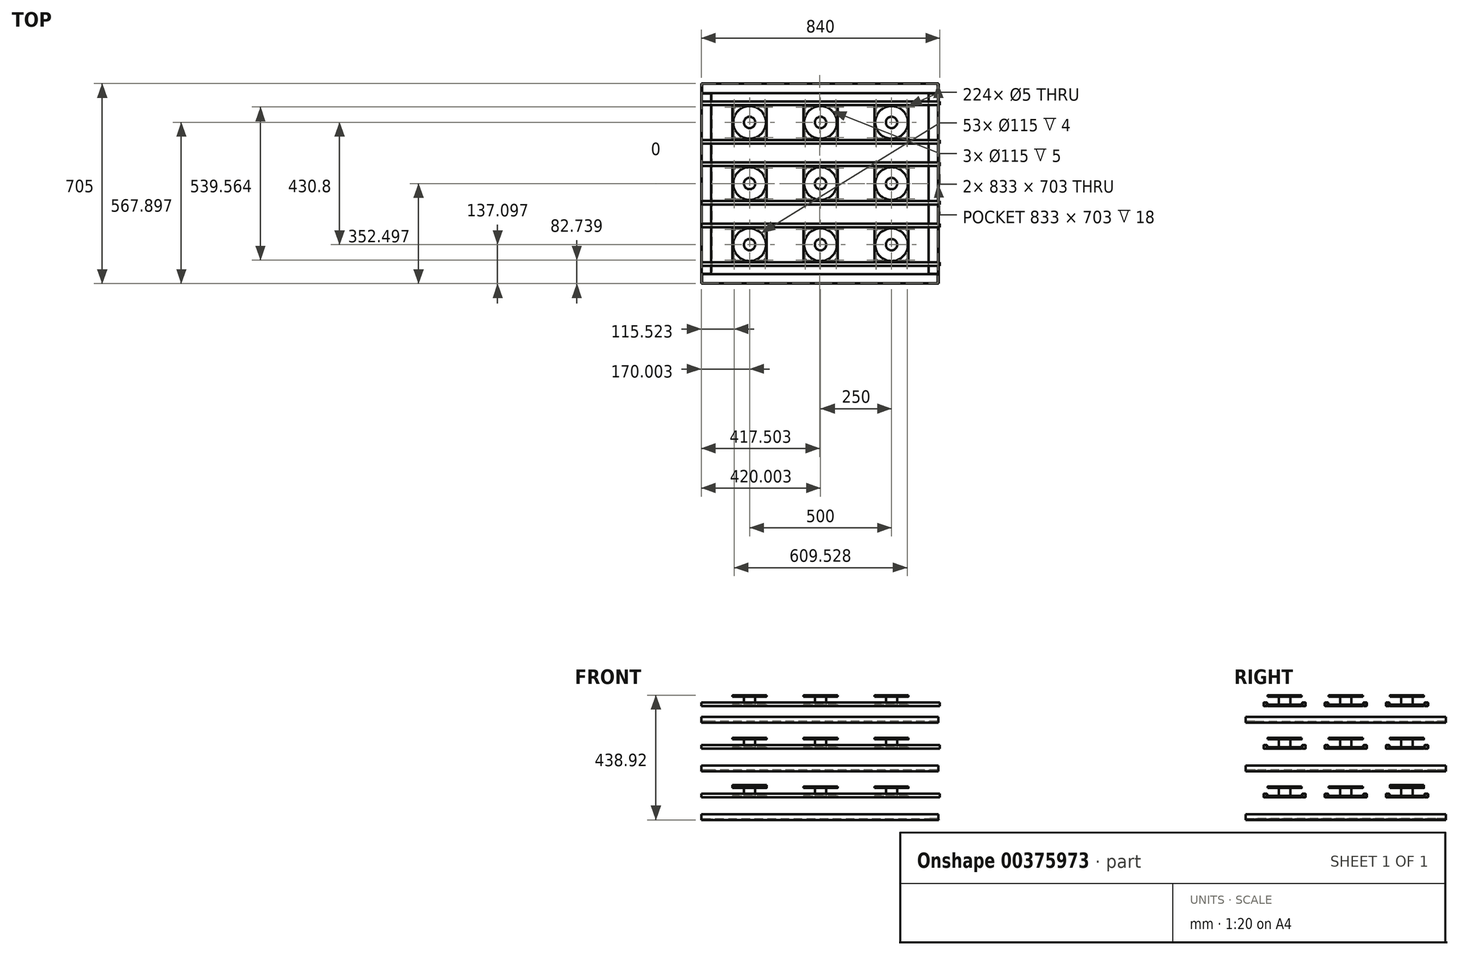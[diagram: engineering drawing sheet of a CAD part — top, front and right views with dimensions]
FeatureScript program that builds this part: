
annotation { "Feature Type Name" : "Feature", "Feature Type Description" : "" }
export const myFeature = defineFeature(function(context is Context, id is Id, definition is map)
    precondition{}
    {
        {
            var Q0;
            Q0=qCreatedBy(makeId("Top.planeOp"),FACE);
            var sketch = newSketch(context, id + "F0", { "sketchPlane" : qUnion([Q0])});
            skLineSegment(sketch, "E0.bottom", {"start": v(-587.5, -350.77) * mm, "end": v(247.5, -350.77) * mm});
            skLineSegment(sketch, "E0.top", {"start": v(-587.5, 354.23) * mm, "end": v(247.5, 354.23) * mm});
            skLineSegment(sketch, "E0.left", {"start": v(-587.5, -350.77) * mm, "end": v(-587.5, 354.23) * mm});
            skLineSegment(sketch, "E0.right", {"start": v(247.5, -350.77) * mm, "end": v(247.5, 354.23) * mm});
            skLineSegment(sketch, "E1.0", {"start": v(-586.5, -349.77) * mm, "end": v(-586.5, 353.23) * mm});
            skLineSegment(sketch, "E1.1", {"start": v(-586.5, -349.77) * mm, "end": v(246.5, -349.77) * mm});
            skLineSegment(sketch, "E1.2", {"start": v(246.5, -349.77) * mm, "end": v(246.5, 353.23) * mm});
            skLineSegment(sketch, "E1.3", {"start": v(-586.5, 353.23) * mm, "end": v(246.5, 353.23) * mm});
            skSolve(sketch);
        }
        {
            var Q0;
            Q0 = qSketchRegion(id + "F0", true);
            extrude(context, id + "F1", {"entities" : qUnion([Q0]), "depth" : 20 * mm});
        }
        {
            var Q0;
            Q0=qCreatedBy(makeId("Top.planeOp"),FACE);
            var sketch = newSketch(context, id + "F2", { "sketchPlane" : qUnion([Q0])});
            skLineSegment(sketch, "E2.bottom", {"start": v(-584.94, 352.72) * mm, "end": v(248.06, 352.72) * mm});
            skLineSegment(sketch, "E2.top", {"start": v(-584.94, -350.28) * mm, "end": v(248.06, -350.28) * mm});
            skLineSegment(sketch, "E2.left", {"start": v(-584.94, 352.72) * mm, "end": v(-584.94, -350.28) * mm});
            skLineSegment(sketch, "E2.right", {"start": v(248.06, 352.72) * mm, "end": v(248.06, -350.28) * mm});
            skSolve(sketch);
        }
        {
            var Q0;
            Q0 = qSketchRegion(id + "F2", true);
            extrude(context, id + "F3", {"entities" : qUnion([Q0]), "operationType" : NewBodyOperationType.ADD, "depth" : 1 * mm});
        }
        {
            var Q0;
            {var subQ0=sQuery(id+"F2.wireOp",EDGE,"E2.left");var subQ1=sQuery(id+"F2.wireOp",EDGE,"E2.bottom");Q0=makeQuery(id+"F3.boolean.opBoolean","SPLIT",FACE,{"disambiguationData":[TD([makeQuery(id+"F1.opExtrude","SWEPT_FACE",FACE,{"disambiguationData":[OSD([sQuery(id+"F0.wireOp",EDGE,"E1.1")])]})])],"derivedFrom":makeQuery(id+"F3.opExtrude","CAP_FACE",FACE,{"disambiguationData":[OSD([subQ1,sQuery(id+"F2.wireOp",EDGE,"E2.top"),subQ0,sQuery(id+"F2.wireOp",EDGE,"E2.right")])],"isStart":false})});}
            var sketch = newSketch(context, id + "F4", { "sketchPlane" : qUnion([Q0])});
            skLineSegment(sketch, "E3.bottom", {"start": v(-169.22, 352.72) * mm, "end": v(-584.22, 352.72) * mm});
            skLineSegment(sketch, "E3.top", {"start": v(-169.22, 319.72) * mm, "end": v(-584.22, 319.72) * mm});
            skLineSegment(sketch, "E3.right", {"start": v(-584.22, 352.72) * mm, "end": v(-584.22, 319.72) * mm});
            skLineSegment(sketch, "E4.bottom", {"start": v(-169.22, 352.72) * mm, "end": v(245.78, 352.72) * mm});
            skLineSegment(sketch, "E4.top", {"start": v(-169.22, 319.72) * mm, "end": v(245.78, 319.72) * mm});
            skLineSegment(sketch, "E4.right", {"start": v(245.78, 352.72) * mm, "end": v(245.78, 319.72) * mm});
            skLineSegment(sketch, "E5.bottom", {"start": v(-169.22, -349.77) * mm, "end": v(245.78, -349.77) * mm});
            skLineSegment(sketch, "E5.top", {"start": v(-169.22, -316.77) * mm, "end": v(245.78, -316.77) * mm});
            skLineSegment(sketch, "E5.right", {"start": v(245.78, -349.77) * mm, "end": v(245.78, -316.77) * mm});
            skLineSegment(sketch, "E6.bottom", {"start": v(-169.22, -349.77) * mm, "end": v(-584.22, -349.77) * mm});
            skLineSegment(sketch, "E6.top", {"start": v(-169.22, -316.77) * mm, "end": v(-584.22, -316.77) * mm});
            skLineSegment(sketch, "E6.right", {"start": v(-584.22, -349.77) * mm, "end": v(-584.22, -316.77) * mm});
            skSolve(sketch);
        }
        {
            var Q0;
            Q0=makeQuery(id+"F4.imprint","IMPRINT",FACE,{"disambiguationData":[TD([[makeQuery(id+"F4.imprint","IMPRINT",EDGE,{"derivedFrom":sQuery(id+"F4.wireOp",EDGE,"E3.bottom")}),-1.0]])]});
            extrude(context, id + "F5", {"entities" : qUnion([Q0]), "depth" : 3 * mm});
        }
        {
            var Q0;
            Q0=makeQuery(id+"F4.imprint","IMPRINT",FACE,{"disambiguationData":[TD([[makeQuery(id+"F4.imprint","IMPRINT",EDGE,{"derivedFrom":sQuery(id+"F4.wireOp",EDGE,"E5.bottom")}),1.0]])]});
            var Q1;
            Q1 = qSketchRegion(id + "F7", true);
            extrude(context, id + "F6", {"entities" : qUnion([Q0, Q1]), "depth" : 3 * mm});
        }
        {
            var Q0;
            {var subQ0=sQuery(id+"F2.wireOp",EDGE,"E2.left");var subQ1=sQuery(id+"F2.wireOp",EDGE,"E2.bottom");Q0=makeQuery(id+"F3.boolean.opBoolean","SPLIT",FACE,{"disambiguationData":[TD([makeQuery(id+"F1.opExtrude","SWEPT_FACE",FACE,{"disambiguationData":[OSD([sQuery(id+"F0.wireOp",EDGE,"E1.1")])]})])],"derivedFrom":makeQuery(id+"F3.opExtrude","CAP_FACE",FACE,{"disambiguationData":[OSD([subQ1,sQuery(id+"F2.wireOp",EDGE,"E2.top"),subQ0,sQuery(id+"F2.wireOp",EDGE,"E2.right")])],"isStart":false})});}
            var sketch = newSketch(context, id + "F7", { "sketchPlane" : qUnion([Q0])});
            skLineSegment(sketch, "E7.top", {"start": v(-584.94, 318.97) * mm, "end": v(-550.94, 318.97) * mm});
            skLineSegment(sketch, "E7.left", {"start": v(-584.94, 1.47) * mm, "end": v(-584.94, 318.97) * mm});
            skLineSegment(sketch, "E7.right", {"start": v(-550.94, 1.47) * mm, "end": v(-550.94, 318.97) * mm});
            skLineSegment(sketch, "E8.top", {"start": v(-584.94, -316.03) * mm, "end": v(-550.94, -316.03) * mm});
            skLineSegment(sketch, "E8.left", {"start": v(-584.94, 1.47) * mm, "end": v(-584.94, -316.03) * mm});
            skLineSegment(sketch, "E8.right", {"start": v(-550.94, 1.47) * mm, "end": v(-550.94, -316.03) * mm});
            skPoint(sketch, "E9.firstSnap0", {"position": v(246.5, 1.47) * mm});
            skLineSegment(sketch, "E9.top", {"start": v(246.5, 317.5) * mm, "end": v(212.5, 317.5) * mm});
            skLineSegment(sketch, "E9.left", {"start": v(246.5, 0) * mm, "end": v(246.5, 317.5) * mm});
            skLineSegment(sketch, "E9.right", {"start": v(212.5, 0) * mm, "end": v(212.5, 317.5) * mm});
            skLineSegment(sketch, "E10.top", {"start": v(246.5, -316.03) * mm, "end": v(212.5, -316.03) * mm});
            skLineSegment(sketch, "E10.left", {"start": v(246.5, 1.47) * mm, "end": v(246.5, -316.03) * mm});
            skLineSegment(sketch, "E10.right", {"start": v(212.5, 1.47) * mm, "end": v(212.5, -316.03) * mm});
            skSolve(sketch);
        }
        {
            var Q0;
            Q0=makeQuery(id+"F7.imprint","IMPRINT",FACE,{"disambiguationData":[TD([[makeQuery(id+"F7.imprint","IMPRINT",EDGE,{"derivedFrom":sQuery(id+"F7.wireOp",EDGE,"E7.top")}),-1.0]])]});
            var Q1;
            Q1=makeQuery(id+"F7.imprint","IMPRINT",FACE,{"disambiguationData":[TD([[makeQuery(id+"F7.imprint","IMPRINT",EDGE,{"derivedFrom":sQuery(id+"F7.wireOp",EDGE,"E9.top")}),1.0]])]});
            extrude(context, id + "F8", {"entities" : qUnion([Q0, Q1]), "depth" : 3 * mm});
        }
        {
            var Q0;
            Q0=makeQuery(id+"F7.imprint","IMPRINT",FACE,{"disambiguationData":[TD([[makeQuery(id+"F7.imprint","IMPRINT",EDGE,{"derivedFrom":sQuery(id+"F7.wireOp",EDGE,"E9.top")}),1.0]])]});
            extrude(context, id + "F9", {"entities" : qUnion([Q0]), "depth" : 3 * mm});
        }
        {
            var Q0;
            Q0=makeQuery(id+"F1.opExtrude","SWEPT_FACE",FACE,{"disambiguationData":[OSD([sQuery(id+"F0.wireOp",EDGE,"E0.left")])]});
            var sketch = newSketch(context, id + "F10", { "sketchPlane" : qUnion([Q0])});
            skLineSegment(sketch, "E11.bottom", {"start": v(285.87, 79.3) * mm, "end": v(277.17, 79.3) * mm});
            skLineSegment(sketch, "E11.top", {"start": v(285.87, 92) * mm, "end": v(277.17, 92) * mm});
            skLineSegment(sketch, "E11.left", {"start": v(287.87, 81.3) * mm, "end": v(287.87, 90) * mm});
            skLineSegment(sketch, "E11.right", {"start": v(275.17, 81.3) * mm, "end": v(275.17, 90) * mm});
            skLineSegment(sketch, "E12.0", {"start": v(286.87, 91) * mm, "end": v(276.17, 91) * mm});
            skLineSegment(sketch, "E12.1", {"start": v(286.87, 80.3) * mm, "end": v(286.87, 91) * mm});
            skLineSegment(sketch, "E12.2", {"start": v(286.87, 80.3) * mm, "end": v(276.17, 80.3) * mm});
            skLineSegment(sketch, "E12.3", {"start": v(276.17, 80.3) * mm, "end": v(276.17, 91) * mm});
            skPoint(sketch, "E13.visualSharp", {"position": v(275.17, 92) * mm});
            skArc(sketch, "E13.filletArc", {"start": v(277.17, 92) * mm, "mid": v(275.76, 91.41) * mm, "end": v(275.17, 90) * mm});
            skPoint(sketch, "E14.visualSharp", {"position": v(275.17, 79.3) * mm});
            skArc(sketch, "E14.filletArc", {"start": v(275.17, 81.3) * mm, "mid": v(275.76, 79.89) * mm, "end": v(277.17, 79.3) * mm});
            skPoint(sketch, "E15.visualSharp", {"position": v(287.87, 92) * mm});
            skArc(sketch, "E15.filletArc", {"start": v(287.87, 90) * mm, "mid": v(287.29, 91.41) * mm, "end": v(285.87, 92) * mm});
            skPoint(sketch, "E16.visualSharp", {"position": v(287.87, 79.3) * mm});
            skArc(sketch, "E16.filletArc", {"start": v(285.87, 79.3) * mm, "mid": v(287.29, 79.89) * mm, "end": v(287.87, 81.3) * mm});
            skLineSegment(sketch, "E17", {"start": v(277.17, 79.3) * mm, "end": v(275.17, 79.3) * mm});
            skLineSegment(sketch, "E18.bottom", {"start": v(150.17, 79.3) * mm, "end": v(141.47, 79.3) * mm});
            skLineSegment(sketch, "E18.top", {"start": v(150.17, 92) * mm, "end": v(141.47, 92) * mm});
            skLineSegment(sketch, "E18.left", {"start": v(152.17, 81.3) * mm, "end": v(152.17, 90) * mm});
            skLineSegment(sketch, "E18.right", {"start": v(139.47, 81.3) * mm, "end": v(139.47, 90) * mm});
            skLineSegment(sketch, "E19.0", {"start": v(151.17, 91) * mm, "end": v(140.47, 91) * mm});
            skLineSegment(sketch, "E19.1", {"start": v(151.17, 80.3) * mm, "end": v(151.17, 91) * mm});
            skLineSegment(sketch, "E19.2", {"start": v(151.17, 80.3) * mm, "end": v(140.47, 80.3) * mm});
            skLineSegment(sketch, "E19.3", {"start": v(140.47, 80.3) * mm, "end": v(140.47, 91) * mm});
            skPoint(sketch, "E20.visualSharp", {"position": v(152.17, 79.3) * mm});
            skArc(sketch, "E20.filletArc", {"start": v(150.17, 79.3) * mm, "mid": v(151.59, 79.89) * mm, "end": v(152.17, 81.3) * mm});
            skPoint(sketch, "E21.visualSharp", {"position": v(139.47, 79.3) * mm});
            skArc(sketch, "E21.filletArc", {"start": v(139.47, 81.3) * mm, "mid": v(140.06, 79.89) * mm, "end": v(141.47, 79.3) * mm});
            skPoint(sketch, "E22.visualSharp", {"position": v(139.47, 92) * mm});
            skArc(sketch, "E22.filletArc", {"start": v(141.47, 92) * mm, "mid": v(140.06, 91.41) * mm, "end": v(139.47, 90) * mm});
            skPoint(sketch, "E23.visualSharp", {"position": v(152.17, 92) * mm});
            skArc(sketch, "E23.filletArc", {"start": v(152.17, 90) * mm, "mid": v(151.59, 91.41) * mm, "end": v(150.17, 92) * mm});
            skLineSegment(sketch, "E24.bottom", {"start": v(70.47, 79.3) * mm, "end": v(61.77, 79.3) * mm});
            skLineSegment(sketch, "E24.top", {"start": v(70.47, 92) * mm, "end": v(61.77, 92) * mm});
            skLineSegment(sketch, "E24.left", {"start": v(72.47, 81.3) * mm, "end": v(72.47, 90) * mm});
            skLineSegment(sketch, "E24.right", {"start": v(59.77, 81.3) * mm, "end": v(59.77, 90) * mm});
            skLineSegment(sketch, "E25.0", {"start": v(60.77, 80.3) * mm, "end": v(60.77, 91) * mm});
            skLineSegment(sketch, "E25.1", {"start": v(71.47, 80.3) * mm, "end": v(60.77, 80.3) * mm});
            skLineSegment(sketch, "E25.2", {"start": v(71.47, 80.3) * mm, "end": v(71.47, 91) * mm});
            skLineSegment(sketch, "E25.3", {"start": v(71.47, 91) * mm, "end": v(60.77, 91) * mm});
            skPoint(sketch, "E26.visualSharp", {"position": v(59.77, 92) * mm});
            skArc(sketch, "E26.filletArc", {"start": v(61.77, 92) * mm, "mid": v(60.36, 91.41) * mm, "end": v(59.77, 90) * mm});
            skPoint(sketch, "E27.visualSharp", {"position": v(72.47, 92) * mm});
            skArc(sketch, "E27.filletArc", {"start": v(72.47, 90) * mm, "mid": v(71.89, 91.41) * mm, "end": v(70.47, 92) * mm});
            skPoint(sketch, "E28.visualSharp", {"position": v(59.77, 79.3) * mm});
            skArc(sketch, "E28.filletArc", {"start": v(59.77, 81.3) * mm, "mid": v(60.36, 79.89) * mm, "end": v(61.77, 79.3) * mm});
            skPoint(sketch, "E29.visualSharp", {"position": v(72.47, 79.3) * mm});
            skArc(sketch, "E29.filletArc", {"start": v(70.47, 79.3) * mm, "mid": v(71.89, 79.89) * mm, "end": v(72.47, 81.3) * mm});
            skLineSegment(sketch, "E30.bottom", {"start": v(-65.23, 79.3) * mm, "end": v(-73.93, 79.3) * mm});
            skLineSegment(sketch, "E30.top", {"start": v(-65.23, 92) * mm, "end": v(-73.93, 92) * mm});
            skLineSegment(sketch, "E30.left", {"start": v(-63.23, 81.3) * mm, "end": v(-63.23, 90) * mm});
            skLineSegment(sketch, "E30.right", {"start": v(-75.93, 81.3) * mm, "end": v(-75.93, 90) * mm});
            skLineSegment(sketch, "E31.0", {"start": v(-74.93, 80.3) * mm, "end": v(-74.93, 91) * mm});
            skLineSegment(sketch, "E31.1", {"start": v(-64.23, 80.3) * mm, "end": v(-74.93, 80.3) * mm});
            skLineSegment(sketch, "E31.2", {"start": v(-64.23, 80.3) * mm, "end": v(-64.23, 91) * mm});
            skLineSegment(sketch, "E31.3", {"start": v(-64.23, 91) * mm, "end": v(-74.93, 91) * mm});
            skPoint(sketch, "E32.visualSharp", {"position": v(-75.93, 92) * mm});
            skArc(sketch, "E32.filletArc", {"start": v(-73.93, 92) * mm, "mid": v(-75.34, 91.41) * mm, "end": v(-75.93, 90) * mm});
            skPoint(sketch, "E33.visualSharp", {"position": v(-63.23, 92) * mm});
            skArc(sketch, "E33.filletArc", {"start": v(-63.23, 90) * mm, "mid": v(-63.81, 91.41) * mm, "end": v(-65.23, 92) * mm});
            skPoint(sketch, "E34.visualSharp", {"position": v(-75.93, 79.3) * mm});
            skArc(sketch, "E34.filletArc", {"start": v(-75.93, 81.3) * mm, "mid": v(-75.34, 79.89) * mm, "end": v(-73.93, 79.3) * mm});
            skPoint(sketch, "E35.visualSharp", {"position": v(-63.23, 79.3) * mm});
            skArc(sketch, "E35.filletArc", {"start": v(-65.23, 79.3) * mm, "mid": v(-63.81, 79.89) * mm, "end": v(-63.23, 81.3) * mm});
            skLineSegment(sketch, "E36.bottom", {"start": v(-144.93, 79.3) * mm, "end": v(-153.63, 79.3) * mm});
            skLineSegment(sketch, "E36.top", {"start": v(-144.93, 92) * mm, "end": v(-153.63, 92) * mm});
            skLineSegment(sketch, "E36.left", {"start": v(-142.93, 81.3) * mm, "end": v(-142.93, 90) * mm});
            skLineSegment(sketch, "E36.right", {"start": v(-155.63, 81.3) * mm, "end": v(-155.63, 90) * mm});
            skLineSegment(sketch, "E37.0", {"start": v(-143.93, 91) * mm, "end": v(-154.63, 91) * mm});
            skLineSegment(sketch, "E37.1", {"start": v(-143.93, 80.3) * mm, "end": v(-143.93, 91) * mm});
            skLineSegment(sketch, "E37.2", {"start": v(-143.93, 80.3) * mm, "end": v(-154.63, 80.3) * mm});
            skLineSegment(sketch, "E37.3", {"start": v(-154.63, 80.3) * mm, "end": v(-154.63, 91) * mm});
            skPoint(sketch, "E38.visualSharp", {"position": v(-155.63, 92) * mm});
            skArc(sketch, "E38.filletArc", {"start": v(-153.63, 92) * mm, "mid": v(-155.04, 91.41) * mm, "end": v(-155.63, 90) * mm});
            skPoint(sketch, "E39.visualSharp", {"position": v(-142.93, 92) * mm});
            skArc(sketch, "E39.filletArc", {"start": v(-142.93, 90) * mm, "mid": v(-143.51, 91.41) * mm, "end": v(-144.93, 92) * mm});
            skPoint(sketch, "E40.visualSharp", {"position": v(-155.63, 79.3) * mm});
            skArc(sketch, "E40.filletArc", {"start": v(-155.63, 81.3) * mm, "mid": v(-155.04, 79.89) * mm, "end": v(-153.63, 79.3) * mm});
            skPoint(sketch, "E41.visualSharp", {"position": v(-142.93, 79.3) * mm});
            skArc(sketch, "E41.filletArc", {"start": v(-144.93, 79.3) * mm, "mid": v(-143.51, 79.89) * mm, "end": v(-142.93, 81.3) * mm});
            skLineSegment(sketch, "E42.bottom", {"start": v(-280.63, 79.3) * mm, "end": v(-289.33, 79.3) * mm});
            skLineSegment(sketch, "E42.top", {"start": v(-280.63, 92) * mm, "end": v(-289.33, 92) * mm});
            skLineSegment(sketch, "E42.left", {"start": v(-278.63, 81.3) * mm, "end": v(-278.63, 90) * mm});
            skLineSegment(sketch, "E42.right", {"start": v(-291.33, 81.3) * mm, "end": v(-291.33, 90) * mm});
            skLineSegment(sketch, "E43.0", {"start": v(-290.33, 80.3) * mm, "end": v(-290.33, 91) * mm});
            skLineSegment(sketch, "E43.1", {"start": v(-279.63, 80.3) * mm, "end": v(-290.33, 80.3) * mm});
            skLineSegment(sketch, "E43.2", {"start": v(-279.63, 80.3) * mm, "end": v(-279.63, 91) * mm});
            skLineSegment(sketch, "E43.3", {"start": v(-279.63, 91) * mm, "end": v(-290.33, 91) * mm});
            skPoint(sketch, "E44.visualSharp", {"position": v(-291.33, 92) * mm});
            skArc(sketch, "E44.filletArc", {"start": v(-289.33, 92) * mm, "mid": v(-290.74, 91.41) * mm, "end": v(-291.33, 90) * mm});
            skPoint(sketch, "E45.visualSharp", {"position": v(-278.63, 92) * mm});
            skArc(sketch, "E45.filletArc", {"start": v(-278.63, 90) * mm, "mid": v(-279.21, 91.41) * mm, "end": v(-280.63, 92) * mm});
            skPoint(sketch, "E46.visualSharp", {"position": v(-291.33, 79.3) * mm});
            skArc(sketch, "E46.filletArc", {"start": v(-291.33, 81.3) * mm, "mid": v(-290.74, 79.89) * mm, "end": v(-289.33, 79.3) * mm});
            skPoint(sketch, "E47.visualSharp", {"position": v(-278.63, 79.3) * mm});
            skArc(sketch, "E47.filletArc", {"start": v(-280.63, 79.3) * mm, "mid": v(-279.21, 79.89) * mm, "end": v(-278.63, 81.3) * mm});
            skLineSegment(sketch, "E48", {"start": v(275.17, 79.3) * mm, "end": v(152.17, 79.3) * mm, "construction": true});
            skLineSegment(sketch, "E49", {"start": v(139.47, 79.3) * mm, "end": v(72.47, 79.3) * mm, "construction": true});
            skLineSegment(sketch, "E50", {"start": v(59.77, 79.3) * mm, "end": v(-63.23, 79.3) * mm, "construction": true});
            skLineSegment(sketch, "E51", {"start": v(-75.93, 79.3) * mm, "end": v(-142.93, 79.3) * mm, "construction": true});
            skLineSegment(sketch, "E52", {"start": v(-278.63, 79.3) * mm, "end": v(-155.63, 79.3) * mm, "construction": true});
            skLineSegment(sketch, "E53", {"start": v(-291.33, 79.3) * mm, "end": v(-291.33, 0) * mm, "construction": true});
            skLineSegment(sketch, "E54", {"start": v(-291.33, 0) * mm, "end": v(-354.23, 0) * mm, "construction": true});
            skLineSegment(sketch, "E55", {"start": v(287.87, 79.3) * mm, "end": v(287.87, 0) * mm, "construction": true});
            skLineSegment(sketch, "E56", {"start": v(287.87, 0) * mm, "end": v(350.77, 0) * mm, "construction": true});
            skLineSegment(sketch, "E57", {"start": v(-291.33, 92) * mm, "end": v(-291.33, 171.3) * mm, "construction": true});
            skLineSegment(sketch, "E58.bottom", {"start": v(285.87, 250.6) * mm, "end": v(277.17, 250.6) * mm});
            skLineSegment(sketch, "E58.top", {"start": v(285.87, 263.3) * mm, "end": v(277.17, 263.3) * mm});
            skLineSegment(sketch, "E58.left", {"start": v(287.87, 252.6) * mm, "end": v(287.87, 261.3) * mm});
            skLineSegment(sketch, "E58.right", {"start": v(275.17, 252.6) * mm, "end": v(275.17, 261.3) * mm});
            skLineSegment(sketch, "E59.0", {"start": v(286.87, 262.3) * mm, "end": v(276.17, 262.3) * mm});
            skLineSegment(sketch, "E59.1", {"start": v(286.87, 251.6) * mm, "end": v(286.87, 262.3) * mm});
            skLineSegment(sketch, "E59.2", {"start": v(286.87, 251.6) * mm, "end": v(276.17, 251.6) * mm});
            skLineSegment(sketch, "E59.3", {"start": v(276.17, 251.6) * mm, "end": v(276.17, 262.3) * mm});
            skPoint(sketch, "E60.visualSharp", {"position": v(275.17, 263.3) * mm});
            skArc(sketch, "E60.filletArc", {"start": v(277.17, 263.3) * mm, "mid": v(275.76, 262.71) * mm, "end": v(275.17, 261.3) * mm});
            skPoint(sketch, "E61.visualSharp", {"position": v(275.17, 250.6) * mm});
            skArc(sketch, "E61.filletArc", {"start": v(275.17, 252.6) * mm, "mid": v(275.76, 251.19) * mm, "end": v(277.17, 250.6) * mm});
            skPoint(sketch, "E62.visualSharp", {"position": v(287.87, 263.3) * mm});
            skArc(sketch, "E62.filletArc", {"start": v(287.87, 261.3) * mm, "mid": v(287.29, 262.71) * mm, "end": v(285.87, 263.3) * mm});
            skPoint(sketch, "E63.visualSharp", {"position": v(287.87, 250.6) * mm});
            skArc(sketch, "E63.filletArc", {"start": v(285.87, 250.6) * mm, "mid": v(287.29, 251.19) * mm, "end": v(287.87, 252.6) * mm});
            skLineSegment(sketch, "E64", {"start": v(277.17, 250.6) * mm, "end": v(275.17, 250.6) * mm});
            skLineSegment(sketch, "E65.bottom", {"start": v(150.17, 250.6) * mm, "end": v(141.47, 250.6) * mm});
            skLineSegment(sketch, "E65.top", {"start": v(150.17, 263.3) * mm, "end": v(141.47, 263.3) * mm});
            skLineSegment(sketch, "E65.left", {"start": v(152.17, 252.6) * mm, "end": v(152.17, 261.3) * mm});
            skLineSegment(sketch, "E65.right", {"start": v(139.47, 252.6) * mm, "end": v(139.47, 261.3) * mm});
            skLineSegment(sketch, "E66.0", {"start": v(151.17, 262.3) * mm, "end": v(140.47, 262.3) * mm});
            skLineSegment(sketch, "E66.1", {"start": v(151.17, 251.6) * mm, "end": v(151.17, 262.3) * mm});
            skLineSegment(sketch, "E66.2", {"start": v(151.17, 251.6) * mm, "end": v(140.47, 251.6) * mm});
            skLineSegment(sketch, "E66.3", {"start": v(140.47, 251.6) * mm, "end": v(140.47, 262.3) * mm});
            skPoint(sketch, "E67.visualSharp", {"position": v(152.17, 250.6) * mm});
            skArc(sketch, "E67.filletArc", {"start": v(150.17, 250.6) * mm, "mid": v(151.59, 251.19) * mm, "end": v(152.17, 252.6) * mm});
            skPoint(sketch, "E68.visualSharp", {"position": v(139.47, 250.6) * mm});
            skArc(sketch, "E68.filletArc", {"start": v(139.47, 252.6) * mm, "mid": v(140.06, 251.19) * mm, "end": v(141.47, 250.6) * mm});
            skPoint(sketch, "E69.visualSharp", {"position": v(139.47, 263.3) * mm});
            skArc(sketch, "E69.filletArc", {"start": v(141.47, 263.3) * mm, "mid": v(140.06, 262.71) * mm, "end": v(139.47, 261.3) * mm});
            skPoint(sketch, "E70.visualSharp", {"position": v(152.17, 263.3) * mm});
            skArc(sketch, "E70.filletArc", {"start": v(152.17, 261.3) * mm, "mid": v(151.59, 262.71) * mm, "end": v(150.17, 263.3) * mm});
            skLineSegment(sketch, "E71.bottom", {"start": v(70.47, 250.6) * mm, "end": v(61.77, 250.6) * mm});
            skLineSegment(sketch, "E71.top", {"start": v(70.47, 263.3) * mm, "end": v(61.77, 263.3) * mm});
            skLineSegment(sketch, "E71.left", {"start": v(72.47, 252.6) * mm, "end": v(72.47, 261.3) * mm});
            skLineSegment(sketch, "E71.right", {"start": v(59.77, 252.6) * mm, "end": v(59.77, 261.3) * mm});
            skLineSegment(sketch, "E72.0", {"start": v(60.77, 251.6) * mm, "end": v(60.77, 262.3) * mm});
            skLineSegment(sketch, "E72.1", {"start": v(71.47, 251.6) * mm, "end": v(60.77, 251.6) * mm});
            skLineSegment(sketch, "E72.2", {"start": v(71.47, 251.6) * mm, "end": v(71.47, 262.3) * mm});
            skLineSegment(sketch, "E72.3", {"start": v(71.47, 262.3) * mm, "end": v(60.77, 262.3) * mm});
            skPoint(sketch, "E73.visualSharp", {"position": v(59.77, 263.3) * mm});
            skArc(sketch, "E73.filletArc", {"start": v(61.77, 263.3) * mm, "mid": v(60.36, 262.71) * mm, "end": v(59.77, 261.3) * mm});
            skPoint(sketch, "E74.visualSharp", {"position": v(72.47, 263.3) * mm});
            skArc(sketch, "E74.filletArc", {"start": v(72.47, 261.3) * mm, "mid": v(71.89, 262.71) * mm, "end": v(70.47, 263.3) * mm});
            skPoint(sketch, "E75.visualSharp", {"position": v(59.77, 250.6) * mm});
            skArc(sketch, "E75.filletArc", {"start": v(59.77, 252.6) * mm, "mid": v(60.36, 251.19) * mm, "end": v(61.77, 250.6) * mm});
            skPoint(sketch, "E76.visualSharp", {"position": v(72.47, 250.6) * mm});
            skArc(sketch, "E76.filletArc", {"start": v(70.47, 250.6) * mm, "mid": v(71.89, 251.19) * mm, "end": v(72.47, 252.6) * mm});
            skLineSegment(sketch, "E77.bottom", {"start": v(-65.23, 250.6) * mm, "end": v(-73.93, 250.6) * mm});
            skLineSegment(sketch, "E77.top", {"start": v(-65.23, 263.3) * mm, "end": v(-73.93, 263.3) * mm});
            skLineSegment(sketch, "E77.left", {"start": v(-63.23, 252.6) * mm, "end": v(-63.23, 261.3) * mm});
            skLineSegment(sketch, "E77.right", {"start": v(-75.93, 252.6) * mm, "end": v(-75.93, 261.3) * mm});
            skLineSegment(sketch, "E78.0", {"start": v(-74.93, 251.6) * mm, "end": v(-74.93, 262.3) * mm});
            skLineSegment(sketch, "E78.1", {"start": v(-64.23, 251.6) * mm, "end": v(-74.93, 251.6) * mm});
            skLineSegment(sketch, "E78.2", {"start": v(-64.23, 251.6) * mm, "end": v(-64.23, 262.3) * mm});
            skLineSegment(sketch, "E78.3", {"start": v(-64.23, 262.3) * mm, "end": v(-74.93, 262.3) * mm});
            skPoint(sketch, "E79.visualSharp", {"position": v(-75.93, 263.3) * mm});
            skArc(sketch, "E79.filletArc", {"start": v(-73.93, 263.3) * mm, "mid": v(-75.34, 262.71) * mm, "end": v(-75.93, 261.3) * mm});
            skPoint(sketch, "E80.visualSharp", {"position": v(-63.23, 263.3) * mm});
            skArc(sketch, "E80.filletArc", {"start": v(-63.23, 261.3) * mm, "mid": v(-63.81, 262.71) * mm, "end": v(-65.23, 263.3) * mm});
            skPoint(sketch, "E81.visualSharp", {"position": v(-75.93, 250.6) * mm});
            skArc(sketch, "E81.filletArc", {"start": v(-75.93, 252.6) * mm, "mid": v(-75.34, 251.19) * mm, "end": v(-73.93, 250.6) * mm});
            skPoint(sketch, "E82.visualSharp", {"position": v(-63.23, 250.6) * mm});
            skArc(sketch, "E82.filletArc", {"start": v(-65.23, 250.6) * mm, "mid": v(-63.81, 251.19) * mm, "end": v(-63.23, 252.6) * mm});
            skLineSegment(sketch, "E83.bottom", {"start": v(-144.93, 250.6) * mm, "end": v(-153.63, 250.6) * mm});
            skLineSegment(sketch, "E83.top", {"start": v(-144.93, 263.3) * mm, "end": v(-153.63, 263.3) * mm});
            skLineSegment(sketch, "E83.left", {"start": v(-142.93, 252.6) * mm, "end": v(-142.93, 261.3) * mm});
            skLineSegment(sketch, "E83.right", {"start": v(-155.63, 252.6) * mm, "end": v(-155.63, 261.3) * mm});
            skLineSegment(sketch, "E84.0", {"start": v(-143.93, 262.3) * mm, "end": v(-154.63, 262.3) * mm});
            skLineSegment(sketch, "E84.1", {"start": v(-143.93, 251.6) * mm, "end": v(-143.93, 262.3) * mm});
            skLineSegment(sketch, "E84.2", {"start": v(-143.93, 251.6) * mm, "end": v(-154.63, 251.6) * mm});
            skLineSegment(sketch, "E84.3", {"start": v(-154.63, 251.6) * mm, "end": v(-154.63, 262.3) * mm});
            skPoint(sketch, "E85.visualSharp", {"position": v(-155.63, 263.3) * mm});
            skArc(sketch, "E85.filletArc", {"start": v(-153.63, 263.3) * mm, "mid": v(-155.04, 262.71) * mm, "end": v(-155.63, 261.3) * mm});
            skPoint(sketch, "E86.visualSharp", {"position": v(-142.93, 263.3) * mm});
            skArc(sketch, "E86.filletArc", {"start": v(-142.93, 261.3) * mm, "mid": v(-143.51, 262.71) * mm, "end": v(-144.93, 263.3) * mm});
            skPoint(sketch, "E87.visualSharp", {"position": v(-155.63, 250.6) * mm});
            skArc(sketch, "E87.filletArc", {"start": v(-155.63, 252.6) * mm, "mid": v(-155.04, 251.19) * mm, "end": v(-153.63, 250.6) * mm});
            skPoint(sketch, "E88.visualSharp", {"position": v(-142.93, 250.6) * mm});
            skArc(sketch, "E88.filletArc", {"start": v(-144.93, 250.6) * mm, "mid": v(-143.51, 251.19) * mm, "end": v(-142.93, 252.6) * mm});
            skLineSegment(sketch, "E89.bottom", {"start": v(-280.63, 250.6) * mm, "end": v(-289.33, 250.6) * mm});
            skLineSegment(sketch, "E89.top", {"start": v(-280.63, 263.3) * mm, "end": v(-289.33, 263.3) * mm});
            skLineSegment(sketch, "E89.left", {"start": v(-278.63, 252.6) * mm, "end": v(-278.63, 261.3) * mm});
            skLineSegment(sketch, "E89.right", {"start": v(-291.33, 252.6) * mm, "end": v(-291.33, 261.3) * mm});
            skLineSegment(sketch, "E90.0", {"start": v(-290.33, 251.6) * mm, "end": v(-290.33, 262.3) * mm});
            skLineSegment(sketch, "E90.1", {"start": v(-279.63, 251.6) * mm, "end": v(-290.33, 251.6) * mm});
            skLineSegment(sketch, "E90.2", {"start": v(-279.63, 251.6) * mm, "end": v(-279.63, 262.3) * mm});
            skLineSegment(sketch, "E90.3", {"start": v(-279.63, 262.3) * mm, "end": v(-290.33, 262.3) * mm});
            skPoint(sketch, "E91.visualSharp", {"position": v(-291.33, 263.3) * mm});
            skArc(sketch, "E91.filletArc", {"start": v(-289.33, 263.3) * mm, "mid": v(-290.74, 262.71) * mm, "end": v(-291.33, 261.3) * mm});
            skPoint(sketch, "E92.visualSharp", {"position": v(-278.63, 263.3) * mm});
            skArc(sketch, "E92.filletArc", {"start": v(-278.63, 261.3) * mm, "mid": v(-279.21, 262.71) * mm, "end": v(-280.63, 263.3) * mm});
            skPoint(sketch, "E93.visualSharp", {"position": v(-291.33, 250.6) * mm});
            skArc(sketch, "E93.filletArc", {"start": v(-291.33, 252.6) * mm, "mid": v(-290.74, 251.19) * mm, "end": v(-289.33, 250.6) * mm});
            skPoint(sketch, "E94.visualSharp", {"position": v(-278.63, 250.6) * mm});
            skArc(sketch, "E94.filletArc", {"start": v(-280.63, 250.6) * mm, "mid": v(-279.21, 251.19) * mm, "end": v(-278.63, 252.6) * mm});
            skLineSegment(sketch, "E95", {"start": v(275.17, 250.6) * mm, "end": v(152.17, 250.6) * mm, "construction": true});
            skLineSegment(sketch, "E96", {"start": v(139.47, 250.6) * mm, "end": v(72.47, 250.6) * mm, "construction": true});
            skLineSegment(sketch, "E97", {"start": v(59.77, 250.6) * mm, "end": v(-63.23, 250.6) * mm, "construction": true});
            skLineSegment(sketch, "E98", {"start": v(-75.93, 250.6) * mm, "end": v(-142.93, 250.6) * mm, "construction": true});
            skLineSegment(sketch, "E99", {"start": v(-278.63, 250.6) * mm, "end": v(-155.63, 250.6) * mm, "construction": true});
            skLineSegment(sketch, "E100", {"start": v(-291.33, 263.3) * mm, "end": v(-291.33, 342.6) * mm, "construction": true});
            skLineSegment(sketch, "E101", {"start": v(-291.33, 342.6) * mm, "end": v(-291.33, 400.92) * mm, "construction": true});
            skLineSegment(sketch, "E102.bottom", {"start": v(285.87, 400.92) * mm, "end": v(277.17, 400.92) * mm});
            skLineSegment(sketch, "E102.top", {"start": v(285.87, 413.62) * mm, "end": v(277.17, 413.62) * mm});
            skLineSegment(sketch, "E102.left", {"start": v(287.87, 402.92) * mm, "end": v(287.87, 411.62) * mm});
            skLineSegment(sketch, "E102.right", {"start": v(275.17, 402.92) * mm, "end": v(275.17, 411.62) * mm});
            skLineSegment(sketch, "E103.0", {"start": v(286.87, 412.62) * mm, "end": v(276.17, 412.62) * mm});
            skLineSegment(sketch, "E103.1", {"start": v(286.87, 401.92) * mm, "end": v(286.87, 412.62) * mm});
            skLineSegment(sketch, "E103.2", {"start": v(286.87, 401.92) * mm, "end": v(276.17, 401.92) * mm});
            skLineSegment(sketch, "E103.3", {"start": v(276.17, 401.92) * mm, "end": v(276.17, 412.62) * mm});
            skPoint(sketch, "E104.visualSharp", {"position": v(275.17, 413.62) * mm});
            skArc(sketch, "E104.filletArc", {"start": v(277.17, 413.62) * mm, "mid": v(275.76, 413.03) * mm, "end": v(275.17, 411.62) * mm});
            skPoint(sketch, "E105.visualSharp", {"position": v(275.17, 400.92) * mm});
            skArc(sketch, "E105.filletArc", {"start": v(275.17, 402.92) * mm, "mid": v(275.76, 401.5) * mm, "end": v(277.17, 400.92) * mm});
            skPoint(sketch, "E106.visualSharp", {"position": v(287.87, 413.62) * mm});
            skArc(sketch, "E106.filletArc", {"start": v(287.87, 411.62) * mm, "mid": v(287.29, 413.03) * mm, "end": v(285.87, 413.62) * mm});
            skPoint(sketch, "E107.visualSharp", {"position": v(287.87, 400.92) * mm});
            skArc(sketch, "E107.filletArc", {"start": v(285.87, 400.92) * mm, "mid": v(287.29, 401.5) * mm, "end": v(287.87, 402.92) * mm});
            skLineSegment(sketch, "E108", {"start": v(277.17, 400.92) * mm, "end": v(275.17, 400.92) * mm});
            skLineSegment(sketch, "E109.bottom", {"start": v(150.17, 400.92) * mm, "end": v(141.47, 400.92) * mm});
            skLineSegment(sketch, "E109.top", {"start": v(150.17, 413.62) * mm, "end": v(141.47, 413.62) * mm});
            skLineSegment(sketch, "E109.left", {"start": v(152.17, 402.92) * mm, "end": v(152.17, 411.62) * mm});
            skLineSegment(sketch, "E109.right", {"start": v(139.47, 402.92) * mm, "end": v(139.47, 411.62) * mm});
            skLineSegment(sketch, "E110.0", {"start": v(151.17, 412.62) * mm, "end": v(140.47, 412.62) * mm});
            skLineSegment(sketch, "E110.1", {"start": v(151.17, 401.92) * mm, "end": v(151.17, 412.62) * mm});
            skLineSegment(sketch, "E110.2", {"start": v(151.17, 401.92) * mm, "end": v(140.47, 401.92) * mm});
            skLineSegment(sketch, "E110.3", {"start": v(140.47, 401.92) * mm, "end": v(140.47, 412.62) * mm});
            skPoint(sketch, "E111.visualSharp", {"position": v(152.17, 400.92) * mm});
            skArc(sketch, "E111.filletArc", {"start": v(150.17, 400.92) * mm, "mid": v(151.59, 401.5) * mm, "end": v(152.17, 402.92) * mm});
            skPoint(sketch, "E112.visualSharp", {"position": v(139.47, 400.92) * mm});
            skArc(sketch, "E112.filletArc", {"start": v(139.47, 402.92) * mm, "mid": v(140.06, 401.5) * mm, "end": v(141.47, 400.92) * mm});
            skPoint(sketch, "E113.visualSharp", {"position": v(139.47, 413.62) * mm});
            skArc(sketch, "E113.filletArc", {"start": v(141.47, 413.62) * mm, "mid": v(140.06, 413.03) * mm, "end": v(139.47, 411.62) * mm});
            skPoint(sketch, "E114.visualSharp", {"position": v(152.17, 413.62) * mm});
            skArc(sketch, "E114.filletArc", {"start": v(152.17, 411.62) * mm, "mid": v(151.59, 413.03) * mm, "end": v(150.17, 413.62) * mm});
            skLineSegment(sketch, "E115.bottom", {"start": v(70.47, 400.92) * mm, "end": v(61.77, 400.92) * mm});
            skLineSegment(sketch, "E115.top", {"start": v(70.47, 413.62) * mm, "end": v(61.77, 413.62) * mm});
            skLineSegment(sketch, "E115.left", {"start": v(72.47, 402.92) * mm, "end": v(72.47, 411.62) * mm});
            skLineSegment(sketch, "E115.right", {"start": v(59.77, 402.92) * mm, "end": v(59.77, 411.62) * mm});
            skLineSegment(sketch, "E116.0", {"start": v(60.77, 401.92) * mm, "end": v(60.77, 412.62) * mm});
            skLineSegment(sketch, "E116.1", {"start": v(71.47, 401.92) * mm, "end": v(60.77, 401.92) * mm});
            skLineSegment(sketch, "E116.2", {"start": v(71.47, 401.92) * mm, "end": v(71.47, 412.62) * mm});
            skLineSegment(sketch, "E116.3", {"start": v(71.47, 412.62) * mm, "end": v(60.77, 412.62) * mm});
            skPoint(sketch, "E117.visualSharp", {"position": v(59.77, 413.62) * mm});
            skArc(sketch, "E117.filletArc", {"start": v(61.77, 413.62) * mm, "mid": v(60.36, 413.03) * mm, "end": v(59.77, 411.62) * mm});
            skPoint(sketch, "E118.visualSharp", {"position": v(72.47, 413.62) * mm});
            skArc(sketch, "E118.filletArc", {"start": v(72.47, 411.62) * mm, "mid": v(71.89, 413.03) * mm, "end": v(70.47, 413.62) * mm});
            skPoint(sketch, "E119.visualSharp", {"position": v(59.77, 400.92) * mm});
            skArc(sketch, "E119.filletArc", {"start": v(59.77, 402.92) * mm, "mid": v(60.36, 401.5) * mm, "end": v(61.77, 400.92) * mm});
            skPoint(sketch, "E120.visualSharp", {"position": v(72.47, 400.92) * mm});
            skArc(sketch, "E120.filletArc", {"start": v(70.47, 400.92) * mm, "mid": v(71.89, 401.5) * mm, "end": v(72.47, 402.92) * mm});
            skLineSegment(sketch, "E121.bottom", {"start": v(-65.23, 400.92) * mm, "end": v(-73.93, 400.92) * mm});
            skLineSegment(sketch, "E121.top", {"start": v(-65.23, 413.62) * mm, "end": v(-73.93, 413.62) * mm});
            skLineSegment(sketch, "E121.left", {"start": v(-63.23, 402.92) * mm, "end": v(-63.23, 411.62) * mm});
            skLineSegment(sketch, "E121.right", {"start": v(-75.93, 402.92) * mm, "end": v(-75.93, 411.62) * mm});
            skLineSegment(sketch, "E122.0", {"start": v(-74.93, 401.92) * mm, "end": v(-74.93, 412.62) * mm});
            skLineSegment(sketch, "E122.1", {"start": v(-64.23, 401.92) * mm, "end": v(-74.93, 401.92) * mm});
            skLineSegment(sketch, "E122.2", {"start": v(-64.23, 401.92) * mm, "end": v(-64.23, 412.62) * mm});
            skLineSegment(sketch, "E122.3", {"start": v(-64.23, 412.62) * mm, "end": v(-74.93, 412.62) * mm});
            skPoint(sketch, "E123.visualSharp", {"position": v(-75.93, 413.62) * mm});
            skArc(sketch, "E123.filletArc", {"start": v(-73.93, 413.62) * mm, "mid": v(-75.34, 413.03) * mm, "end": v(-75.93, 411.62) * mm});
            skPoint(sketch, "E124.visualSharp", {"position": v(-63.23, 413.62) * mm});
            skArc(sketch, "E124.filletArc", {"start": v(-63.23, 411.62) * mm, "mid": v(-63.81, 413.03) * mm, "end": v(-65.23, 413.62) * mm});
            skPoint(sketch, "E125.visualSharp", {"position": v(-75.93, 400.92) * mm});
            skArc(sketch, "E125.filletArc", {"start": v(-75.93, 402.92) * mm, "mid": v(-75.34, 401.5) * mm, "end": v(-73.93, 400.92) * mm});
            skPoint(sketch, "E126.visualSharp", {"position": v(-63.23, 400.92) * mm});
            skArc(sketch, "E126.filletArc", {"start": v(-65.23, 400.92) * mm, "mid": v(-63.81, 401.5) * mm, "end": v(-63.23, 402.92) * mm});
            skLineSegment(sketch, "E127.bottom", {"start": v(-144.93, 400.92) * mm, "end": v(-153.63, 400.92) * mm});
            skLineSegment(sketch, "E127.top", {"start": v(-144.93, 413.62) * mm, "end": v(-153.63, 413.62) * mm});
            skLineSegment(sketch, "E127.left", {"start": v(-142.93, 402.92) * mm, "end": v(-142.93, 411.62) * mm});
            skLineSegment(sketch, "E127.right", {"start": v(-155.63, 402.92) * mm, "end": v(-155.63, 411.62) * mm});
            skLineSegment(sketch, "E128.0", {"start": v(-143.93, 412.62) * mm, "end": v(-154.63, 412.62) * mm});
            skLineSegment(sketch, "E128.1", {"start": v(-143.93, 401.92) * mm, "end": v(-143.93, 412.62) * mm});
            skLineSegment(sketch, "E128.2", {"start": v(-143.93, 401.92) * mm, "end": v(-154.63, 401.92) * mm});
            skLineSegment(sketch, "E128.3", {"start": v(-154.63, 401.92) * mm, "end": v(-154.63, 412.62) * mm});
            skPoint(sketch, "E129.visualSharp", {"position": v(-155.63, 413.62) * mm});
            skArc(sketch, "E129.filletArc", {"start": v(-153.63, 413.62) * mm, "mid": v(-155.04, 413.03) * mm, "end": v(-155.63, 411.62) * mm});
            skPoint(sketch, "E130.visualSharp", {"position": v(-142.93, 413.62) * mm});
            skArc(sketch, "E130.filletArc", {"start": v(-142.93, 411.62) * mm, "mid": v(-143.51, 413.03) * mm, "end": v(-144.93, 413.62) * mm});
            skPoint(sketch, "E131.visualSharp", {"position": v(-155.63, 400.92) * mm});
            skArc(sketch, "E131.filletArc", {"start": v(-155.63, 402.92) * mm, "mid": v(-155.04, 401.5) * mm, "end": v(-153.63, 400.92) * mm});
            skPoint(sketch, "E132.visualSharp", {"position": v(-142.93, 400.92) * mm});
            skArc(sketch, "E132.filletArc", {"start": v(-144.93, 400.92) * mm, "mid": v(-143.51, 401.5) * mm, "end": v(-142.93, 402.92) * mm});
            skLineSegment(sketch, "E133.bottom", {"start": v(-280.63, 400.92) * mm, "end": v(-289.33, 400.92) * mm});
            skLineSegment(sketch, "E133.top", {"start": v(-280.63, 413.62) * mm, "end": v(-289.33, 413.62) * mm});
            skLineSegment(sketch, "E133.left", {"start": v(-278.63, 402.92) * mm, "end": v(-278.63, 411.62) * mm});
            skLineSegment(sketch, "E133.right", {"start": v(-291.33, 402.92) * mm, "end": v(-291.33, 411.62) * mm});
            skLineSegment(sketch, "E134.0", {"start": v(-290.33, 401.92) * mm, "end": v(-290.33, 412.62) * mm});
            skLineSegment(sketch, "E134.1", {"start": v(-279.63, 401.92) * mm, "end": v(-290.33, 401.92) * mm});
            skLineSegment(sketch, "E134.2", {"start": v(-279.63, 401.92) * mm, "end": v(-279.63, 412.62) * mm});
            skLineSegment(sketch, "E134.3", {"start": v(-279.63, 412.62) * mm, "end": v(-290.33, 412.62) * mm});
            skPoint(sketch, "E135.visualSharp", {"position": v(-291.33, 413.62) * mm});
            skArc(sketch, "E135.filletArc", {"start": v(-289.33, 413.62) * mm, "mid": v(-290.74, 413.03) * mm, "end": v(-291.33, 411.62) * mm});
            skPoint(sketch, "E136.visualSharp", {"position": v(-278.63, 413.62) * mm});
            skArc(sketch, "E136.filletArc", {"start": v(-278.63, 411.62) * mm, "mid": v(-279.21, 413.03) * mm, "end": v(-280.63, 413.62) * mm});
            skPoint(sketch, "E137.visualSharp", {"position": v(-291.33, 400.92) * mm});
            skArc(sketch, "E137.filletArc", {"start": v(-291.33, 402.92) * mm, "mid": v(-290.74, 401.5) * mm, "end": v(-289.33, 400.92) * mm});
            skPoint(sketch, "E138.visualSharp", {"position": v(-278.63, 400.92) * mm});
            skArc(sketch, "E138.filletArc", {"start": v(-280.63, 400.92) * mm, "mid": v(-279.21, 401.5) * mm, "end": v(-278.63, 402.92) * mm});
            skLineSegment(sketch, "E139", {"start": v(275.17, 400.92) * mm, "end": v(152.17, 400.92) * mm, "construction": true});
            skLineSegment(sketch, "E140", {"start": v(139.47, 400.92) * mm, "end": v(72.47, 400.92) * mm, "construction": true});
            skLineSegment(sketch, "E141", {"start": v(59.77, 400.92) * mm, "end": v(-63.23, 400.92) * mm, "construction": true});
            skLineSegment(sketch, "E142", {"start": v(-75.93, 400.92) * mm, "end": v(-142.93, 400.92) * mm, "construction": true});
            skLineSegment(sketch, "E143", {"start": v(-278.63, 400.92) * mm, "end": v(-155.63, 400.92) * mm, "construction": true});
            skLineSegment(sketch, "E144", {"start": v(-291.33, 250.6) * mm, "end": v(-291.33, 171.3) * mm, "construction": true});
            skLineSegment(sketch, "E145", {"start": v(-354.23, 0) * mm, "end": v(-354.23, 171.3) * mm, "construction": true});
            skLineSegment(sketch, "E146.bottom", {"start": v(-354.23, 171.3) * mm, "end": v(350.77, 171.3) * mm});
            skLineSegment(sketch, "E146.top", {"start": v(-354.23, 191.3) * mm, "end": v(350.77, 191.3) * mm});
            skLineSegment(sketch, "E146.left", {"start": v(-354.23, 171.3) * mm, "end": v(-354.23, 191.3) * mm});
            skLineSegment(sketch, "E146.right", {"start": v(350.77, 171.3) * mm, "end": v(350.77, 191.3) * mm});
            skLineSegment(sketch, "E147", {"start": v(-354.23, 171.3) * mm, "end": v(-354.23, 342.6) * mm, "construction": true});
            skLineSegment(sketch, "E148.bottom", {"start": v(-354.23, 342.6) * mm, "end": v(350.77, 342.6) * mm});
            skLineSegment(sketch, "E148.top", {"start": v(-354.23, 362.6) * mm, "end": v(350.77, 362.6) * mm});
            skLineSegment(sketch, "E148.left", {"start": v(-354.23, 342.6) * mm, "end": v(-354.23, 362.6) * mm});
            skLineSegment(sketch, "E148.right", {"start": v(350.77, 342.6) * mm, "end": v(350.77, 362.6) * mm});
            skSolve(sketch);
        }
        {
            var Q0;
            Q0 = qSketchRegion(id + "F10", true);
            extrude(context, id + "F11", {"entities" : qUnion([Q0]), "oppositeDirection" : true, "depth" : 840 * mm});
        }
        {
            var Q0;
            Q0=makeQuery(id+"F11.opExtrude","SWEPT_FACE",FACE,{"disambiguationData":[OSD([sQuery(id+"F10.wireOp",EDGE,"E42.bottom")])]});
            var sketch = newSketch(context, id + "F12", { "sketchPlane" : qUnion([Q0])});
            skLineSegment(sketch, "E149", {"start": v(-587.5, -280.63) * mm, "end": v(-417.5, -280.63) * mm});
            skLineSegment(sketch, "E150", {"start": v(-417.5, -280.63) * mm, "end": v(-417.5, -217.13) * mm});
            skCircle(sketch, "E151", {"center": v(-417.5, -217.13) * mm, "radius": 20 * mm});
            skCircle(sketch, "E152", {"center": v(-417.5, -217.13) * mm, "radius": 57.5 * mm});
            skLineSegment(sketch, "E153.bottom", {"start": v(-361.5, -277.13) * mm, "end": v(-473.5, -277.13) * mm});
            skLineSegment(sketch, "E153.top", {"start": v(-361.5, -157.13) * mm, "end": v(-473.5, -157.13) * mm});
            skLineSegment(sketch, "E153.left", {"start": v(-357.5, -273.13) * mm, "end": v(-357.5, -161.13) * mm});
            skLineSegment(sketch, "E153.right", {"start": v(-477.5, -273.13) * mm, "end": v(-477.5, -161.13) * mm});
            skPoint(sketch, "E154.visualSharp", {"position": v(-477.5, -157.13) * mm});
            skArc(sketch, "E154.filletArc", {"start": v(-473.5, -157.13) * mm, "mid": v(-476.33, -158.3) * mm, "end": v(-477.5, -161.13) * mm});
            skPoint(sketch, "E155.visualSharp", {"position": v(-357.5, -157.13) * mm});
            skArc(sketch, "E155.filletArc", {"start": v(-357.5, -161.13) * mm, "mid": v(-358.67, -158.3) * mm, "end": v(-361.5, -157.13) * mm});
            skPoint(sketch, "E156.visualSharp", {"position": v(-477.5, -277.13) * mm});
            skArc(sketch, "E156.filletArc", {"start": v(-477.5, -273.13) * mm, "mid": v(-476.33, -275.96) * mm, "end": v(-473.5, -277.13) * mm});
            skPoint(sketch, "E157.visualSharp", {"position": v(-357.5, -277.13) * mm});
            skArc(sketch, "E157.filletArc", {"start": v(-361.5, -277.13) * mm, "mid": v(-358.67, -275.96) * mm, "end": v(-357.5, -273.13) * mm});
            skCircle(sketch, "E158", {"center": v(-363, -271.13) * mm, "radius": 2.5 * mm});
            skCircle(sketch, "E159", {"center": v(-471.85, -271.25) * mm, "radius": 2.5 * mm});
            skCircle(sketch, "E160", {"center": v(-471.61, -162.77) * mm, "radius": 2.5 * mm});
            skCircle(sketch, "E161", {"center": v(-362.7, -163.32) * mm, "radius": 2.5 * mm});
            skLineSegment(sketch, "E162", {"start": v(-417.5, -217.13) * mm, "end": v(-167.5, -217.13) * mm, "construction": true});
            skCircle(sketch, "E163", {"center": v(-167.5, -217.13) * mm, "radius": 20 * mm});
            skCircle(sketch, "E164", {"center": v(-167.5, -217.13) * mm, "radius": 57.5 * mm});
            skLineSegment(sketch, "E165.bottom", {"start": v(-111.5, -277.13) * mm, "end": v(-223.5, -277.13) * mm});
            skLineSegment(sketch, "E165.left", {"start": v(-107.5, -273.13) * mm, "end": v(-107.5, -161.13) * mm});
            skLineSegment(sketch, "E165.right", {"start": v(-227.5, -273.13) * mm, "end": v(-227.5, -161.13) * mm});
            skPoint(sketch, "E166.visualSharp", {"position": v(-227.5, -157.13) * mm});
            skArc(sketch, "E166.filletArc", {"start": v(-223.5, -157.13) * mm, "mid": v(-226.33, -158.3) * mm, "end": v(-227.5, -161.13) * mm});
            skPoint(sketch, "E167.visualSharp", {"position": v(-107.5, -157.13) * mm});
            skArc(sketch, "E167.filletArc", {"start": v(-107.5, -161.13) * mm, "mid": v(-108.67, -158.3) * mm, "end": v(-111.5, -157.13) * mm});
            skPoint(sketch, "E168.visualSharp", {"position": v(-227.5, -277.13) * mm});
            skArc(sketch, "E168.filletArc", {"start": v(-227.5, -273.13) * mm, "mid": v(-226.33, -275.96) * mm, "end": v(-223.5, -277.13) * mm});
            skPoint(sketch, "E169.visualSharp", {"position": v(-107.5, -277.13) * mm});
            skArc(sketch, "E169.filletArc", {"start": v(-111.5, -277.13) * mm, "mid": v(-108.67, -275.96) * mm, "end": v(-107.5, -273.13) * mm});
            skCircle(sketch, "E170", {"center": v(-113, -271.13) * mm, "radius": 2.5 * mm});
            skCircle(sketch, "E171", {"center": v(-221.85, -271.25) * mm, "radius": 2.5 * mm});
            skCircle(sketch, "E172", {"center": v(-221.61, -162.77) * mm, "radius": 2.5 * mm});
            skCircle(sketch, "E173", {"center": v(-112.7, -163.32) * mm, "radius": 2.5 * mm});
            skLineSegment(sketch, "E174", {"start": v(-167.5, -217.13) * mm, "end": v(82.5, -217.13) * mm, "construction": true});
            skCircle(sketch, "E175", {"center": v(82.5, -217.13) * mm, "radius": 20 * mm});
            skCircle(sketch, "E176", {"center": v(82.5, -217.13) * mm, "radius": 57.5 * mm});
            skLineSegment(sketch, "E177.bottom", {"start": v(138.5, -277.13) * mm, "end": v(26.5, -277.13) * mm});
            skLineSegment(sketch, "E177.left", {"start": v(142.5, -273.13) * mm, "end": v(142.5, -161.13) * mm});
            skLineSegment(sketch, "E177.right", {"start": v(22.5, -273.13) * mm, "end": v(22.5, -161.13) * mm});
            skPoint(sketch, "E178.visualSharp", {"position": v(22.5, -157.13) * mm});
            skArc(sketch, "E178.filletArc", {"start": v(26.5, -157.13) * mm, "mid": v(23.67, -158.3) * mm, "end": v(22.5, -161.13) * mm});
            skPoint(sketch, "E179.visualSharp", {"position": v(142.5, -157.13) * mm});
            skArc(sketch, "E179.filletArc", {"start": v(142.5, -161.13) * mm, "mid": v(141.33, -158.3) * mm, "end": v(138.5, -157.13) * mm});
            skPoint(sketch, "E180.visualSharp", {"position": v(22.5, -277.13) * mm});
            skArc(sketch, "E180.filletArc", {"start": v(22.5, -273.13) * mm, "mid": v(23.67, -275.96) * mm, "end": v(26.5, -277.13) * mm});
            skPoint(sketch, "E181.visualSharp", {"position": v(142.5, -277.13) * mm});
            skArc(sketch, "E181.filletArc", {"start": v(138.5, -277.13) * mm, "mid": v(141.33, -275.96) * mm, "end": v(142.5, -273.13) * mm});
            skCircle(sketch, "E182", {"center": v(137, -271.13) * mm, "radius": 2.5 * mm});
            skCircle(sketch, "E183", {"center": v(28.15, -271.25) * mm, "radius": 2.5 * mm});
            skCircle(sketch, "E184", {"center": v(28.39, -162.77) * mm, "radius": 2.5 * mm});
            skCircle(sketch, "E185", {"center": v(137.3, -163.32) * mm, "radius": 2.5 * mm});
            skLineSegment(sketch, "E186", {"start": v(-223.5, -157.13) * mm, "end": v(-111.5, -157.13) * mm});
            skLineSegment(sketch, "E187", {"start": v(26.5, -157.13) * mm, "end": v(138.5, -157.13) * mm});
            skLineSegment(sketch, "E188", {"start": v(-587.5, -65.23) * mm, "end": v(-417.5, -65.23) * mm});
            skLineSegment(sketch, "E189", {"start": v(-417.5, -65.23) * mm, "end": v(-417.5, -1.73) * mm});
            skCircle(sketch, "E190", {"center": v(-417.5, -1.73) * mm, "radius": 20 * mm});
            skCircle(sketch, "E191", {"center": v(-417.5, -1.73) * mm, "radius": 57.5 * mm});
            skLineSegment(sketch, "E192.bottom", {"start": v(-361.5, -61.73) * mm, "end": v(-473.5, -61.73) * mm});
            skLineSegment(sketch, "E192.top", {"start": v(-361.5, 58.27) * mm, "end": v(-473.5, 58.27) * mm});
            skLineSegment(sketch, "E192.left", {"start": v(-357.5, -57.73) * mm, "end": v(-357.5, 54.27) * mm});
            skLineSegment(sketch, "E192.right", {"start": v(-477.5, -57.73) * mm, "end": v(-477.5, 54.27) * mm});
            skPoint(sketch, "E193.visualSharp", {"position": v(-477.5, 58.27) * mm});
            skArc(sketch, "E193.filletArc", {"start": v(-473.5, 58.27) * mm, "mid": v(-476.33, 57.1) * mm, "end": v(-477.5, 54.27) * mm});
            skPoint(sketch, "E194.visualSharp", {"position": v(-357.5, 58.27) * mm});
            skArc(sketch, "E194.filletArc", {"start": v(-357.5, 54.27) * mm, "mid": v(-358.67, 57.1) * mm, "end": v(-361.5, 58.27) * mm});
            skPoint(sketch, "E195.visualSharp", {"position": v(-477.5, -61.73) * mm});
            skArc(sketch, "E195.filletArc", {"start": v(-477.5, -57.73) * mm, "mid": v(-476.33, -60.56) * mm, "end": v(-473.5, -61.73) * mm});
            skPoint(sketch, "E196.visualSharp", {"position": v(-357.5, -61.73) * mm});
            skArc(sketch, "E196.filletArc", {"start": v(-361.5, -61.73) * mm, "mid": v(-358.67, -60.56) * mm, "end": v(-357.5, -57.73) * mm});
            skCircle(sketch, "E197", {"center": v(-363, -55.73) * mm, "radius": 2.5 * mm});
            skCircle(sketch, "E198", {"center": v(-471.85, -55.85) * mm, "radius": 2.5 * mm});
            skCircle(sketch, "E199", {"center": v(-471.61, 52.63) * mm, "radius": 2.5 * mm});
            skCircle(sketch, "E200", {"center": v(-362.7, 52.08) * mm, "radius": 2.5 * mm});
            skLineSegment(sketch, "E201", {"start": v(-417.5, -1.73) * mm, "end": v(-167.5, -1.73) * mm, "construction": true});
            skCircle(sketch, "E202", {"center": v(-167.5, -1.73) * mm, "radius": 20 * mm});
            skCircle(sketch, "E203", {"center": v(-167.5, -1.73) * mm, "radius": 57.5 * mm});
            skLineSegment(sketch, "E204.bottom", {"start": v(-111.5, -61.73) * mm, "end": v(-223.5, -61.73) * mm});
            skLineSegment(sketch, "E204.left", {"start": v(-107.5, -57.73) * mm, "end": v(-107.5, 54.27) * mm});
            skLineSegment(sketch, "E204.right", {"start": v(-227.5, -57.73) * mm, "end": v(-227.5, 54.27) * mm});
            skPoint(sketch, "E205.visualSharp", {"position": v(-227.5, 58.27) * mm});
            skArc(sketch, "E205.filletArc", {"start": v(-223.5, 58.27) * mm, "mid": v(-226.33, 57.1) * mm, "end": v(-227.5, 54.27) * mm});
            skPoint(sketch, "E206.visualSharp", {"position": v(-107.5, 58.27) * mm});
            skArc(sketch, "E206.filletArc", {"start": v(-107.5, 54.27) * mm, "mid": v(-108.67, 57.1) * mm, "end": v(-111.5, 58.27) * mm});
            skPoint(sketch, "E207.visualSharp", {"position": v(-227.5, -61.73) * mm});
            skArc(sketch, "E207.filletArc", {"start": v(-227.5, -57.73) * mm, "mid": v(-226.33, -60.56) * mm, "end": v(-223.5, -61.73) * mm});
            skPoint(sketch, "E208.visualSharp", {"position": v(-107.5, -61.73) * mm});
            skArc(sketch, "E208.filletArc", {"start": v(-111.5, -61.73) * mm, "mid": v(-108.67, -60.56) * mm, "end": v(-107.5, -57.73) * mm});
            skCircle(sketch, "E209", {"center": v(-113, -55.73) * mm, "radius": 2.5 * mm});
            skCircle(sketch, "E210", {"center": v(-221.85, -55.85) * mm, "radius": 2.5 * mm});
            skCircle(sketch, "E211", {"center": v(-221.61, 52.63) * mm, "radius": 2.5 * mm});
            skCircle(sketch, "E212", {"center": v(-112.7, 52.08) * mm, "radius": 2.5 * mm});
            skLineSegment(sketch, "E213", {"start": v(-167.5, -1.73) * mm, "end": v(82.5, -1.73) * mm, "construction": true});
            skCircle(sketch, "E214", {"center": v(82.5, -1.73) * mm, "radius": 20 * mm});
            skCircle(sketch, "E215", {"center": v(82.5, -1.73) * mm, "radius": 57.5 * mm});
            skLineSegment(sketch, "E216.bottom", {"start": v(138.5, -61.73) * mm, "end": v(26.5, -61.73) * mm});
            skLineSegment(sketch, "E216.left", {"start": v(142.5, -57.73) * mm, "end": v(142.5, 54.27) * mm});
            skLineSegment(sketch, "E216.right", {"start": v(22.5, -57.73) * mm, "end": v(22.5, 54.27) * mm});
            skPoint(sketch, "E217.visualSharp", {"position": v(22.5, 58.27) * mm});
            skArc(sketch, "E217.filletArc", {"start": v(26.5, 58.27) * mm, "mid": v(23.67, 57.1) * mm, "end": v(22.5, 54.27) * mm});
            skPoint(sketch, "E218.visualSharp", {"position": v(142.5, 58.27) * mm});
            skArc(sketch, "E218.filletArc", {"start": v(142.5, 54.27) * mm, "mid": v(141.33, 57.1) * mm, "end": v(138.5, 58.27) * mm});
            skPoint(sketch, "E219.visualSharp", {"position": v(22.5, -61.73) * mm});
            skArc(sketch, "E219.filletArc", {"start": v(22.5, -57.73) * mm, "mid": v(23.67, -60.56) * mm, "end": v(26.5, -61.73) * mm});
            skPoint(sketch, "E220.visualSharp", {"position": v(142.5, -61.73) * mm});
            skArc(sketch, "E220.filletArc", {"start": v(138.5, -61.73) * mm, "mid": v(141.33, -60.56) * mm, "end": v(142.5, -57.73) * mm});
            skCircle(sketch, "E221", {"center": v(137, -55.73) * mm, "radius": 2.5 * mm});
            skCircle(sketch, "E222", {"center": v(28.15, -55.85) * mm, "radius": 2.5 * mm});
            skCircle(sketch, "E223", {"center": v(28.39, 52.63) * mm, "radius": 2.5 * mm});
            skCircle(sketch, "E224", {"center": v(137.3, 52.08) * mm, "radius": 2.5 * mm});
            skLineSegment(sketch, "E225", {"start": v(-223.5, 58.27) * mm, "end": v(-111.5, 58.27) * mm});
            skLineSegment(sketch, "E226", {"start": v(26.5, 58.27) * mm, "end": v(138.5, 58.27) * mm});
            skLineSegment(sketch, "E227", {"start": v(-587.5, 150.17) * mm, "end": v(-417.5, 150.17) * mm});
            skLineSegment(sketch, "E228", {"start": v(-417.5, 150.17) * mm, "end": v(-417.5, 213.67) * mm});
            skCircle(sketch, "E229", {"center": v(-417.5, 213.67) * mm, "radius": 20 * mm});
            skCircle(sketch, "E230", {"center": v(-417.5, 213.67) * mm, "radius": 57.5 * mm});
            skLineSegment(sketch, "E231.bottom", {"start": v(-361.5, 153.67) * mm, "end": v(-473.5, 153.67) * mm});
            skLineSegment(sketch, "E231.top", {"start": v(-361.5, 273.67) * mm, "end": v(-473.5, 273.67) * mm});
            skLineSegment(sketch, "E231.left", {"start": v(-357.5, 157.67) * mm, "end": v(-357.5, 269.67) * mm});
            skLineSegment(sketch, "E231.right", {"start": v(-477.5, 157.67) * mm, "end": v(-477.5, 269.67) * mm});
            skPoint(sketch, "E232.visualSharp", {"position": v(-477.5, 273.67) * mm});
            skArc(sketch, "E232.filletArc", {"start": v(-473.5, 273.67) * mm, "mid": v(-476.33, 272.5) * mm, "end": v(-477.5, 269.67) * mm});
            skPoint(sketch, "E233.visualSharp", {"position": v(-357.5, 273.67) * mm});
            skArc(sketch, "E233.filletArc", {"start": v(-357.5, 269.67) * mm, "mid": v(-358.67, 272.5) * mm, "end": v(-361.5, 273.67) * mm});
            skPoint(sketch, "E234.visualSharp", {"position": v(-477.5, 153.67) * mm});
            skArc(sketch, "E234.filletArc", {"start": v(-477.5, 157.67) * mm, "mid": v(-476.33, 154.84) * mm, "end": v(-473.5, 153.67) * mm});
            skPoint(sketch, "E235.visualSharp", {"position": v(-357.5, 153.67) * mm});
            skArc(sketch, "E235.filletArc", {"start": v(-361.5, 153.67) * mm, "mid": v(-358.67, 154.84) * mm, "end": v(-357.5, 157.67) * mm});
            skCircle(sketch, "E236", {"center": v(-363, 159.67) * mm, "radius": 2.5 * mm});
            skCircle(sketch, "E237", {"center": v(-471.85, 159.55) * mm, "radius": 2.5 * mm});
            skCircle(sketch, "E238", {"center": v(-471.61, 268.03) * mm, "radius": 2.5 * mm});
            skCircle(sketch, "E239", {"center": v(-362.7, 267.48) * mm, "radius": 2.5 * mm});
            skLineSegment(sketch, "E240", {"start": v(-417.5, 213.67) * mm, "end": v(-167.5, 213.67) * mm, "construction": true});
            skCircle(sketch, "E241", {"center": v(-167.5, 213.67) * mm, "radius": 20 * mm});
            skCircle(sketch, "E242", {"center": v(-167.5, 213.67) * mm, "radius": 57.5 * mm});
            skLineSegment(sketch, "E243.bottom", {"start": v(-111.5, 153.67) * mm, "end": v(-223.5, 153.67) * mm});
            skLineSegment(sketch, "E243.left", {"start": v(-107.5, 157.67) * mm, "end": v(-107.5, 269.67) * mm});
            skLineSegment(sketch, "E243.right", {"start": v(-227.5, 157.67) * mm, "end": v(-227.5, 269.67) * mm});
            skPoint(sketch, "E244.visualSharp", {"position": v(-227.5, 273.67) * mm});
            skArc(sketch, "E244.filletArc", {"start": v(-223.5, 273.67) * mm, "mid": v(-226.33, 272.5) * mm, "end": v(-227.5, 269.67) * mm});
            skPoint(sketch, "E245.visualSharp", {"position": v(-107.5, 273.67) * mm});
            skArc(sketch, "E245.filletArc", {"start": v(-107.5, 269.67) * mm, "mid": v(-108.67, 272.5) * mm, "end": v(-111.5, 273.67) * mm});
            skPoint(sketch, "E246.visualSharp", {"position": v(-227.5, 153.67) * mm});
            skArc(sketch, "E246.filletArc", {"start": v(-227.5, 157.67) * mm, "mid": v(-226.33, 154.84) * mm, "end": v(-223.5, 153.67) * mm});
            skPoint(sketch, "E247.visualSharp", {"position": v(-107.5, 153.67) * mm});
            skArc(sketch, "E247.filletArc", {"start": v(-111.5, 153.67) * mm, "mid": v(-108.67, 154.84) * mm, "end": v(-107.5, 157.67) * mm});
            skCircle(sketch, "E248", {"center": v(-113, 159.67) * mm, "radius": 2.5 * mm});
            skCircle(sketch, "E249", {"center": v(-221.85, 159.55) * mm, "radius": 2.5 * mm});
            skCircle(sketch, "E250", {"center": v(-221.61, 268.03) * mm, "radius": 2.5 * mm});
            skCircle(sketch, "E251", {"center": v(-112.7, 267.48) * mm, "radius": 2.5 * mm});
            skLineSegment(sketch, "E252", {"start": v(-167.5, 213.67) * mm, "end": v(82.5, 213.67) * mm, "construction": true});
            skCircle(sketch, "E253", {"center": v(82.5, 213.67) * mm, "radius": 20 * mm});
            skCircle(sketch, "E254", {"center": v(82.5, 213.67) * mm, "radius": 57.5 * mm});
            skLineSegment(sketch, "E255.bottom", {"start": v(138.5, 153.67) * mm, "end": v(26.5, 153.67) * mm});
            skLineSegment(sketch, "E255.left", {"start": v(142.5, 157.67) * mm, "end": v(142.5, 269.67) * mm});
            skLineSegment(sketch, "E255.right", {"start": v(22.5, 157.67) * mm, "end": v(22.5, 269.67) * mm});
            skPoint(sketch, "E256.visualSharp", {"position": v(22.5, 273.67) * mm});
            skArc(sketch, "E256.filletArc", {"start": v(26.5, 273.67) * mm, "mid": v(23.67, 272.5) * mm, "end": v(22.5, 269.67) * mm});
            skPoint(sketch, "E257.visualSharp", {"position": v(142.5, 273.67) * mm});
            skArc(sketch, "E257.filletArc", {"start": v(142.5, 269.67) * mm, "mid": v(141.33, 272.5) * mm, "end": v(138.5, 273.67) * mm});
            skPoint(sketch, "E258.visualSharp", {"position": v(22.5, 153.67) * mm});
            skArc(sketch, "E258.filletArc", {"start": v(22.5, 157.67) * mm, "mid": v(23.67, 154.84) * mm, "end": v(26.5, 153.67) * mm});
            skPoint(sketch, "E259.visualSharp", {"position": v(142.5, 153.67) * mm});
            skArc(sketch, "E259.filletArc", {"start": v(138.5, 153.67) * mm, "mid": v(141.33, 154.84) * mm, "end": v(142.5, 157.67) * mm});
            skCircle(sketch, "E260", {"center": v(137, 159.67) * mm, "radius": 2.5 * mm});
            skCircle(sketch, "E261", {"center": v(28.15, 159.55) * mm, "radius": 2.5 * mm});
            skCircle(sketch, "E262", {"center": v(28.39, 268.03) * mm, "radius": 2.5 * mm});
            skCircle(sketch, "E263", {"center": v(137.3, 267.48) * mm, "radius": 2.5 * mm});
            skLineSegment(sketch, "E264", {"start": v(-223.5, 273.67) * mm, "end": v(-111.5, 273.67) * mm});
            skLineSegment(sketch, "E265", {"start": v(26.5, 273.67) * mm, "end": v(138.5, 273.67) * mm});
            skSolve(sketch);
        }
        {
            var Q0;
            Q0=makeQuery(id+"F12.imprint","IMPRINT",FACE,{"disambiguationData":[TD([[makeQuery(id+"F12.imprint","IMPRINT",EDGE,{"derivedFrom":sQuery(id+"F12.wireOp",EDGE,"E151")}),1.0]])]});
            var Q1;
            Q1=sQuery(id+"F12.wireOp",EDGE,"E151");
            extrude(context, id + "F13", {"entities" : qUnion([Q0]), "surfaceEntities" : qUnion([Q1]), "oppositeDirection" : true, "depth" : 38 * mm});
        }
        {
            var Q0;
            Q0=makeQuery(id+"F13.opExtrude","CAP_EDGE",EDGE,{"disambiguationData":[OSD([sQuery(id+"F12.wireOp",EDGE,"E151")])],"isStart":true});
            fillet(context, id + "F14", {"entities" : qUnion([Q0]), "radius" : 3 * mm, "tangentPropagation" : true, "allowEdgeOverflow" : false});
        }
        {
            var Q0;
            Q0=sQuery(id+"F12.wireOp",EDGE,"E152");
            extrude(context, id + "F15", {"bodyType" : ToolBodyType.SURFACE, "surfaceEntities" : qUnion([Q0]), "oppositeDirection" : true, "depth" : 38 * mm});
        }
        {
            var Q0;
            Q0=makeQuery(id+"F12.imprint","IMPRINT",FACE,{"disambiguationData":[TD([[makeQuery(id+"F12.imprint","IMPRINT",EDGE,{"derivedFrom":sQuery(id+"F12.wireOp",EDGE,"E152")}),-1.0]])]});
            extrude(context, id + "F16", {"entities" : qUnion([Q0]), "oppositeDirection" : true, "depth" : 5 * mm});
        }
        {
            var Q0;
            Q0=makeQuery(id+"F16.opExtrude","CAP_EDGE",EDGE,{"disambiguationData":[OSD([sQuery(id+"F12.wireOp",EDGE,"E152")])],"isStart":true});
            fillet(context, id + "F17", {"entities" : qUnion([Q0]), "radius" : 1 * mm, "tangentPropagation" : true, "allowEdgeOverflow" : false});
        }
        {
            var Q0;
            Q0=makeQuery(id+"F13.opExtrude","CAP_FACE",FACE,{"disambiguationData":[OSD([sQuery(id+"F12.wireOp",EDGE,"E151")])],"isStart":false});
            var sketch = newSketch(context, id + "F18", { "sketchPlane" : qUnion([Q0])});
            skLineSegment(sketch, "E266.bottom", {"start": v(-361.5, 157.13) * mm, "end": v(-473.5, 157.13) * mm});
            skLineSegment(sketch, "E266.top", {"start": v(-361.5, 277.13) * mm, "end": v(-473.5, 277.13) * mm});
            skLineSegment(sketch, "E266.left", {"start": v(-357.5, 161.13) * mm, "end": v(-357.5, 273.13) * mm});
            skLineSegment(sketch, "E266.right", {"start": v(-477.5, 161.13) * mm, "end": v(-477.5, 273.13) * mm});
            skPoint(sketch, "E266.middle", {"position": v(-417.5, 217.13) * mm});
            skCircle(sketch, "E267", {"center": v(-417.5, 217.13) * mm, "radius": 57.5 * mm});
            skPoint(sketch, "E268.visualSharp", {"position": v(-477.5, 277.13) * mm});
            skArc(sketch, "E268.filletArc", {"start": v(-473.5, 277.13) * mm, "mid": v(-476.33, 275.96) * mm, "end": v(-477.5, 273.13) * mm});
            skPoint(sketch, "E269.visualSharp", {"position": v(-357.5, 277.13) * mm});
            skArc(sketch, "E269.filletArc", {"start": v(-357.5, 273.13) * mm, "mid": v(-358.67, 275.96) * mm, "end": v(-361.5, 277.13) * mm});
            skPoint(sketch, "E270.visualSharp", {"position": v(-357.5, 157.13) * mm});
            skArc(sketch, "E270.filletArc", {"start": v(-361.5, 157.13) * mm, "mid": v(-358.67, 158.3) * mm, "end": v(-357.5, 161.13) * mm});
            skPoint(sketch, "E271.visualSharp", {"position": v(-477.5, 157.13) * mm});
            skArc(sketch, "E271.filletArc", {"start": v(-477.5, 161.13) * mm, "mid": v(-476.33, 158.3) * mm, "end": v(-473.5, 157.13) * mm});
            skCircle(sketch, "E272", {"center": v(-471.87, 163.03) * mm, "radius": 2.5 * mm});
            skCircle(sketch, "E273", {"center": v(-362.45, 163.44) * mm, "radius": 2.5 * mm});
            skCircle(sketch, "E274", {"center": v(-363.42, 271.53) * mm, "radius": 2.5 * mm});
            skCircle(sketch, "E275", {"center": v(-471.98, 271.14) * mm, "radius": 2.5 * mm});
            skLineSegment(sketch, "E276", {"start": v(-417.5, 217.13) * mm, "end": v(-167.5, 217.13) * mm, "construction": true});
            skLineSegment(sketch, "E277.bottom", {"start": v(-111.5, 157.13) * mm, "end": v(-223.5, 157.13) * mm});
            skLineSegment(sketch, "E277.top", {"start": v(-111.5, 277.13) * mm, "end": v(-223.5, 277.13) * mm});
            skLineSegment(sketch, "E277.left", {"start": v(-107.5, 161.13) * mm, "end": v(-107.5, 273.13) * mm});
            skLineSegment(sketch, "E277.right", {"start": v(-227.5, 161.13) * mm, "end": v(-227.5, 273.13) * mm});
            skPoint(sketch, "E277.middle", {"position": v(-167.5, 217.13) * mm});
            skCircle(sketch, "E278", {"center": v(-167.5, 217.13) * mm, "radius": 57.5 * mm});
            skPoint(sketch, "E279.visualSharp", {"position": v(-227.5, 277.13) * mm});
            skArc(sketch, "E279.filletArc", {"start": v(-223.5, 277.13) * mm, "mid": v(-226.33, 275.96) * mm, "end": v(-227.5, 273.13) * mm});
            skPoint(sketch, "E280.visualSharp", {"position": v(-107.5, 277.13) * mm});
            skArc(sketch, "E280.filletArc", {"start": v(-107.5, 273.13) * mm, "mid": v(-108.67, 275.96) * mm, "end": v(-111.5, 277.13) * mm});
            skPoint(sketch, "E281.visualSharp", {"position": v(-107.5, 157.13) * mm});
            skArc(sketch, "E281.filletArc", {"start": v(-111.5, 157.13) * mm, "mid": v(-108.67, 158.3) * mm, "end": v(-107.5, 161.13) * mm});
            skPoint(sketch, "E282.visualSharp", {"position": v(-227.5, 157.13) * mm});
            skArc(sketch, "E282.filletArc", {"start": v(-227.5, 161.13) * mm, "mid": v(-226.33, 158.3) * mm, "end": v(-223.5, 157.13) * mm});
            skCircle(sketch, "E283", {"center": v(-221.87, 163.03) * mm, "radius": 2.5 * mm});
            skCircle(sketch, "E284", {"center": v(-112.45, 163.44) * mm, "radius": 2.5 * mm});
            skCircle(sketch, "E285", {"center": v(-113.42, 271.53) * mm, "radius": 2.5 * mm});
            skCircle(sketch, "E286", {"center": v(-221.98, 271.14) * mm, "radius": 2.5 * mm});
            skLineSegment(sketch, "E287", {"start": v(-167.5, 217.13) * mm, "end": v(82.5, 217.13) * mm, "construction": true});
            skLineSegment(sketch, "E288.bottom", {"start": v(138.5, 157.13) * mm, "end": v(26.5, 157.13) * mm});
            skLineSegment(sketch, "E288.top", {"start": v(138.5, 277.13) * mm, "end": v(26.5, 277.13) * mm});
            skLineSegment(sketch, "E288.left", {"start": v(142.5, 161.13) * mm, "end": v(142.5, 273.13) * mm});
            skLineSegment(sketch, "E288.right", {"start": v(22.5, 161.13) * mm, "end": v(22.5, 273.13) * mm});
            skPoint(sketch, "E288.middle", {"position": v(82.5, 217.13) * mm});
            skCircle(sketch, "E289", {"center": v(82.5, 217.13) * mm, "radius": 57.5 * mm});
            skPoint(sketch, "E290.visualSharp", {"position": v(22.5, 277.13) * mm});
            skArc(sketch, "E290.filletArc", {"start": v(26.5, 277.13) * mm, "mid": v(23.67, 275.96) * mm, "end": v(22.5, 273.13) * mm});
            skPoint(sketch, "E291.visualSharp", {"position": v(142.5, 277.13) * mm});
            skArc(sketch, "E291.filletArc", {"start": v(142.5, 273.13) * mm, "mid": v(141.33, 275.96) * mm, "end": v(138.5, 277.13) * mm});
            skPoint(sketch, "E292.visualSharp", {"position": v(142.5, 157.13) * mm});
            skArc(sketch, "E292.filletArc", {"start": v(138.5, 157.13) * mm, "mid": v(141.33, 158.3) * mm, "end": v(142.5, 161.13) * mm});
            skPoint(sketch, "E293.visualSharp", {"position": v(22.5, 157.13) * mm});
            skArc(sketch, "E293.filletArc", {"start": v(22.5, 161.13) * mm, "mid": v(23.67, 158.3) * mm, "end": v(26.5, 157.13) * mm});
            skCircle(sketch, "E294", {"center": v(28.13, 163.03) * mm, "radius": 2.5 * mm});
            skCircle(sketch, "E295", {"center": v(137.55, 163.44) * mm, "radius": 2.5 * mm});
            skCircle(sketch, "E296", {"center": v(136.58, 271.53) * mm, "radius": 2.5 * mm});
            skCircle(sketch, "E297", {"center": v(28.02, 271.14) * mm, "radius": 2.5 * mm});
            skLineSegment(sketch, "E298.bottom", {"start": v(-361.5, -58.27) * mm, "end": v(-473.5, -58.27) * mm});
            skLineSegment(sketch, "E298.top", {"start": v(-361.5, 61.73) * mm, "end": v(-473.5, 61.73) * mm});
            skLineSegment(sketch, "E298.left", {"start": v(-357.5, -54.27) * mm, "end": v(-357.5, 57.73) * mm});
            skLineSegment(sketch, "E298.right", {"start": v(-477.5, -54.27) * mm, "end": v(-477.5, 57.73) * mm});
            skPoint(sketch, "E298.middle", {"position": v(-417.5, 1.73) * mm});
            skCircle(sketch, "E299", {"center": v(-417.5, 1.73) * mm, "radius": 57.5 * mm});
            skPoint(sketch, "E300.visualSharp", {"position": v(-477.5, 61.73) * mm});
            skArc(sketch, "E300.filletArc", {"start": v(-473.5, 61.73) * mm, "mid": v(-476.33, 60.56) * mm, "end": v(-477.5, 57.73) * mm});
            skPoint(sketch, "E301.visualSharp", {"position": v(-357.5, 61.73) * mm});
            skArc(sketch, "E301.filletArc", {"start": v(-357.5, 57.73) * mm, "mid": v(-358.67, 60.56) * mm, "end": v(-361.5, 61.73) * mm});
            skPoint(sketch, "E302.visualSharp", {"position": v(-357.5, -58.27) * mm});
            skArc(sketch, "E302.filletArc", {"start": v(-361.5, -58.27) * mm, "mid": v(-358.67, -57.1) * mm, "end": v(-357.5, -54.27) * mm});
            skPoint(sketch, "E303.visualSharp", {"position": v(-477.5, -58.27) * mm});
            skArc(sketch, "E303.filletArc", {"start": v(-477.5, -54.27) * mm, "mid": v(-476.33, -57.1) * mm, "end": v(-473.5, -58.27) * mm});
            skCircle(sketch, "E304", {"center": v(-471.87, -52.37) * mm, "radius": 2.5 * mm});
            skCircle(sketch, "E305", {"center": v(-362.45, -51.96) * mm, "radius": 2.5 * mm});
            skCircle(sketch, "E306", {"center": v(-363.42, 56.13) * mm, "radius": 2.5 * mm});
            skCircle(sketch, "E307", {"center": v(-471.98, 55.74) * mm, "radius": 2.5 * mm});
            skLineSegment(sketch, "E308", {"start": v(-417.5, 1.73) * mm, "end": v(-167.5, 1.73) * mm, "construction": true});
            skLineSegment(sketch, "E309.bottom", {"start": v(-111.5, -58.27) * mm, "end": v(-223.5, -58.27) * mm});
            skLineSegment(sketch, "E309.top", {"start": v(-111.5, 61.73) * mm, "end": v(-223.5, 61.73) * mm});
            skLineSegment(sketch, "E309.left", {"start": v(-107.5, -54.27) * mm, "end": v(-107.5, 57.73) * mm});
            skLineSegment(sketch, "E309.right", {"start": v(-227.5, -54.27) * mm, "end": v(-227.5, 57.73) * mm});
            skPoint(sketch, "E309.middle", {"position": v(-167.5, 1.73) * mm});
            skCircle(sketch, "E310", {"center": v(-167.5, 1.73) * mm, "radius": 57.5 * mm});
            skPoint(sketch, "E311.visualSharp", {"position": v(-227.5, 61.73) * mm});
            skArc(sketch, "E311.filletArc", {"start": v(-223.5, 61.73) * mm, "mid": v(-226.33, 60.56) * mm, "end": v(-227.5, 57.73) * mm});
            skPoint(sketch, "E312.visualSharp", {"position": v(-107.5, 61.73) * mm});
            skArc(sketch, "E312.filletArc", {"start": v(-107.5, 57.73) * mm, "mid": v(-108.67, 60.56) * mm, "end": v(-111.5, 61.73) * mm});
            skPoint(sketch, "E313.visualSharp", {"position": v(-107.5, -58.27) * mm});
            skArc(sketch, "E313.filletArc", {"start": v(-111.5, -58.27) * mm, "mid": v(-108.67, -57.1) * mm, "end": v(-107.5, -54.27) * mm});
            skPoint(sketch, "E314.visualSharp", {"position": v(-227.5, -58.27) * mm});
            skArc(sketch, "E314.filletArc", {"start": v(-227.5, -54.27) * mm, "mid": v(-226.33, -57.1) * mm, "end": v(-223.5, -58.27) * mm});
            skCircle(sketch, "E315", {"center": v(-221.87, -52.37) * mm, "radius": 2.5 * mm});
            skCircle(sketch, "E316", {"center": v(-112.45, -51.96) * mm, "radius": 2.5 * mm});
            skCircle(sketch, "E317", {"center": v(-113.42, 56.13) * mm, "radius": 2.5 * mm});
            skCircle(sketch, "E318", {"center": v(-221.98, 55.74) * mm, "radius": 2.5 * mm});
            skLineSegment(sketch, "E319", {"start": v(-167.5, 1.73) * mm, "end": v(82.5, 1.73) * mm, "construction": true});
            skLineSegment(sketch, "E320.bottom", {"start": v(138.5, -58.27) * mm, "end": v(26.5, -58.27) * mm});
            skLineSegment(sketch, "E320.top", {"start": v(138.5, 61.73) * mm, "end": v(26.5, 61.73) * mm});
            skLineSegment(sketch, "E320.left", {"start": v(142.5, -54.27) * mm, "end": v(142.5, 57.73) * mm});
            skLineSegment(sketch, "E320.right", {"start": v(22.5, -54.27) * mm, "end": v(22.5, 57.73) * mm});
            skPoint(sketch, "E320.middle", {"position": v(82.5, 1.73) * mm});
            skCircle(sketch, "E321", {"center": v(82.5, 1.73) * mm, "radius": 57.5 * mm});
            skPoint(sketch, "E322.visualSharp", {"position": v(22.5, 61.73) * mm});
            skArc(sketch, "E322.filletArc", {"start": v(26.5, 61.73) * mm, "mid": v(23.67, 60.56) * mm, "end": v(22.5, 57.73) * mm});
            skPoint(sketch, "E323.visualSharp", {"position": v(142.5, 61.73) * mm});
            skArc(sketch, "E323.filletArc", {"start": v(142.5, 57.73) * mm, "mid": v(141.33, 60.56) * mm, "end": v(138.5, 61.73) * mm});
            skPoint(sketch, "E324.visualSharp", {"position": v(142.5, -58.27) * mm});
            skArc(sketch, "E324.filletArc", {"start": v(138.5, -58.27) * mm, "mid": v(141.33, -57.1) * mm, "end": v(142.5, -54.27) * mm});
            skPoint(sketch, "E325.visualSharp", {"position": v(22.5, -58.27) * mm});
            skArc(sketch, "E325.filletArc", {"start": v(22.5, -54.27) * mm, "mid": v(23.67, -57.1) * mm, "end": v(26.5, -58.27) * mm});
            skCircle(sketch, "E326", {"center": v(28.13, -52.37) * mm, "radius": 2.5 * mm});
            skCircle(sketch, "E327", {"center": v(137.55, -51.96) * mm, "radius": 2.5 * mm});
            skCircle(sketch, "E328", {"center": v(136.58, 56.13) * mm, "radius": 2.5 * mm});
            skCircle(sketch, "E329", {"center": v(28.02, 55.74) * mm, "radius": 2.5 * mm});
            skLineSegment(sketch, "E330", {"start": v(82.5, 217.13) * mm, "end": v(82.5, 65.23) * mm, "construction": true});
            skLineSegment(sketch, "E331", {"start": v(82.5, 65.23) * mm, "end": v(82.5, 1.73) * mm, "construction": true});
            skLineSegment(sketch, "E332.bottom", {"start": v(-361.5, -273.67) * mm, "end": v(-473.5, -273.67) * mm});
            skLineSegment(sketch, "E332.top", {"start": v(-361.5, -153.67) * mm, "end": v(-473.5, -153.67) * mm});
            skLineSegment(sketch, "E332.left", {"start": v(-357.5, -269.67) * mm, "end": v(-357.5, -157.67) * mm});
            skLineSegment(sketch, "E332.right", {"start": v(-477.5, -269.67) * mm, "end": v(-477.5, -157.67) * mm});
            skPoint(sketch, "E332.middle", {"position": v(-417.5, -213.67) * mm});
            skCircle(sketch, "E333", {"center": v(-417.5, -213.67) * mm, "radius": 57.5 * mm});
            skPoint(sketch, "E334.visualSharp", {"position": v(-477.5, -153.67) * mm});
            skArc(sketch, "E334.filletArc", {"start": v(-473.5, -153.67) * mm, "mid": v(-476.33, -154.84) * mm, "end": v(-477.5, -157.67) * mm});
            skPoint(sketch, "E335.visualSharp", {"position": v(-357.5, -153.67) * mm});
            skArc(sketch, "E335.filletArc", {"start": v(-357.5, -157.67) * mm, "mid": v(-358.67, -154.84) * mm, "end": v(-361.5, -153.67) * mm});
            skPoint(sketch, "E336.visualSharp", {"position": v(-357.5, -273.67) * mm});
            skArc(sketch, "E336.filletArc", {"start": v(-361.5, -273.67) * mm, "mid": v(-358.67, -272.5) * mm, "end": v(-357.5, -269.67) * mm});
            skPoint(sketch, "E337.visualSharp", {"position": v(-477.5, -273.67) * mm});
            skArc(sketch, "E337.filletArc", {"start": v(-477.5, -269.67) * mm, "mid": v(-476.33, -272.5) * mm, "end": v(-473.5, -273.67) * mm});
            skCircle(sketch, "E338", {"center": v(-471.87, -267.77) * mm, "radius": 2.5 * mm});
            skCircle(sketch, "E339", {"center": v(-362.45, -267.36) * mm, "radius": 2.5 * mm});
            skCircle(sketch, "E340", {"center": v(-363.42, -159.27) * mm, "radius": 2.5 * mm});
            skCircle(sketch, "E341", {"center": v(-471.98, -159.66) * mm, "radius": 2.5 * mm});
            skLineSegment(sketch, "E342", {"start": v(-417.5, -213.67) * mm, "end": v(-167.5, -213.67) * mm, "construction": true});
            skLineSegment(sketch, "E343.bottom", {"start": v(-111.5, -273.67) * mm, "end": v(-223.5, -273.67) * mm});
            skLineSegment(sketch, "E343.top", {"start": v(-111.5, -153.67) * mm, "end": v(-223.5, -153.67) * mm});
            skLineSegment(sketch, "E343.left", {"start": v(-107.5, -269.67) * mm, "end": v(-107.5, -157.67) * mm});
            skLineSegment(sketch, "E343.right", {"start": v(-227.5, -269.67) * mm, "end": v(-227.5, -157.67) * mm});
            skPoint(sketch, "E343.middle", {"position": v(-167.5, -213.67) * mm});
            skCircle(sketch, "E344", {"center": v(-167.5, -213.67) * mm, "radius": 57.5 * mm});
            skPoint(sketch, "E345.visualSharp", {"position": v(-227.5, -153.67) * mm});
            skArc(sketch, "E345.filletArc", {"start": v(-223.5, -153.67) * mm, "mid": v(-226.33, -154.84) * mm, "end": v(-227.5, -157.67) * mm});
            skPoint(sketch, "E346.visualSharp", {"position": v(-107.5, -153.67) * mm});
            skArc(sketch, "E346.filletArc", {"start": v(-107.5, -157.67) * mm, "mid": v(-108.67, -154.84) * mm, "end": v(-111.5, -153.67) * mm});
            skPoint(sketch, "E347.visualSharp", {"position": v(-107.5, -273.67) * mm});
            skArc(sketch, "E347.filletArc", {"start": v(-111.5, -273.67) * mm, "mid": v(-108.67, -272.5) * mm, "end": v(-107.5, -269.67) * mm});
            skPoint(sketch, "E348.visualSharp", {"position": v(-227.5, -273.67) * mm});
            skArc(sketch, "E348.filletArc", {"start": v(-227.5, -269.67) * mm, "mid": v(-226.33, -272.5) * mm, "end": v(-223.5, -273.67) * mm});
            skCircle(sketch, "E349", {"center": v(-221.87, -267.77) * mm, "radius": 2.5 * mm});
            skCircle(sketch, "E350", {"center": v(-112.45, -267.36) * mm, "radius": 2.5 * mm});
            skCircle(sketch, "E351", {"center": v(-113.42, -159.27) * mm, "radius": 2.5 * mm});
            skCircle(sketch, "E352", {"center": v(-221.98, -159.66) * mm, "radius": 2.5 * mm});
            skLineSegment(sketch, "E353", {"start": v(-167.5, -213.67) * mm, "end": v(82.5, -213.67) * mm, "construction": true});
            skLineSegment(sketch, "E354.bottom", {"start": v(138.5, -273.67) * mm, "end": v(26.5, -273.67) * mm});
            skLineSegment(sketch, "E354.top", {"start": v(138.5, -153.67) * mm, "end": v(26.5, -153.67) * mm});
            skLineSegment(sketch, "E354.left", {"start": v(142.5, -269.67) * mm, "end": v(142.5, -157.67) * mm});
            skLineSegment(sketch, "E354.right", {"start": v(22.5, -269.67) * mm, "end": v(22.5, -157.67) * mm});
            skPoint(sketch, "E354.middle", {"position": v(82.5, -213.67) * mm});
            skCircle(sketch, "E355", {"center": v(82.5, -213.67) * mm, "radius": 57.5 * mm});
            skPoint(sketch, "E356.visualSharp", {"position": v(22.5, -153.67) * mm});
            skArc(sketch, "E356.filletArc", {"start": v(26.5, -153.67) * mm, "mid": v(23.67, -154.84) * mm, "end": v(22.5, -157.67) * mm});
            skPoint(sketch, "E357.visualSharp", {"position": v(142.5, -153.67) * mm});
            skArc(sketch, "E357.filletArc", {"start": v(142.5, -157.67) * mm, "mid": v(141.33, -154.84) * mm, "end": v(138.5, -153.67) * mm});
            skPoint(sketch, "E358.visualSharp", {"position": v(142.5, -273.67) * mm});
            skArc(sketch, "E358.filletArc", {"start": v(138.5, -273.67) * mm, "mid": v(141.33, -272.5) * mm, "end": v(142.5, -269.67) * mm});
            skPoint(sketch, "E359.visualSharp", {"position": v(22.5, -273.67) * mm});
            skArc(sketch, "E359.filletArc", {"start": v(22.5, -269.67) * mm, "mid": v(23.67, -272.5) * mm, "end": v(26.5, -273.67) * mm});
            skCircle(sketch, "E360", {"center": v(28.13, -267.77) * mm, "radius": 2.5 * mm});
            skCircle(sketch, "E361", {"center": v(137.55, -267.36) * mm, "radius": 2.5 * mm});
            skCircle(sketch, "E362", {"center": v(136.58, -159.27) * mm, "radius": 2.5 * mm});
            skCircle(sketch, "E363", {"center": v(28.02, -159.66) * mm, "radius": 2.5 * mm});
            skLineSegment(sketch, "E364", {"start": v(82.5, 1.73) * mm, "end": v(82.5, -213.67) * mm, "construction": true});
            skSolve(sketch);
        }
        {
            var Q0;
            Q0=makeQuery(id+"F18.imprint","IMPRINT",FACE,{"disambiguationData":[TD([[makeQuery(id+"F18.imprint","IMPRINT",EDGE,{"derivedFrom":sQuery(id+"F18.wireOp",EDGE,"E266.bottom")}),-1.0]])]});
            extrude(context, id + "F19", {"entities" : qUnion([Q0]), "depth" : 5 * mm});
        }
        {
            var Q0;
            Q0=makeQuery(id+"F19.opExtrude","CAP_EDGE",EDGE,{"disambiguationData":[OSD([sQuery(id+"F18.wireOp",EDGE,"E267")])],"isStart":false});
            fillet(context, id + "F20", {"entities" : qUnion([Q0]), "radius" : 1 * mm, "tangentPropagation" : true, "allowEdgeOverflow" : false});
        }
        {
            var Q0;
            Q0=makeQuery(id+"F13.opExtrude","CAP_FACE",FACE,{"disambiguationData":[OSD([sQuery(id+"F12.wireOp",EDGE,"E151")])],"isStart":false});
            fillet(context, id + "F21", {"entities" : qUnion([Q0]), "radius" : 3 * mm, "tangentPropagation" : true, "allowEdgeOverflow" : false});
        }
        {
            var Q0;
            Q0=sQuery(id+"F12.wireOp",EDGE,"E164");
            extrude(context, id + "F22", {"bodyType" : ToolBodyType.SURFACE, "surfaceEntities" : qUnion([Q0]), "oppositeDirection" : true, "depth" : 38 * mm});
        }
        {
            var Q0;
            Q0=makeQuery(id+"F12.imprint","IMPRINT",FACE,{"disambiguationData":[TD([[makeQuery(id+"F12.imprint","IMPRINT",EDGE,{"derivedFrom":sQuery(id+"F12.wireOp",EDGE,"E176")}),-1.0]])]});
            extrude(context, id + "F23", {"entities" : qUnion([Q0]), "oppositeDirection" : true, "depth" : 5 * mm});
        }
        {
            var Q0;
            Q0=sQuery(id+"F12.wireOp",EDGE,"E176");
            extrude(context, id + "F24", {"bodyType" : ToolBodyType.SURFACE, "surfaceEntities" : qUnion([Q0]), "oppositeDirection" : true, "depth" : 38 * mm});
        }
        {
            var Q0;
            Q0=makeQuery(id+"F12.imprint","IMPRINT",FACE,{"disambiguationData":[TD([[makeQuery(id+"F12.imprint","IMPRINT",EDGE,{"derivedFrom":sQuery(id+"F12.wireOp",EDGE,"E164")}),-1.0]])]});
            extrude(context, id + "F25", {"entities" : qUnion([Q0]), "oppositeDirection" : true, "depth" : 5 * mm});
        }
        {
            var Q0;
            Q0=makeQuery(id+"F12.imprint","IMPRINT",FACE,{"disambiguationData":[TD([[makeQuery(id+"F12.imprint","IMPRINT",EDGE,{"derivedFrom":sQuery(id+"F12.wireOp",EDGE,"E163")}),1.0]])]});
            var Q1;
            Q1=sQuery(id+"F12.wireOp",EDGE,"E163");
            extrude(context, id + "F26", {"entities" : qUnion([Q0]), "surfaceEntities" : qUnion([Q1]), "oppositeDirection" : true, "depth" : 38 * mm});
        }
        {
            var Q0;
            Q0=makeQuery(id+"F26.opExtrude","CAP_FACE",FACE,{"disambiguationData":[OSD([sQuery(id+"F12.wireOp",EDGE,"E163")])],"isStart":true});
            fillet(context, id + "F27", {"entities" : qUnion([Q0]), "radius" : 3 * mm, "tangentPropagation" : true, "allowEdgeOverflow" : false});
        }
        {
            var Q0;
            Q0=makeQuery(id+"F25.opExtrude","CAP_EDGE",EDGE,{"disambiguationData":[OSD([sQuery(id+"F12.wireOp",EDGE,"E164")])],"isStart":true});
            fillet(context, id + "F28", {"entities" : qUnion([Q0]), "radius" : 1 * mm, "tangentPropagation" : true, "allowEdgeOverflow" : false});
        }
        {
            var Q0;
            Q0=makeQuery(id+"F23.opExtrude","CAP_EDGE",EDGE,{"disambiguationData":[OSD([sQuery(id+"F12.wireOp",EDGE,"E176")])],"isStart":true});
            fillet(context, id + "F29", {"entities" : qUnion([Q0]), "radius" : 1 * mm, "tangentPropagation" : true, "allowEdgeOverflow" : false});
        }
        {
            var Q0;
            Q0=makeQuery(id+"F12.imprint","IMPRINT",FACE,{"disambiguationData":[TD([[makeQuery(id+"F12.imprint","IMPRINT",EDGE,{"derivedFrom":sQuery(id+"F12.wireOp",EDGE,"E175")}),1.0]])]});
            var Q1;
            Q1=sQuery(id+"F12.wireOp",EDGE,"E175");
            extrude(context, id + "F30", {"entities" : qUnion([Q0]), "surfaceEntities" : qUnion([Q1]), "oppositeDirection" : true, "depth" : 38 * mm});
        }
        {
            var Q0;
            Q0=makeQuery(id+"F30.opExtrude","CAP_EDGE",EDGE,{"disambiguationData":[OSD([sQuery(id+"F12.wireOp",EDGE,"E175")])],"isStart":true});
            fillet(context, id + "F31", {"entities" : qUnion([Q0]), "radius" : 3 * mm, "tangentPropagation" : true, "allowEdgeOverflow" : false});
        }
        {
            var Q0;
            Q0=makeQuery(id+"F18.imprint","IMPRINT",FACE,{"disambiguationData":[TD([[makeQuery(id+"F18.imprint","IMPRINT",EDGE,{"derivedFrom":sQuery(id+"F18.wireOp",EDGE,"E277.bottom")}),-1.0]])]});
            extrude(context, id + "F32", {"entities" : qUnion([Q0]), "oppositeDirection" : true, "depth" : 5 * mm});
        }
        {
            var Q0;
            Q0=makeQuery(id+"F18.imprint","IMPRINT",FACE,{"disambiguationData":[TD([[makeQuery(id+"F18.imprint","IMPRINT",EDGE,{"derivedFrom":sQuery(id+"F18.wireOp",EDGE,"E288.bottom")}),-1.0]])]});
            extrude(context, id + "F33", {"entities" : qUnion([Q0]), "oppositeDirection" : true, "depth" : 5 * mm});
        }
        {
            var Q0;
            Q0=makeQuery(id+"F32.opExtrude","CAP_EDGE",EDGE,{"disambiguationData":[OSD([sQuery(id+"F18.wireOp",EDGE,"E278")])],"isStart":true});
            fillet(context, id + "F34", {"entities" : qUnion([Q0]), "radius" : 1 * mm, "tangentPropagation" : true, "allowEdgeOverflow" : false});
        }
        {
            var Q0;
            Q0=makeQuery(id+"F26.opExtrude","CAP_FACE",FACE,{"disambiguationData":[OSD([sQuery(id+"F12.wireOp",EDGE,"E163")])],"isStart":false});
            fillet(context, id + "F35", {"entities" : qUnion([Q0]), "radius" : 3 * mm, "tangentPropagation" : true, "allowEdgeOverflow" : false});
        }
        {
            var Q0;
            Q0=makeQuery(id+"F30.opExtrude","CAP_FACE",FACE,{"disambiguationData":[OSD([sQuery(id+"F12.wireOp",EDGE,"E175")])],"isStart":false});
            fillet(context, id + "F36", {"entities" : qUnion([Q0]), "radius" : 3 * mm, "tangentPropagation" : true, "allowEdgeOverflow" : false});
        }
        {
            var Q0;
            Q0=makeQuery(id+"F12.imprint","IMPRINT",FACE,{"disambiguationData":[TD([[makeQuery(id+"F12.imprint","IMPRINT",EDGE,{"derivedFrom":sQuery(id+"F12.wireOp",EDGE,"E191")}),-1.0]])]});
            extrude(context, id + "F37", {"entities" : qUnion([Q0]), "oppositeDirection" : true, "depth" : 5 * mm});
        }
        {
            var Q0;
            Q0=makeQuery(id+"F12.imprint","IMPRINT",FACE,{"disambiguationData":[TD([[makeQuery(id+"F12.imprint","IMPRINT",EDGE,{"derivedFrom":sQuery(id+"F12.wireOp",EDGE,"E190")}),1.0]])]});
            extrude(context, id + "F38", {"entities" : qUnion([Q0]), "oppositeDirection" : true, "depth" : 38 * mm});
        }
        {
            var Q0;
            Q0=sQuery(id+"F12.wireOp",EDGE,"E191");
            var Q1;
            Q1=sQuery(id+"F12.wireOp",EDGE,"E203");
            var Q2;
            Q2=sQuery(id+"F12.wireOp",EDGE,"E215");
            var Q3;
            Q3=sQuery(id+"F12.wireOp",EDGE,"E230");
            var Q4;
            Q4=sQuery(id+"F12.wireOp",EDGE,"E242");
            var Q5;
            Q5=sQuery(id+"F12.wireOp",EDGE,"E254");
            extrude(context, id + "F39", {"bodyType" : ToolBodyType.SURFACE, "surfaceEntities" : qUnion([Q0, Q1, Q2, Q3, Q4, Q5]), "oppositeDirection" : true, "depth" : 38 * mm});
        }
        {
            var Q0;
            Q0=makeQuery(id+"F12.imprint","IMPRINT",FACE,{"disambiguationData":[TD([[makeQuery(id+"F12.imprint","IMPRINT",EDGE,{"derivedFrom":sQuery(id+"F12.wireOp",EDGE,"E203")}),-1.0]])]});
            var Q1;
            Q1=makeQuery(id+"F12.imprint","IMPRINT",FACE,{"disambiguationData":[TD([[makeQuery(id+"F12.imprint","IMPRINT",EDGE,{"derivedFrom":sQuery(id+"F12.wireOp",EDGE,"E215")}),-1.0]])]});
            var Q2;
            Q2=makeQuery(id+"F12.imprint","IMPRINT",FACE,{"disambiguationData":[TD([[makeQuery(id+"F12.imprint","IMPRINT",EDGE,{"derivedFrom":sQuery(id+"F12.wireOp",EDGE,"E254")}),-1.0]])]});
            var Q3;
            Q3=makeQuery(id+"F12.imprint","IMPRINT",FACE,{"disambiguationData":[TD([[makeQuery(id+"F12.imprint","IMPRINT",EDGE,{"derivedFrom":sQuery(id+"F12.wireOp",EDGE,"E242")}),-1.0]])]});
            var Q4;
            Q4=makeQuery(id+"F12.imprint","IMPRINT",FACE,{"disambiguationData":[TD([[makeQuery(id+"F12.imprint","IMPRINT",EDGE,{"derivedFrom":sQuery(id+"F12.wireOp",EDGE,"E230")}),-1.0]])]});
            extrude(context, id + "F40", {"entities" : qUnion([Q0, Q1, Q2, Q3, Q4]), "oppositeDirection" : true, "depth" : 5 * mm});
        }
        {
            var Q0;
            Q0=makeQuery(id+"F12.imprint","IMPRINT",FACE,{"disambiguationData":[TD([[makeQuery(id+"F12.imprint","IMPRINT",EDGE,{"derivedFrom":sQuery(id+"F12.wireOp",EDGE,"E202")}),1.0]])]});
            var Q1;
            Q1=makeQuery(id+"F12.imprint","IMPRINT",FACE,{"disambiguationData":[TD([[makeQuery(id+"F12.imprint","IMPRINT",EDGE,{"derivedFrom":sQuery(id+"F12.wireOp",EDGE,"E214")}),1.0]])]});
            var Q2;
            Q2=makeQuery(id+"F12.imprint","IMPRINT",FACE,{"disambiguationData":[TD([[makeQuery(id+"F12.imprint","IMPRINT",EDGE,{"derivedFrom":sQuery(id+"F12.wireOp",EDGE,"E229")}),1.0]])]});
            var Q3;
            Q3=makeQuery(id+"F12.imprint","IMPRINT",FACE,{"disambiguationData":[TD([[makeQuery(id+"F12.imprint","IMPRINT",EDGE,{"derivedFrom":sQuery(id+"F12.wireOp",EDGE,"E241")}),1.0]])]});
            var Q4;
            Q4=makeQuery(id+"F12.imprint","IMPRINT",FACE,{"disambiguationData":[TD([[makeQuery(id+"F12.imprint","IMPRINT",EDGE,{"derivedFrom":sQuery(id+"F12.wireOp",EDGE,"E253")}),1.0]])]});
            var Q5;
            Q5=sQuery(id+"F12.wireOp",EDGE,"E202");
            var Q6;
            Q6=sQuery(id+"F12.wireOp",EDGE,"E214");
            var Q7;
            Q7=sQuery(id+"F12.wireOp",EDGE,"E229");
            var Q8;
            Q8=sQuery(id+"F12.wireOp",EDGE,"E241");
            var Q9;
            Q9=sQuery(id+"F12.wireOp",EDGE,"E253");
            extrude(context, id + "F41", {"entities" : qUnion([Q0, Q1, Q2, Q3, Q4]), "surfaceEntities" : qUnion([Q5, Q6, Q7, Q8, Q9]), "oppositeDirection" : true, "depth" : 38 * mm});
        }
        {
            var Q0;
            Q0=makeQuery(id+"F41.opExtrude","CAP_EDGE",EDGE,{"disambiguationData":[OSD([sQuery(id+"F12.wireOp",EDGE,"E229")])],"isStart":false});
            var Q1;
            Q1=makeQuery(id+"F41.opExtrude","CAP_FACE",FACE,{"disambiguationData":[OSD([sQuery(id+"F12.wireOp",EDGE,"E202")])],"isStart":false});
            var Q2;
            Q2=makeQuery(id+"F41.opExtrude","CAP_EDGE",EDGE,{"disambiguationData":[OSD([sQuery(id+"F12.wireOp",EDGE,"E241")])],"isStart":false});
            var Q3;
            Q3=makeQuery(id+"F41.opExtrude","CAP_FACE",FACE,{"disambiguationData":[OSD([sQuery(id+"F12.wireOp",EDGE,"E253")])],"isStart":false});
            var Q4;
            Q4=makeQuery(id+"F41.opExtrude","CAP_FACE",FACE,{"disambiguationData":[OSD([sQuery(id+"F12.wireOp",EDGE,"E214")])],"isStart":false});
            var Q5;
            Q5=makeQuery(id+"F38.opExtrude","CAP_FACE",FACE,{"disambiguationData":[OSD([sQuery(id+"F12.wireOp",EDGE,"E190")])],"isStart":false});
            fillet(context, id + "F42", {"entities" : qUnion([Q0, Q1, Q2, Q3, Q4, Q5]), "radius" : 3 * mm, "tangentPropagation" : true, "allowEdgeOverflow" : false});
        }
        {
            var Q0;
            Q0=makeQuery(id+"F37.opExtrude","CAP_FACE",FACE,{"disambiguationData":[OSD([sQuery(id+"F12.wireOp",EDGE,"E191"),sQuery(id+"F12.wireOp",EDGE,"E192.bottom"),sQuery(id+"F12.wireOp",EDGE,"E192.top"),sQuery(id+"F12.wireOp",EDGE,"E192.left"),sQuery(id+"F12.wireOp",EDGE,"E192.right"),sQuery(id+"F12.wireOp",EDGE,"E193.filletArc"),sQuery(id+"F12.wireOp",EDGE,"E194.filletArc"),sQuery(id+"F12.wireOp",EDGE,"E195.filletArc"),sQuery(id+"F12.wireOp",EDGE,"E196.filletArc"),sQuery(id+"F12.wireOp",EDGE,"E197"),sQuery(id+"F12.wireOp",EDGE,"E198"),sQuery(id+"F12.wireOp",EDGE,"E199"),sQuery(id+"F12.wireOp",EDGE,"E200")])],"isStart":false});
            var Q1;
            Q1=makeQuery(id+"F40.opExtrude","CAP_FACE",FACE,{"disambiguationData":[OSD([sQuery(id+"F12.wireOp",EDGE,"E203"),sQuery(id+"F12.wireOp",EDGE,"E204.bottom"),sQuery(id+"F12.wireOp",EDGE,"E204.left"),sQuery(id+"F12.wireOp",EDGE,"E204.right"),sQuery(id+"F12.wireOp",EDGE,"E205.filletArc"),sQuery(id+"F12.wireOp",EDGE,"E206.filletArc"),sQuery(id+"F12.wireOp",EDGE,"E207.filletArc"),sQuery(id+"F12.wireOp",EDGE,"E208.filletArc"),sQuery(id+"F12.wireOp",EDGE,"E209"),sQuery(id+"F12.wireOp",EDGE,"E210"),sQuery(id+"F12.wireOp",EDGE,"E211"),sQuery(id+"F12.wireOp",EDGE,"E212"),sQuery(id+"F12.wireOp",EDGE,"E225")])],"isStart":false});
            var Q2;
            Q2=makeQuery(id+"F40.opExtrude","CAP_FACE",FACE,{"disambiguationData":[OSD([sQuery(id+"F12.wireOp",EDGE,"E215"),sQuery(id+"F12.wireOp",EDGE,"E216.bottom"),sQuery(id+"F12.wireOp",EDGE,"E216.left"),sQuery(id+"F12.wireOp",EDGE,"E216.right"),sQuery(id+"F12.wireOp",EDGE,"E217.filletArc"),sQuery(id+"F12.wireOp",EDGE,"E218.filletArc"),sQuery(id+"F12.wireOp",EDGE,"E219.filletArc"),sQuery(id+"F12.wireOp",EDGE,"E220.filletArc"),sQuery(id+"F12.wireOp",EDGE,"E221"),sQuery(id+"F12.wireOp",EDGE,"E222"),sQuery(id+"F12.wireOp",EDGE,"E223"),sQuery(id+"F12.wireOp",EDGE,"E224"),sQuery(id+"F12.wireOp",EDGE,"E226")])],"isStart":false});
            var Q3;
            Q3=makeQuery(id+"F40.opExtrude","CAP_FACE",FACE,{"disambiguationData":[OSD([sQuery(id+"F12.wireOp",EDGE,"E242"),sQuery(id+"F12.wireOp",EDGE,"E243.bottom"),sQuery(id+"F12.wireOp",EDGE,"E243.left"),sQuery(id+"F12.wireOp",EDGE,"E243.right"),sQuery(id+"F12.wireOp",EDGE,"E244.filletArc"),sQuery(id+"F12.wireOp",EDGE,"E245.filletArc"),sQuery(id+"F12.wireOp",EDGE,"E246.filletArc"),sQuery(id+"F12.wireOp",EDGE,"E247.filletArc"),sQuery(id+"F12.wireOp",EDGE,"E248"),sQuery(id+"F12.wireOp",EDGE,"E249"),sQuery(id+"F12.wireOp",EDGE,"E250"),sQuery(id+"F12.wireOp",EDGE,"E251"),sQuery(id+"F12.wireOp",EDGE,"E264")])],"isStart":false});
            var Q4;
            Q4=makeQuery(id+"F40.opExtrude","CAP_FACE",FACE,{"disambiguationData":[OSD([sQuery(id+"F12.wireOp",EDGE,"E254"),sQuery(id+"F12.wireOp",EDGE,"E255.bottom"),sQuery(id+"F12.wireOp",EDGE,"E255.left"),sQuery(id+"F12.wireOp",EDGE,"E255.right"),sQuery(id+"F12.wireOp",EDGE,"E256.filletArc"),sQuery(id+"F12.wireOp",EDGE,"E257.filletArc"),sQuery(id+"F12.wireOp",EDGE,"E258.filletArc"),sQuery(id+"F12.wireOp",EDGE,"E259.filletArc"),sQuery(id+"F12.wireOp",EDGE,"E260"),sQuery(id+"F12.wireOp",EDGE,"E261"),sQuery(id+"F12.wireOp",EDGE,"E262"),sQuery(id+"F12.wireOp",EDGE,"E263"),sQuery(id+"F12.wireOp",EDGE,"E265")])],"isStart":false});
            var Q5;
            Q5=makeQuery(id+"F40.opExtrude","CAP_FACE",FACE,{"disambiguationData":[OSD([sQuery(id+"F12.wireOp",EDGE,"E230"),sQuery(id+"F12.wireOp",EDGE,"E231.bottom"),sQuery(id+"F12.wireOp",EDGE,"E231.top"),sQuery(id+"F12.wireOp",EDGE,"E231.left"),sQuery(id+"F12.wireOp",EDGE,"E231.right"),sQuery(id+"F12.wireOp",EDGE,"E232.filletArc"),sQuery(id+"F12.wireOp",EDGE,"E233.filletArc"),sQuery(id+"F12.wireOp",EDGE,"E234.filletArc"),sQuery(id+"F12.wireOp",EDGE,"E235.filletArc"),sQuery(id+"F12.wireOp",EDGE,"E236"),sQuery(id+"F12.wireOp",EDGE,"E237"),sQuery(id+"F12.wireOp",EDGE,"E238"),sQuery(id+"F12.wireOp",EDGE,"E239")])],"isStart":false});
            fillet(context, id + "F43", {"entities" : qUnion([Q0, Q1, Q2, Q3, Q4, Q5]), "radius" : 1 * mm, "tangentPropagation" : true, "allowEdgeOverflow" : false});
        }
        {
            var Q0;
            Q0=makeQuery(id+"F18.imprint","IMPRINT",FACE,{"disambiguationData":[TD([[makeQuery(id+"F18.imprint","IMPRINT",EDGE,{"derivedFrom":sQuery(id+"F18.wireOp",EDGE,"E343.bottom")}),-1.0]])]});
            var Q1;
            Q1=makeQuery(id+"F18.imprint","IMPRINT",FACE,{"disambiguationData":[TD([[makeQuery(id+"F18.imprint","IMPRINT",EDGE,{"derivedFrom":sQuery(id+"F18.wireOp",EDGE,"E354.bottom")}),-1.0]])]});
            var Q2;
            Q2=makeQuery(id+"F18.imprint","IMPRINT",FACE,{"disambiguationData":[TD([[makeQuery(id+"F18.imprint","IMPRINT",EDGE,{"derivedFrom":sQuery(id+"F18.wireOp",EDGE,"E332.bottom")}),-1.0]])]});
            var Q3;
            Q3=makeQuery(id+"F18.imprint","IMPRINT",FACE,{"disambiguationData":[TD([[makeQuery(id+"F18.imprint","IMPRINT",EDGE,{"derivedFrom":sQuery(id+"F18.wireOp",EDGE,"E298.bottom")}),-1.0]])]});
            var Q4;
            Q4=makeQuery(id+"F18.imprint","IMPRINT",FACE,{"disambiguationData":[TD([[makeQuery(id+"F18.imprint","IMPRINT",EDGE,{"derivedFrom":sQuery(id+"F18.wireOp",EDGE,"E309.bottom")}),-1.0]])]});
            var Q5;
            Q5=makeQuery(id+"F18.imprint","IMPRINT",FACE,{"disambiguationData":[TD([[makeQuery(id+"F18.imprint","IMPRINT",EDGE,{"derivedFrom":sQuery(id+"F18.wireOp",EDGE,"E320.bottom")}),-1.0]])]});
            var Q6;
            Q6=makeQuery(id+"F18.imprint","IMPRINT",FACE,{"disambiguationData":[TD([[makeQuery(id+"F18.imprint","IMPRINT",EDGE,{"derivedFrom":sQuery(id+"F18.wireOp",EDGE,"E277.bottom")}),-1.0]])]});
            var Q7;
            Q7=makeQuery(id+"F18.imprint","IMPRINT",FACE,{"disambiguationData":[TD([[makeQuery(id+"F18.imprint","IMPRINT",EDGE,{"derivedFrom":sQuery(id+"F18.wireOp",EDGE,"E288.bottom")}),-1.0]])]});
            extrude(context, id + "F44", {"entities" : qUnion([Q0, Q1, Q2, Q3, Q4, Q5, Q6, Q7]), "oppositeDirection" : true, "depth" : 5 * mm});
        }
        {
            var Q0;
            Q0=makeQuery(id+"F44.opExtrude","CAP_EDGE",EDGE,{"disambiguationData":[OSD([sQuery(id+"F18.wireOp",EDGE,"E299")])],"isStart":true});
            var Q1;
            Q1=makeQuery(id+"F44.opExtrude","CAP_EDGE",EDGE,{"disambiguationData":[OSD([sQuery(id+"F18.wireOp",EDGE,"E310")])],"isStart":true});
            var Q2;
            Q2=makeQuery(id+"F44.opExtrude","CAP_EDGE",EDGE,{"disambiguationData":[OSD([sQuery(id+"F18.wireOp",EDGE,"E321")])],"isStart":true});
            var Q3;
            Q3=makeQuery(id+"F44.opExtrude","CAP_EDGE",EDGE,{"disambiguationData":[OSD([sQuery(id+"F18.wireOp",EDGE,"E355")])],"isStart":true});
            var Q4;
            Q4=makeQuery(id+"F44.opExtrude","CAP_EDGE",EDGE,{"disambiguationData":[OSD([sQuery(id+"F18.wireOp",EDGE,"E344")])],"isStart":true});
            var Q5;
            Q5=makeQuery(id+"F44.opExtrude","CAP_EDGE",EDGE,{"disambiguationData":[OSD([sQuery(id+"F18.wireOp",EDGE,"E333")])],"isStart":true});
            fillet(context, id + "F45", {"entities" : qUnion([Q0, Q1, Q2, Q3, Q4, Q5]), "radius" : 1 * mm, "tangentPropagation" : true, "allowEdgeOverflow" : false});
        }
        {
            var Q0;
            Q0=makeQuery(id+"F11.opExtrude","CAP_FACE",FACE,{"disambiguationData":[OSD([sQuery(id+"F10.wireOp",EDGE,"E146.bottom"),sQuery(id+"F10.wireOp",EDGE,"E146.top"),sQuery(id+"F10.wireOp",EDGE,"E146.left"),sQuery(id+"F10.wireOp",EDGE,"E146.right")])],"isStart":false});
            extrude(context, id + "F46", {"entities" : qUnion([Q0]), "operationType" : NewBodyOperationType.REMOVE, "oppositeDirection" : true, "depth" : 5 * mm});
        }
        {
            var Q0;
            Q0=makeQuery(id+"F11.opExtrude","SWEPT_FACE",FACE,{"disambiguationData":[OSD([sQuery(id+"F10.wireOp",EDGE,"E146.top")])]});
            var sketch = newSketch(context, id + "F47", { "sketchPlane" : qUnion([Q0])});
            skLineSegment(sketch, "E365.0", {"start": v(246.5, 353.23) * mm, "end": v(-586.5, 353.23) * mm});
            skLineSegment(sketch, "E365.1", {"start": v(246.5, 353.23) * mm, "end": v(246.5, -349.77) * mm});
            skLineSegment(sketch, "E365.2", {"start": v(246.5, -349.77) * mm, "end": v(-586.5, -349.77) * mm});
            skLineSegment(sketch, "E365.3", {"start": v(-586.5, 353.23) * mm, "end": v(-586.5, -349.77) * mm});
            skSolve(sketch);
        }
        {
            var Q0;
            Q0=makeQuery(id+"F47.imprint","IMPRINT",FACE,{"disambiguationData":[TD([[makeQuery(id+"F47.imprint","IMPRINT",EDGE,{"derivedFrom":sQuery(id+"F47.wireOp",EDGE,"E365.0")}),1.0]])]});
            extrude(context, id + "F48", {"entities" : qUnion([Q0]), "operationType" : NewBodyOperationType.REMOVE, "oppositeDirection" : true, "depth" : 18 * mm});
        }
        {
            var Q0;
            Q0=makeQuery(id+"F48.boolean.opBoolean","COPY",FACE,{"derivedFrom":makeQuery(id+"F48.opExtrude","CAP_FACE",FACE,{"disambiguationData":[OSD([sQuery(id+"F47.wireOp",EDGE,"E365.0"),sQuery(id+"F47.wireOp",EDGE,"E365.1"),sQuery(id+"F47.wireOp",EDGE,"E365.2"),sQuery(id+"F47.wireOp",EDGE,"E365.3")])],"isStart":false})});
            var sketch = newSketch(context, id + "F49", { "sketchPlane" : qUnion([Q0])});
            skLineSegment(sketch, "E366.bottom", {"start": v(-170, -316.77) * mm, "end": v(-585, -316.77) * mm});
            skLineSegment(sketch, "E366.top", {"start": v(-170, -349.77) * mm, "end": v(-585, -349.77) * mm});
            skLineSegment(sketch, "E366.right", {"start": v(-585, -316.77) * mm, "end": v(-585, -349.77) * mm});
            skLineSegment(sketch, "E367.bottom", {"start": v(-170, -316.77) * mm, "end": v(245, -316.77) * mm});
            skLineSegment(sketch, "E367.top", {"start": v(-170, -349.77) * mm, "end": v(245, -349.77) * mm});
            skLineSegment(sketch, "E367.right", {"start": v(245, -316.77) * mm, "end": v(245, -349.77) * mm});
            skLineSegment(sketch, "E368.bottom", {"start": v(-170, 353.23) * mm, "end": v(-585, 353.23) * mm});
            skLineSegment(sketch, "E368.top", {"start": v(-170, 320.23) * mm, "end": v(-585, 320.23) * mm});
            skLineSegment(sketch, "E368.right", {"start": v(-585, 353.23) * mm, "end": v(-585, 320.23) * mm});
            skLineSegment(sketch, "E369.bottom", {"start": v(-170, 353.23) * mm, "end": v(245, 353.23) * mm});
            skLineSegment(sketch, "E369.top", {"start": v(-170, 320.23) * mm, "end": v(245, 320.23) * mm});
            skLineSegment(sketch, "E369.right", {"start": v(245, 353.23) * mm, "end": v(245, 320.23) * mm});
            skLineSegment(sketch, "E370.top", {"start": v(246.5, 319.23) * mm, "end": v(212.5, 319.23) * mm});
            skLineSegment(sketch, "E370.left", {"start": v(246.5, 1.73) * mm, "end": v(246.5, 319.23) * mm});
            skLineSegment(sketch, "E370.right", {"start": v(212.5, 1.73) * mm, "end": v(212.5, 319.23) * mm});
            skLineSegment(sketch, "E371.top", {"start": v(246.5, -315.77) * mm, "end": v(212.5, -315.77) * mm});
            skLineSegment(sketch, "E371.left", {"start": v(246.5, 1.73) * mm, "end": v(246.5, -315.77) * mm});
            skLineSegment(sketch, "E371.right", {"start": v(212.5, 1.73) * mm, "end": v(212.5, -315.77) * mm});
            skLineSegment(sketch, "E372.top", {"start": v(-552.5, 319.23) * mm, "end": v(-586.5, 319.23) * mm});
            skLineSegment(sketch, "E372.left", {"start": v(-552.5, 1.73) * mm, "end": v(-552.5, 319.23) * mm});
            skLineSegment(sketch, "E372.right", {"start": v(-586.5, 1.73) * mm, "end": v(-586.5, 319.23) * mm});
            skLineSegment(sketch, "E373.top", {"start": v(-552.5, -315.77) * mm, "end": v(-586.5, -315.77) * mm});
            skLineSegment(sketch, "E373.left", {"start": v(-552.5, 1.73) * mm, "end": v(-552.5, -315.77) * mm});
            skLineSegment(sketch, "E373.right", {"start": v(-586.5, 1.73) * mm, "end": v(-586.5, -315.77) * mm});
            skSolve(sketch);
        }
        {
            var Q0;
            Q0=makeQuery(id+"F49.imprint","IMPRINT",FACE,{"disambiguationData":[TD([[makeQuery(id+"F49.imprint","IMPRINT",EDGE,{"derivedFrom":sQuery(id+"F49.wireOp",EDGE,"E368.bottom")}),1.0]])]});
            var Q1;
            Q1=makeQuery(id+"F49.imprint","IMPRINT",FACE,{"disambiguationData":[TD([[makeQuery(id+"F49.imprint","IMPRINT",EDGE,{"derivedFrom":sQuery(id+"F49.wireOp",EDGE,"E366.bottom")}),1.0]])]});
            extrude(context, id + "F50", {"entities" : qUnion([Q0, Q1]), "depth" : 3 * mm});
        }
        {
            var Q0;
            Q0=makeQuery(id+"F49.imprint","IMPRINT",FACE,{"disambiguationData":[TD([[makeQuery(id+"F49.imprint","IMPRINT",EDGE,{"derivedFrom":sQuery(id+"F49.wireOp",EDGE,"E370.top")}),1.0]])]});
            var Q1;
            Q1=makeQuery(id+"F49.imprint","IMPRINT",FACE,{"disambiguationData":[TD([[makeQuery(id+"F49.imprint","IMPRINT",EDGE,{"derivedFrom":sQuery(id+"F49.wireOp",EDGE,"E372.top")}),1.0]])]});
            extrude(context, id + "F51", {"entities" : qUnion([Q0, Q1]), "depth" : 3 * mm});
        }
        {
            var Q0;
            Q0=makeQuery(id+"F11.opExtrude","CAP_FACE",FACE,{"disambiguationData":[OSD([sQuery(id+"F10.wireOp",EDGE,"E148.bottom"),sQuery(id+"F10.wireOp",EDGE,"E148.top"),sQuery(id+"F10.wireOp",EDGE,"E148.left"),sQuery(id+"F10.wireOp",EDGE,"E148.right")])],"isStart":false});
            extrude(context, id + "F52", {"entities" : qUnion([Q0]), "operationType" : NewBodyOperationType.REMOVE, "oppositeDirection" : true, "depth" : 5 * mm});
        }
        {
            var Q0;
            Q0=makeQuery(id+"F11.opExtrude","SWEPT_FACE",FACE,{"disambiguationData":[OSD([sQuery(id+"F10.wireOp",EDGE,"E148.top")])]});
            var sketch = newSketch(context, id + "F53", { "sketchPlane" : qUnion([Q0])});
            skLineSegment(sketch, "E374.0", {"start": v(246.5, -349.77) * mm, "end": v(246.5, 353.23) * mm});
            skLineSegment(sketch, "E374.1", {"start": v(-586.5, -349.77) * mm, "end": v(246.5, -349.77) * mm});
            skLineSegment(sketch, "E374.2", {"start": v(-586.5, 353.23) * mm, "end": v(-586.5, -349.77) * mm});
            skLineSegment(sketch, "E374.3", {"start": v(246.5, 353.23) * mm, "end": v(-586.5, 353.23) * mm});
            skSolve(sketch);
        }
        {
            var Q0;
            Q0=makeQuery(id+"F53.imprint","IMPRINT",FACE,{"disambiguationData":[TD([[makeQuery(id+"F53.imprint","IMPRINT",EDGE,{"derivedFrom":sQuery(id+"F53.wireOp",EDGE,"E374.0")}),1.0]])]});
            extrude(context, id + "F54", {"entities" : qUnion([Q0]), "operationType" : NewBodyOperationType.REMOVE, "oppositeDirection" : true, "depth" : 18 * mm});
        }
        {
            var Q0;
            Q0=makeQuery(id+"F54.boolean.opBoolean","COPY",FACE,{"derivedFrom":makeQuery(id+"F54.opExtrude","CAP_FACE",FACE,{"disambiguationData":[OSD([sQuery(id+"F53.wireOp",EDGE,"E374.0"),sQuery(id+"F53.wireOp",EDGE,"E374.1"),sQuery(id+"F53.wireOp",EDGE,"E374.2"),sQuery(id+"F53.wireOp",EDGE,"E374.3")])],"isStart":false})});
            var sketch = newSketch(context, id + "F55", { "sketchPlane" : qUnion([Q0])});
            skLineSegment(sketch, "E375.bottom", {"start": v(-170, -317.77) * mm, "end": v(-585, -317.77) * mm});
            skLineSegment(sketch, "E375.top", {"start": v(-170, -350.77) * mm, "end": v(-585, -350.77) * mm});
            skLineSegment(sketch, "E375.right", {"start": v(-585, -317.77) * mm, "end": v(-585, -350.77) * mm});
            skLineSegment(sketch, "E376.bottom", {"start": v(-170, -317.77) * mm, "end": v(245, -317.77) * mm});
            skLineSegment(sketch, "E376.top", {"start": v(-170, -350.77) * mm, "end": v(245, -350.77) * mm});
            skLineSegment(sketch, "E376.right", {"start": v(245, -317.77) * mm, "end": v(245, -350.77) * mm});
            skLineSegment(sketch, "E377.bottom", {"start": v(-170, 353.23) * mm, "end": v(-585, 353.23) * mm});
            skLineSegment(sketch, "E377.top", {"start": v(-170, 320.23) * mm, "end": v(-585, 320.23) * mm});
            skLineSegment(sketch, "E377.right", {"start": v(-585, 353.23) * mm, "end": v(-585, 320.23) * mm});
            skLineSegment(sketch, "E378.bottom", {"start": v(-170, 353.23) * mm, "end": v(245, 353.23) * mm});
            skLineSegment(sketch, "E378.top", {"start": v(-170, 320.23) * mm, "end": v(245, 320.23) * mm});
            skLineSegment(sketch, "E378.right", {"start": v(245, 353.23) * mm, "end": v(245, 320.23) * mm});
            skLineSegment(sketch, "E379.top", {"start": v(247.5, 319.23) * mm, "end": v(213.5, 319.23) * mm});
            skLineSegment(sketch, "E379.left", {"start": v(247.5, 1.73) * mm, "end": v(247.5, 319.23) * mm});
            skLineSegment(sketch, "E379.right", {"start": v(213.5, 1.73) * mm, "end": v(213.5, 319.23) * mm});
            skLineSegment(sketch, "E380.top", {"start": v(247.5, -315.77) * mm, "end": v(213.5, -315.77) * mm});
            skLineSegment(sketch, "E380.left", {"start": v(247.5, 1.73) * mm, "end": v(247.5, -315.77) * mm});
            skLineSegment(sketch, "E380.right", {"start": v(213.5, 1.73) * mm, "end": v(213.5, -315.77) * mm});
            skLineSegment(sketch, "E381.top", {"start": v(-552.5, 319.23) * mm, "end": v(-586.5, 319.23) * mm});
            skLineSegment(sketch, "E381.left", {"start": v(-552.5, 1.73) * mm, "end": v(-552.5, 319.23) * mm});
            skLineSegment(sketch, "E381.right", {"start": v(-586.5, 1.73) * mm, "end": v(-586.5, 319.23) * mm});
            skLineSegment(sketch, "E382.top", {"start": v(-552.5, -315.77) * mm, "end": v(-586.5, -315.77) * mm});
            skLineSegment(sketch, "E382.left", {"start": v(-552.5, 1.73) * mm, "end": v(-552.5, -315.77) * mm});
            skLineSegment(sketch, "E382.right", {"start": v(-586.5, 1.73) * mm, "end": v(-586.5, -315.77) * mm});
            skSolve(sketch);
        }
        {
            var Q0;
            {var subQ5=sQuery(id+"F55.wireOp",EDGE,"E375.bottom");Q0=makeQuery(id+"F55.imprint","IMPRINT",FACE,{"disambiguationData":[TD([[makeQuery(id+"F55.imprint","IMPRINT",EDGE,{"derivedFrom":subQ5}),1.0]])]});}
            var Q1;
            {var subQ6=sQuery(id+"F55.wireOp",EDGE,"E379.right");Q1=makeQuery(id+"F55.imprint","IMPRINT",FACE,{"disambiguationData":[TD([[makeQuery(id+"F55.imprint","IMPRINT",EDGE,{"derivedFrom":subQ6}),-1.0]])]});}
            var Q2;
            Q2=makeQuery(id+"F55.imprint","IMPRINT",FACE,{"disambiguationData":[TD([[makeQuery(id+"F55.imprint","IMPRINT",EDGE,{"derivedFrom":sQuery(id+"F55.wireOp",EDGE,"E381.top")}),1.0]])]});
            var Q3;
            Q3=makeQuery(id+"F55.imprint","IMPRINT",FACE,{"disambiguationData":[TD([[makeQuery(id+"F55.imprint","IMPRINT",EDGE,{"derivedFrom":sQuery(id+"F55.wireOp",EDGE,"E377.bottom")}),1.0]])]});
            extrude(context, id + "F56", {"entities" : qUnion([Q0, Q1, Q2, Q3]), "depth" : 3 * mm});
        }
        {
            var Q0;
            Q0=makeQuery(id+"F11.opExtrude","SWEPT_FACE",FACE,{"disambiguationData":[OSD([sQuery(id+"F10.wireOp",EDGE,"E58.bottom")])]});
            var sketch = newSketch(context, id + "F57", { "sketchPlane" : qUnion([Q0])});
            skLineSegment(sketch, "E383", {"start": v(-587.5, -280.63) * mm, "end": v(-417.5, -280.63) * mm});
            skLineSegment(sketch, "E384", {"start": v(-417.5, -280.63) * mm, "end": v(-417.5, -217.13) * mm});
            skCircle(sketch, "E385", {"center": v(-417.5, -217.13) * mm, "radius": 20 * mm});
            skCircle(sketch, "E386", {"center": v(-417.5, -217.13) * mm, "radius": 57.5 * mm});
            skLineSegment(sketch, "E387.bottom", {"start": v(-361.5, -277.13) * mm, "end": v(-473.5, -277.13) * mm});
            skLineSegment(sketch, "E387.top", {"start": v(-361.5, -157.13) * mm, "end": v(-473.5, -157.13) * mm});
            skLineSegment(sketch, "E387.left", {"start": v(-357.5, -273.13) * mm, "end": v(-357.5, -161.13) * mm});
            skLineSegment(sketch, "E387.right", {"start": v(-477.5, -273.13) * mm, "end": v(-477.5, -161.13) * mm});
            skPoint(sketch, "E388.visualSharp", {"position": v(-477.5, -157.13) * mm});
            skArc(sketch, "E388.filletArc", {"start": v(-473.5, -157.13) * mm, "mid": v(-476.33, -158.3) * mm, "end": v(-477.5, -161.13) * mm});
            skPoint(sketch, "E389.visualSharp", {"position": v(-357.5, -157.13) * mm});
            skArc(sketch, "E389.filletArc", {"start": v(-357.5, -161.13) * mm, "mid": v(-358.67, -158.3) * mm, "end": v(-361.5, -157.13) * mm});
            skPoint(sketch, "E390.visualSharp", {"position": v(-477.5, -277.13) * mm});
            skArc(sketch, "E390.filletArc", {"start": v(-477.5, -273.13) * mm, "mid": v(-476.33, -275.96) * mm, "end": v(-473.5, -277.13) * mm});
            skPoint(sketch, "E391.visualSharp", {"position": v(-357.5, -277.13) * mm});
            skArc(sketch, "E391.filletArc", {"start": v(-361.5, -277.13) * mm, "mid": v(-358.67, -275.96) * mm, "end": v(-357.5, -273.13) * mm});
            skCircle(sketch, "E392", {"center": v(-363, -271.13) * mm, "radius": 2.5 * mm});
            skCircle(sketch, "E393", {"center": v(-471.85, -271.25) * mm, "radius": 2.5 * mm});
            skCircle(sketch, "E394", {"center": v(-471.61, -162.77) * mm, "radius": 2.5 * mm});
            skCircle(sketch, "E395", {"center": v(-362.7, -163.32) * mm, "radius": 2.5 * mm});
            skLineSegment(sketch, "E396", {"start": v(-417.5, -217.13) * mm, "end": v(-167.5, -217.13) * mm, "construction": true});
            skCircle(sketch, "E397", {"center": v(-167.5, -217.13) * mm, "radius": 20 * mm});
            skCircle(sketch, "E398", {"center": v(-167.5, -217.13) * mm, "radius": 57.5 * mm});
            skLineSegment(sketch, "E399.bottom", {"start": v(-111.5, -277.13) * mm, "end": v(-223.5, -277.13) * mm});
            skLineSegment(sketch, "E399.left", {"start": v(-107.5, -273.13) * mm, "end": v(-107.5, -161.13) * mm});
            skLineSegment(sketch, "E399.right", {"start": v(-227.5, -273.13) * mm, "end": v(-227.5, -161.13) * mm});
            skPoint(sketch, "E400.visualSharp", {"position": v(-227.5, -157.13) * mm});
            skArc(sketch, "E400.filletArc", {"start": v(-223.5, -157.13) * mm, "mid": v(-226.33, -158.3) * mm, "end": v(-227.5, -161.13) * mm});
            skPoint(sketch, "E401.visualSharp", {"position": v(-107.5, -157.13) * mm});
            skArc(sketch, "E401.filletArc", {"start": v(-107.5, -161.13) * mm, "mid": v(-108.67, -158.3) * mm, "end": v(-111.5, -157.13) * mm});
            skPoint(sketch, "E402.visualSharp", {"position": v(-227.5, -277.13) * mm});
            skArc(sketch, "E402.filletArc", {"start": v(-227.5, -273.13) * mm, "mid": v(-226.33, -275.96) * mm, "end": v(-223.5, -277.13) * mm});
            skPoint(sketch, "E403.visualSharp", {"position": v(-107.5, -277.13) * mm});
            skArc(sketch, "E403.filletArc", {"start": v(-111.5, -277.13) * mm, "mid": v(-108.67, -275.96) * mm, "end": v(-107.5, -273.13) * mm});
            skCircle(sketch, "E404", {"center": v(-113, -271.13) * mm, "radius": 2.5 * mm});
            skCircle(sketch, "E405", {"center": v(-221.85, -271.25) * mm, "radius": 2.5 * mm});
            skCircle(sketch, "E406", {"center": v(-221.61, -162.77) * mm, "radius": 2.5 * mm});
            skCircle(sketch, "E407", {"center": v(-112.7, -163.32) * mm, "radius": 2.5 * mm});
            skLineSegment(sketch, "E408", {"start": v(-167.5, -217.13) * mm, "end": v(82.5, -217.13) * mm, "construction": true});
            skCircle(sketch, "E409", {"center": v(82.5, -217.13) * mm, "radius": 20 * mm});
            skCircle(sketch, "E410", {"center": v(82.5, -217.13) * mm, "radius": 57.5 * mm});
            skLineSegment(sketch, "E411.bottom", {"start": v(138.5, -277.13) * mm, "end": v(26.5, -277.13) * mm});
            skLineSegment(sketch, "E411.left", {"start": v(142.5, -273.13) * mm, "end": v(142.5, -161.13) * mm});
            skLineSegment(sketch, "E411.right", {"start": v(22.5, -273.13) * mm, "end": v(22.5, -161.13) * mm});
            skPoint(sketch, "E412.visualSharp", {"position": v(22.5, -157.13) * mm});
            skArc(sketch, "E412.filletArc", {"start": v(26.5, -157.13) * mm, "mid": v(23.67, -158.3) * mm, "end": v(22.5, -161.13) * mm});
            skPoint(sketch, "E413.visualSharp", {"position": v(142.5, -157.13) * mm});
            skArc(sketch, "E413.filletArc", {"start": v(142.5, -161.13) * mm, "mid": v(141.33, -158.3) * mm, "end": v(138.5, -157.13) * mm});
            skPoint(sketch, "E414.visualSharp", {"position": v(22.5, -277.13) * mm});
            skArc(sketch, "E414.filletArc", {"start": v(22.5, -273.13) * mm, "mid": v(23.67, -275.96) * mm, "end": v(26.5, -277.13) * mm});
            skPoint(sketch, "E415.visualSharp", {"position": v(142.5, -277.13) * mm});
            skArc(sketch, "E415.filletArc", {"start": v(138.5, -277.13) * mm, "mid": v(141.33, -275.96) * mm, "end": v(142.5, -273.13) * mm});
            skCircle(sketch, "E416", {"center": v(137, -271.13) * mm, "radius": 2.5 * mm});
            skCircle(sketch, "E417", {"center": v(28.15, -271.25) * mm, "radius": 2.5 * mm});
            skCircle(sketch, "E418", {"center": v(28.39, -162.77) * mm, "radius": 2.5 * mm});
            skCircle(sketch, "E419", {"center": v(137.3, -163.32) * mm, "radius": 2.5 * mm});
            skLineSegment(sketch, "E420", {"start": v(-223.5, -157.13) * mm, "end": v(-111.5, -157.13) * mm});
            skLineSegment(sketch, "E421", {"start": v(26.5, -157.13) * mm, "end": v(138.5, -157.13) * mm});
            skLineSegment(sketch, "E422", {"start": v(-587.5, -65.23) * mm, "end": v(-417.5, -65.23) * mm});
            skLineSegment(sketch, "E423", {"start": v(-417.5, -65.23) * mm, "end": v(-417.5, -1.73) * mm});
            skCircle(sketch, "E424", {"center": v(-417.5, -1.73) * mm, "radius": 20 * mm});
            skCircle(sketch, "E425", {"center": v(-417.5, -1.73) * mm, "radius": 57.5 * mm});
            skLineSegment(sketch, "E426.bottom", {"start": v(-361.5, -61.73) * mm, "end": v(-473.5, -61.73) * mm});
            skLineSegment(sketch, "E426.top", {"start": v(-361.5, 58.27) * mm, "end": v(-473.5, 58.27) * mm});
            skLineSegment(sketch, "E426.left", {"start": v(-357.5, -57.73) * mm, "end": v(-357.5, 54.27) * mm});
            skLineSegment(sketch, "E426.right", {"start": v(-477.5, -57.73) * mm, "end": v(-477.5, 54.27) * mm});
            skPoint(sketch, "E427.visualSharp", {"position": v(-477.5, 58.27) * mm});
            skArc(sketch, "E427.filletArc", {"start": v(-473.5, 58.27) * mm, "mid": v(-476.33, 57.1) * mm, "end": v(-477.5, 54.27) * mm});
            skPoint(sketch, "E428.visualSharp", {"position": v(-357.5, 58.27) * mm});
            skArc(sketch, "E428.filletArc", {"start": v(-357.5, 54.27) * mm, "mid": v(-358.67, 57.1) * mm, "end": v(-361.5, 58.27) * mm});
            skPoint(sketch, "E429.visualSharp", {"position": v(-477.5, -61.73) * mm});
            skArc(sketch, "E429.filletArc", {"start": v(-477.5, -57.73) * mm, "mid": v(-476.33, -60.56) * mm, "end": v(-473.5, -61.73) * mm});
            skPoint(sketch, "E430.visualSharp", {"position": v(-357.5, -61.73) * mm});
            skArc(sketch, "E430.filletArc", {"start": v(-361.5, -61.73) * mm, "mid": v(-358.67, -60.56) * mm, "end": v(-357.5, -57.73) * mm});
            skCircle(sketch, "E431", {"center": v(-363, -55.73) * mm, "radius": 2.5 * mm});
            skCircle(sketch, "E432", {"center": v(-471.85, -55.85) * mm, "radius": 2.5 * mm});
            skCircle(sketch, "E433", {"center": v(-471.61, 52.63) * mm, "radius": 2.5 * mm});
            skCircle(sketch, "E434", {"center": v(-362.7, 52.08) * mm, "radius": 2.5 * mm});
            skLineSegment(sketch, "E435", {"start": v(-417.5, -1.73) * mm, "end": v(-167.5, -1.73) * mm, "construction": true});
            skCircle(sketch, "E436", {"center": v(-167.5, -1.73) * mm, "radius": 20 * mm});
            skCircle(sketch, "E437", {"center": v(-167.5, -1.73) * mm, "radius": 57.5 * mm});
            skLineSegment(sketch, "E438.bottom", {"start": v(-111.5, -61.73) * mm, "end": v(-223.5, -61.73) * mm});
            skLineSegment(sketch, "E438.left", {"start": v(-107.5, -57.73) * mm, "end": v(-107.5, 54.27) * mm});
            skLineSegment(sketch, "E438.right", {"start": v(-227.5, -57.73) * mm, "end": v(-227.5, 54.27) * mm});
            skPoint(sketch, "E439.visualSharp", {"position": v(-227.5, 58.27) * mm});
            skArc(sketch, "E439.filletArc", {"start": v(-223.5, 58.27) * mm, "mid": v(-226.33, 57.1) * mm, "end": v(-227.5, 54.27) * mm});
            skPoint(sketch, "E440.visualSharp", {"position": v(-107.5, 58.27) * mm});
            skArc(sketch, "E440.filletArc", {"start": v(-107.5, 54.27) * mm, "mid": v(-108.67, 57.1) * mm, "end": v(-111.5, 58.27) * mm});
            skPoint(sketch, "E441.visualSharp", {"position": v(-227.5, -61.73) * mm});
            skArc(sketch, "E441.filletArc", {"start": v(-227.5, -57.73) * mm, "mid": v(-226.33, -60.56) * mm, "end": v(-223.5, -61.73) * mm});
            skPoint(sketch, "E442.visualSharp", {"position": v(-107.5, -61.73) * mm});
            skArc(sketch, "E442.filletArc", {"start": v(-111.5, -61.73) * mm, "mid": v(-108.67, -60.56) * mm, "end": v(-107.5, -57.73) * mm});
            skCircle(sketch, "E443", {"center": v(-113, -55.73) * mm, "radius": 2.5 * mm});
            skCircle(sketch, "E444", {"center": v(-221.85, -55.85) * mm, "radius": 2.5 * mm});
            skCircle(sketch, "E445", {"center": v(-221.61, 52.63) * mm, "radius": 2.5 * mm});
            skCircle(sketch, "E446", {"center": v(-112.7, 52.08) * mm, "radius": 2.5 * mm});
            skLineSegment(sketch, "E447", {"start": v(-167.5, -1.73) * mm, "end": v(82.5, -1.73) * mm, "construction": true});
            skCircle(sketch, "E448", {"center": v(82.5, -1.73) * mm, "radius": 20 * mm});
            skCircle(sketch, "E449", {"center": v(82.5, -1.73) * mm, "radius": 57.5 * mm});
            skLineSegment(sketch, "E450.bottom", {"start": v(138.5, -61.73) * mm, "end": v(26.5, -61.73) * mm});
            skLineSegment(sketch, "E450.left", {"start": v(142.5, -57.73) * mm, "end": v(142.5, 54.27) * mm});
            skLineSegment(sketch, "E450.right", {"start": v(22.5, -57.73) * mm, "end": v(22.5, 54.27) * mm});
            skPoint(sketch, "E451.visualSharp", {"position": v(22.5, 58.27) * mm});
            skArc(sketch, "E451.filletArc", {"start": v(26.5, 58.27) * mm, "mid": v(23.67, 57.1) * mm, "end": v(22.5, 54.27) * mm});
            skPoint(sketch, "E452.visualSharp", {"position": v(142.5, 58.27) * mm});
            skArc(sketch, "E452.filletArc", {"start": v(142.5, 54.27) * mm, "mid": v(141.33, 57.1) * mm, "end": v(138.5, 58.27) * mm});
            skPoint(sketch, "E453.visualSharp", {"position": v(22.5, -61.73) * mm});
            skArc(sketch, "E453.filletArc", {"start": v(22.5, -57.73) * mm, "mid": v(23.67, -60.56) * mm, "end": v(26.5, -61.73) * mm});
            skPoint(sketch, "E454.visualSharp", {"position": v(142.5, -61.73) * mm});
            skArc(sketch, "E454.filletArc", {"start": v(138.5, -61.73) * mm, "mid": v(141.33, -60.56) * mm, "end": v(142.5, -57.73) * mm});
            skCircle(sketch, "E455", {"center": v(137, -55.73) * mm, "radius": 2.5 * mm});
            skCircle(sketch, "E456", {"center": v(28.15, -55.85) * mm, "radius": 2.5 * mm});
            skCircle(sketch, "E457", {"center": v(28.39, 52.63) * mm, "radius": 2.5 * mm});
            skCircle(sketch, "E458", {"center": v(137.3, 52.08) * mm, "radius": 2.5 * mm});
            skLineSegment(sketch, "E459", {"start": v(-223.5, 58.27) * mm, "end": v(-111.5, 58.27) * mm});
            skLineSegment(sketch, "E460", {"start": v(26.5, 58.27) * mm, "end": v(138.5, 58.27) * mm});
            skLineSegment(sketch, "E461", {"start": v(-587.5, 150.17) * mm, "end": v(-417.5, 150.17) * mm});
            skLineSegment(sketch, "E462", {"start": v(-417.5, 150.17) * mm, "end": v(-417.5, 213.67) * mm});
            skCircle(sketch, "E463", {"center": v(-417.5, 213.67) * mm, "radius": 20 * mm});
            skCircle(sketch, "E464", {"center": v(-417.5, 213.67) * mm, "radius": 57.5 * mm});
            skLineSegment(sketch, "E465.bottom", {"start": v(-361.5, 153.67) * mm, "end": v(-473.5, 153.67) * mm});
            skLineSegment(sketch, "E465.top", {"start": v(-361.5, 273.67) * mm, "end": v(-473.5, 273.67) * mm});
            skLineSegment(sketch, "E465.left", {"start": v(-357.5, 157.67) * mm, "end": v(-357.5, 269.67) * mm});
            skLineSegment(sketch, "E465.right", {"start": v(-477.5, 157.67) * mm, "end": v(-477.5, 269.67) * mm});
            skPoint(sketch, "E466.visualSharp", {"position": v(-477.5, 273.67) * mm});
            skArc(sketch, "E466.filletArc", {"start": v(-473.5, 273.67) * mm, "mid": v(-476.33, 272.5) * mm, "end": v(-477.5, 269.67) * mm});
            skPoint(sketch, "E467.visualSharp", {"position": v(-357.5, 273.67) * mm});
            skArc(sketch, "E467.filletArc", {"start": v(-357.5, 269.67) * mm, "mid": v(-358.67, 272.5) * mm, "end": v(-361.5, 273.67) * mm});
            skPoint(sketch, "E468.visualSharp", {"position": v(-477.5, 153.67) * mm});
            skArc(sketch, "E468.filletArc", {"start": v(-477.5, 157.67) * mm, "mid": v(-476.33, 154.84) * mm, "end": v(-473.5, 153.67) * mm});
            skPoint(sketch, "E469.visualSharp", {"position": v(-357.5, 153.67) * mm});
            skArc(sketch, "E469.filletArc", {"start": v(-361.5, 153.67) * mm, "mid": v(-358.67, 154.84) * mm, "end": v(-357.5, 157.67) * mm});
            skCircle(sketch, "E470", {"center": v(-363, 159.67) * mm, "radius": 2.5 * mm});
            skCircle(sketch, "E471", {"center": v(-471.85, 159.55) * mm, "radius": 2.5 * mm});
            skCircle(sketch, "E472", {"center": v(-471.61, 268.03) * mm, "radius": 2.5 * mm});
            skCircle(sketch, "E473", {"center": v(-362.7, 267.48) * mm, "radius": 2.5 * mm});
            skLineSegment(sketch, "E474", {"start": v(-417.5, 213.67) * mm, "end": v(-167.5, 213.67) * mm, "construction": true});
            skCircle(sketch, "E475", {"center": v(-167.5, 213.67) * mm, "radius": 20 * mm});
            skCircle(sketch, "E476", {"center": v(-167.5, 213.67) * mm, "radius": 57.5 * mm});
            skLineSegment(sketch, "E477.bottom", {"start": v(-111.5, 153.67) * mm, "end": v(-223.5, 153.67) * mm});
            skLineSegment(sketch, "E477.left", {"start": v(-107.5, 157.67) * mm, "end": v(-107.5, 269.67) * mm});
            skLineSegment(sketch, "E477.right", {"start": v(-227.5, 157.67) * mm, "end": v(-227.5, 269.67) * mm});
            skPoint(sketch, "E478.visualSharp", {"position": v(-227.5, 273.67) * mm});
            skArc(sketch, "E478.filletArc", {"start": v(-223.5, 273.67) * mm, "mid": v(-226.33, 272.5) * mm, "end": v(-227.5, 269.67) * mm});
            skPoint(sketch, "E479.visualSharp", {"position": v(-107.5, 273.67) * mm});
            skArc(sketch, "E479.filletArc", {"start": v(-107.5, 269.67) * mm, "mid": v(-108.67, 272.5) * mm, "end": v(-111.5, 273.67) * mm});
            skPoint(sketch, "E480.visualSharp", {"position": v(-227.5, 153.67) * mm});
            skArc(sketch, "E480.filletArc", {"start": v(-227.5, 157.67) * mm, "mid": v(-226.33, 154.84) * mm, "end": v(-223.5, 153.67) * mm});
            skPoint(sketch, "E481.visualSharp", {"position": v(-107.5, 153.67) * mm});
            skArc(sketch, "E481.filletArc", {"start": v(-111.5, 153.67) * mm, "mid": v(-108.67, 154.84) * mm, "end": v(-107.5, 157.67) * mm});
            skCircle(sketch, "E482", {"center": v(-113, 159.67) * mm, "radius": 2.5 * mm});
            skCircle(sketch, "E483", {"center": v(-221.85, 159.55) * mm, "radius": 2.5 * mm});
            skCircle(sketch, "E484", {"center": v(-221.61, 268.03) * mm, "radius": 2.5 * mm});
            skCircle(sketch, "E485", {"center": v(-112.7, 267.48) * mm, "radius": 2.5 * mm});
            skLineSegment(sketch, "E486", {"start": v(-167.5, 213.67) * mm, "end": v(82.5, 213.67) * mm, "construction": true});
            skCircle(sketch, "E487", {"center": v(82.5, 213.67) * mm, "radius": 20 * mm});
            skCircle(sketch, "E488", {"center": v(82.5, 213.67) * mm, "radius": 57.5 * mm});
            skLineSegment(sketch, "E489.bottom", {"start": v(138.5, 153.67) * mm, "end": v(26.5, 153.67) * mm});
            skLineSegment(sketch, "E489.left", {"start": v(142.5, 157.67) * mm, "end": v(142.5, 269.67) * mm});
            skLineSegment(sketch, "E489.right", {"start": v(22.5, 157.67) * mm, "end": v(22.5, 269.67) * mm});
            skPoint(sketch, "E490.visualSharp", {"position": v(22.5, 273.67) * mm});
            skArc(sketch, "E490.filletArc", {"start": v(26.5, 273.67) * mm, "mid": v(23.67, 272.5) * mm, "end": v(22.5, 269.67) * mm});
            skPoint(sketch, "E491.visualSharp", {"position": v(142.5, 273.67) * mm});
            skArc(sketch, "E491.filletArc", {"start": v(142.5, 269.67) * mm, "mid": v(141.33, 272.5) * mm, "end": v(138.5, 273.67) * mm});
            skPoint(sketch, "E492.visualSharp", {"position": v(22.5, 153.67) * mm});
            skArc(sketch, "E492.filletArc", {"start": v(22.5, 157.67) * mm, "mid": v(23.67, 154.84) * mm, "end": v(26.5, 153.67) * mm});
            skPoint(sketch, "E493.visualSharp", {"position": v(142.5, 153.67) * mm});
            skArc(sketch, "E493.filletArc", {"start": v(138.5, 153.67) * mm, "mid": v(141.33, 154.84) * mm, "end": v(142.5, 157.67) * mm});
            skCircle(sketch, "E494", {"center": v(137, 159.67) * mm, "radius": 2.5 * mm});
            skCircle(sketch, "E495", {"center": v(28.15, 159.55) * mm, "radius": 2.5 * mm});
            skCircle(sketch, "E496", {"center": v(28.39, 268.03) * mm, "radius": 2.5 * mm});
            skCircle(sketch, "E497", {"center": v(137.3, 267.48) * mm, "radius": 2.5 * mm});
            skLineSegment(sketch, "E498", {"start": v(-223.5, 273.67) * mm, "end": v(-111.5, 273.67) * mm});
            skLineSegment(sketch, "E499", {"start": v(26.5, 273.67) * mm, "end": v(138.5, 273.67) * mm});
            skSolve(sketch);
        }
        {
            var Q0;
            Q0=makeQuery(id+"F57.imprint","IMPRINT",FACE,{"disambiguationData":[TD([[makeQuery(id+"F57.imprint","IMPRINT",EDGE,{"derivedFrom":sQuery(id+"F57.wireOp",EDGE,"E385")}),1.0]])]});
            var Q1;
            Q1=makeQuery(id+"F57.imprint","IMPRINT",FACE,{"disambiguationData":[TD([[makeQuery(id+"F57.imprint","IMPRINT",EDGE,{"derivedFrom":sQuery(id+"F57.wireOp",EDGE,"E424")}),1.0]])]});
            var Q2;
            Q2=makeQuery(id+"F57.imprint","IMPRINT",FACE,{"disambiguationData":[TD([[makeQuery(id+"F57.imprint","IMPRINT",EDGE,{"derivedFrom":sQuery(id+"F57.wireOp",EDGE,"E436")}),1.0]])]});
            var Q3;
            Q3=makeQuery(id+"F57.imprint","IMPRINT",FACE,{"disambiguationData":[TD([[makeQuery(id+"F57.imprint","IMPRINT",EDGE,{"derivedFrom":sQuery(id+"F57.wireOp",EDGE,"E397")}),1.0]])]});
            var Q4;
            Q4=makeQuery(id+"F57.imprint","IMPRINT",FACE,{"disambiguationData":[TD([[makeQuery(id+"F57.imprint","IMPRINT",EDGE,{"derivedFrom":sQuery(id+"F57.wireOp",EDGE,"E409")}),1.0]])]});
            var Q5;
            Q5=makeQuery(id+"F57.imprint","IMPRINT",FACE,{"disambiguationData":[TD([[makeQuery(id+"F57.imprint","IMPRINT",EDGE,{"derivedFrom":sQuery(id+"F57.wireOp",EDGE,"E448")}),1.0]])]});
            var Q6;
            Q6=makeQuery(id+"F57.imprint","IMPRINT",FACE,{"disambiguationData":[TD([[makeQuery(id+"F57.imprint","IMPRINT",EDGE,{"derivedFrom":sQuery(id+"F57.wireOp",EDGE,"E463")}),1.0]])]});
            var Q7;
            Q7=makeQuery(id+"F57.imprint","IMPRINT",FACE,{"disambiguationData":[TD([[makeQuery(id+"F57.imprint","IMPRINT",EDGE,{"derivedFrom":sQuery(id+"F57.wireOp",EDGE,"E475")}),1.0]])]});
            var Q8;
            Q8=makeQuery(id+"F57.imprint","IMPRINT",FACE,{"disambiguationData":[TD([[makeQuery(id+"F57.imprint","IMPRINT",EDGE,{"derivedFrom":sQuery(id+"F57.wireOp",EDGE,"E487")}),1.0]])]});
            var Q9;
            Q9=sQuery(id+"F57.wireOp",EDGE,"E385");
            var Q10;
            Q10=sQuery(id+"F57.wireOp",EDGE,"E397");
            var Q11;
            Q11=sQuery(id+"F57.wireOp",EDGE,"E409");
            var Q12;
            Q12=sQuery(id+"F57.wireOp",EDGE,"E448");
            var Q13;
            Q13=sQuery(id+"F57.wireOp",EDGE,"E436");
            var Q14;
            Q14=sQuery(id+"F57.wireOp",EDGE,"E424");
            var Q15;
            Q15=sQuery(id+"F57.wireOp",EDGE,"E463");
            var Q16;
            Q16=sQuery(id+"F57.wireOp",EDGE,"E475");
            var Q17;
            Q17=sQuery(id+"F57.wireOp",EDGE,"E487");
            extrude(context, id + "F58", {"entities" : qUnion([Q0, Q1, Q2, Q3, Q4, Q5, Q6, Q7, Q8]), "surfaceEntities" : qUnion([Q9, Q10, Q11, Q12, Q13, Q14, Q15, Q16, Q17]), "oppositeDirection" : true, "depth" : 38 * mm});
        }
        {
            var Q0;
            Q0=sQuery(id+"F57.wireOp",EDGE,"E464");
            var Q1;
            Q1=sQuery(id+"F57.wireOp",EDGE,"E476");
            var Q2;
            Q2=sQuery(id+"F57.wireOp",EDGE,"E488");
            var Q3;
            Q3=sQuery(id+"F57.wireOp",EDGE,"E449");
            var Q4;
            Q4=sQuery(id+"F57.wireOp",EDGE,"E437");
            var Q5;
            Q5=sQuery(id+"F57.wireOp",EDGE,"E425");
            var Q6;
            Q6=sQuery(id+"F57.wireOp",EDGE,"E386");
            var Q7;
            Q7=sQuery(id+"F57.wireOp",EDGE,"E398");
            var Q8;
            Q8=sQuery(id+"F57.wireOp",EDGE,"E410");
            extrude(context, id + "F59", {"bodyType" : ToolBodyType.SURFACE, "surfaceEntities" : qUnion([Q0, Q1, Q2, Q3, Q4, Q5, Q6, Q7, Q8]), "oppositeDirection" : true, "depth" : 38 * mm});
        }
        {
            var Q0;
            Q0=makeQuery(id+"F57.imprint","IMPRINT",FACE,{"disambiguationData":[TD([[makeQuery(id+"F57.imprint","IMPRINT",EDGE,{"derivedFrom":sQuery(id+"F57.wireOp",EDGE,"E386")}),-1.0]])]});
            var Q1;
            Q1=makeQuery(id+"F57.imprint","IMPRINT",FACE,{"disambiguationData":[TD([[makeQuery(id+"F57.imprint","IMPRINT",EDGE,{"derivedFrom":sQuery(id+"F57.wireOp",EDGE,"E398")}),-1.0]])]});
            var Q2;
            Q2=makeQuery(id+"F57.imprint","IMPRINT",FACE,{"disambiguationData":[TD([[makeQuery(id+"F57.imprint","IMPRINT",EDGE,{"derivedFrom":sQuery(id+"F57.wireOp",EDGE,"E410")}),-1.0]])]});
            var Q3;
            Q3=makeQuery(id+"F57.imprint","IMPRINT",FACE,{"disambiguationData":[TD([[makeQuery(id+"F57.imprint","IMPRINT",EDGE,{"derivedFrom":sQuery(id+"F57.wireOp",EDGE,"E449")}),-1.0]])]});
            var Q4;
            Q4=makeQuery(id+"F57.imprint","IMPRINT",FACE,{"disambiguationData":[TD([[makeQuery(id+"F57.imprint","IMPRINT",EDGE,{"derivedFrom":sQuery(id+"F57.wireOp",EDGE,"E437")}),-1.0]])]});
            var Q5;
            Q5=makeQuery(id+"F57.imprint","IMPRINT",FACE,{"disambiguationData":[TD([[makeQuery(id+"F57.imprint","IMPRINT",EDGE,{"derivedFrom":sQuery(id+"F57.wireOp",EDGE,"E425")}),-1.0]])]});
            var Q6;
            Q6=makeQuery(id+"F57.imprint","IMPRINT",FACE,{"disambiguationData":[TD([[makeQuery(id+"F57.imprint","IMPRINT",EDGE,{"derivedFrom":sQuery(id+"F57.wireOp",EDGE,"E464")}),-1.0]])]});
            var Q7;
            Q7=makeQuery(id+"F57.imprint","IMPRINT",FACE,{"disambiguationData":[TD([[makeQuery(id+"F57.imprint","IMPRINT",EDGE,{"derivedFrom":sQuery(id+"F57.wireOp",EDGE,"E476")}),-1.0]])]});
            var Q8;
            Q8=makeQuery(id+"F57.imprint","IMPRINT",FACE,{"disambiguationData":[TD([[makeQuery(id+"F57.imprint","IMPRINT",EDGE,{"derivedFrom":sQuery(id+"F57.wireOp",EDGE,"E488")}),-1.0]])]});
            extrude(context, id + "F60", {"entities" : qUnion([Q0, Q1, Q2, Q3, Q4, Q5, Q6, Q7, Q8]), "oppositeDirection" : true, "depth" : 5 * mm});
        }
        {
            var Q0;
            Q0=makeQuery(id+"F58.opExtrude","CAP_FACE",FACE,{"disambiguationData":[OSD([sQuery(id+"F57.wireOp",EDGE,"E385")])],"isStart":true});
            var Q1;
            Q1=makeQuery(id+"F58.opExtrude","CAP_FACE",FACE,{"disambiguationData":[OSD([sQuery(id+"F57.wireOp",EDGE,"E397")])],"isStart":true});
            var Q2;
            Q2=makeQuery(id+"F58.opExtrude","CAP_FACE",FACE,{"disambiguationData":[OSD([sQuery(id+"F57.wireOp",EDGE,"E409")])],"isStart":true});
            var Q3;
            Q3=makeQuery(id+"F58.opExtrude","CAP_FACE",FACE,{"disambiguationData":[OSD([sQuery(id+"F57.wireOp",EDGE,"E448")])],"isStart":true});
            var Q4;
            Q4=makeQuery(id+"F58.opExtrude","CAP_FACE",FACE,{"disambiguationData":[OSD([sQuery(id+"F57.wireOp",EDGE,"E436")])],"isStart":true});
            var Q5;
            Q5=makeQuery(id+"F58.opExtrude","CAP_FACE",FACE,{"disambiguationData":[OSD([sQuery(id+"F57.wireOp",EDGE,"E424")])],"isStart":true});
            var Q6;
            Q6=makeQuery(id+"F58.opExtrude","CAP_FACE",FACE,{"disambiguationData":[OSD([sQuery(id+"F57.wireOp",EDGE,"E463")])],"isStart":true});
            var Q7;
            Q7=makeQuery(id+"F58.opExtrude","CAP_EDGE",EDGE,{"disambiguationData":[OSD([sQuery(id+"F57.wireOp",EDGE,"E475")])],"isStart":true});
            var Q8;
            Q8=makeQuery(id+"F58.opExtrude","CAP_FACE",FACE,{"disambiguationData":[OSD([sQuery(id+"F57.wireOp",EDGE,"E487")])],"isStart":true});
            fillet(context, id + "F61", {"entities" : qUnion([Q0, Q1, Q2, Q3, Q4, Q5, Q6, Q7, Q8]), "radius" : 3 * mm, "tangentPropagation" : true, "allowEdgeOverflow" : false});
        }
        {
            var Q0;
            Q0=makeQuery(id+"F60.opExtrude","CAP_EDGE",EDGE,{"disambiguationData":[OSD([sQuery(id+"F57.wireOp",EDGE,"E398")])],"isStart":false});
            var Q1;
            Q1=makeQuery(id+"F60.opExtrude","CAP_EDGE",EDGE,{"disambiguationData":[OSD([sQuery(id+"F57.wireOp",EDGE,"E449")])],"isStart":false});
            var Q2;
            Q2=makeQuery(id+"F60.opExtrude","CAP_EDGE",EDGE,{"disambiguationData":[OSD([sQuery(id+"F57.wireOp",EDGE,"E437")])],"isStart":false});
            var Q3;
            Q3=makeQuery(id+"F60.opExtrude","CAP_EDGE",EDGE,{"disambiguationData":[OSD([sQuery(id+"F57.wireOp",EDGE,"E410")])],"isStart":false});
            var Q4;
            Q4=makeQuery(id+"F60.opExtrude","CAP_EDGE",EDGE,{"disambiguationData":[OSD([sQuery(id+"F57.wireOp",EDGE,"E386")])],"isStart":false});
            var Q5;
            Q5=makeQuery(id+"F60.opExtrude","CAP_EDGE",EDGE,{"disambiguationData":[OSD([sQuery(id+"F57.wireOp",EDGE,"E425")])],"isStart":false});
            var Q6;
            Q6=makeQuery(id+"F60.opExtrude","CAP_EDGE",EDGE,{"disambiguationData":[OSD([sQuery(id+"F57.wireOp",EDGE,"E488")])],"isStart":false});
            var Q7;
            Q7=makeQuery(id+"F60.opExtrude","CAP_EDGE",EDGE,{"disambiguationData":[OSD([sQuery(id+"F57.wireOp",EDGE,"E476")])],"isStart":false});
            var Q8;
            Q8=makeQuery(id+"F60.opExtrude","CAP_EDGE",EDGE,{"disambiguationData":[OSD([sQuery(id+"F57.wireOp",EDGE,"E464")])],"isStart":false});
            fillet(context, id + "F62", {"entities" : qUnion([Q0, Q1, Q2, Q3, Q4, Q5, Q6, Q7, Q8]), "radius" : 1 * mm, "tangentPropagation" : true, "allowEdgeOverflow" : false});
        }
        {
            var Q0;
            Q0=makeQuery(id+"F58.opExtrude","CAP_FACE",FACE,{"disambiguationData":[OSD([sQuery(id+"F57.wireOp",EDGE,"E385")])],"isStart":false});
            var sketch = newSketch(context, id + "F63", { "sketchPlane" : qUnion([Q0])});
            skLineSegment(sketch, "E500.bottom", {"start": v(-361.5, 157.13) * mm, "end": v(-473.5, 157.13) * mm});
            skLineSegment(sketch, "E500.top", {"start": v(-361.5, 277.13) * mm, "end": v(-473.5, 277.13) * mm});
            skLineSegment(sketch, "E500.left", {"start": v(-357.5, 161.13) * mm, "end": v(-357.5, 273.13) * mm});
            skLineSegment(sketch, "E500.right", {"start": v(-477.5, 161.13) * mm, "end": v(-477.5, 273.13) * mm});
            skPoint(sketch, "E500.middle", {"position": v(-417.5, 217.13) * mm});
            skCircle(sketch, "E501", {"center": v(-417.5, 217.13) * mm, "radius": 57.5 * mm});
            skPoint(sketch, "E502.visualSharp", {"position": v(-477.5, 277.13) * mm});
            skArc(sketch, "E502.filletArc", {"start": v(-473.5, 277.13) * mm, "mid": v(-476.33, 275.96) * mm, "end": v(-477.5, 273.13) * mm});
            skPoint(sketch, "E503.visualSharp", {"position": v(-357.5, 277.13) * mm});
            skArc(sketch, "E503.filletArc", {"start": v(-357.5, 273.13) * mm, "mid": v(-358.67, 275.96) * mm, "end": v(-361.5, 277.13) * mm});
            skPoint(sketch, "E504.visualSharp", {"position": v(-357.5, 157.13) * mm});
            skArc(sketch, "E504.filletArc", {"start": v(-361.5, 157.13) * mm, "mid": v(-358.67, 158.3) * mm, "end": v(-357.5, 161.13) * mm});
            skPoint(sketch, "E505.visualSharp", {"position": v(-477.5, 157.13) * mm});
            skArc(sketch, "E505.filletArc", {"start": v(-477.5, 161.13) * mm, "mid": v(-476.33, 158.3) * mm, "end": v(-473.5, 157.13) * mm});
            skCircle(sketch, "E506", {"center": v(-471.87, 163.03) * mm, "radius": 2.5 * mm});
            skCircle(sketch, "E507", {"center": v(-362.45, 163.44) * mm, "radius": 2.5 * mm});
            skCircle(sketch, "E508", {"center": v(-363.42, 271.53) * mm, "radius": 2.5 * mm});
            skCircle(sketch, "E509", {"center": v(-471.98, 271.14) * mm, "radius": 2.5 * mm});
            skLineSegment(sketch, "E510", {"start": v(-417.5, 217.13) * mm, "end": v(-167.5, 217.13) * mm, "construction": true});
            skLineSegment(sketch, "E511.bottom", {"start": v(-111.5, 157.13) * mm, "end": v(-223.5, 157.13) * mm});
            skLineSegment(sketch, "E511.top", {"start": v(-111.5, 277.13) * mm, "end": v(-223.5, 277.13) * mm});
            skLineSegment(sketch, "E511.left", {"start": v(-107.5, 161.13) * mm, "end": v(-107.5, 273.13) * mm});
            skLineSegment(sketch, "E511.right", {"start": v(-227.5, 161.13) * mm, "end": v(-227.5, 273.13) * mm});
            skPoint(sketch, "E511.middle", {"position": v(-167.5, 217.13) * mm});
            skCircle(sketch, "E512", {"center": v(-167.5, 217.13) * mm, "radius": 57.5 * mm});
            skPoint(sketch, "E513.visualSharp", {"position": v(-227.5, 277.13) * mm});
            skArc(sketch, "E513.filletArc", {"start": v(-223.5, 277.13) * mm, "mid": v(-226.33, 275.96) * mm, "end": v(-227.5, 273.13) * mm});
            skPoint(sketch, "E514.visualSharp", {"position": v(-107.5, 277.13) * mm});
            skArc(sketch, "E514.filletArc", {"start": v(-107.5, 273.13) * mm, "mid": v(-108.67, 275.96) * mm, "end": v(-111.5, 277.13) * mm});
            skPoint(sketch, "E515.visualSharp", {"position": v(-107.5, 157.13) * mm});
            skArc(sketch, "E515.filletArc", {"start": v(-111.5, 157.13) * mm, "mid": v(-108.67, 158.3) * mm, "end": v(-107.5, 161.13) * mm});
            skPoint(sketch, "E516.visualSharp", {"position": v(-227.5, 157.13) * mm});
            skArc(sketch, "E516.filletArc", {"start": v(-227.5, 161.13) * mm, "mid": v(-226.33, 158.3) * mm, "end": v(-223.5, 157.13) * mm});
            skCircle(sketch, "E517", {"center": v(-221.87, 163.03) * mm, "radius": 2.5 * mm});
            skCircle(sketch, "E518", {"center": v(-112.45, 163.44) * mm, "radius": 2.5 * mm});
            skCircle(sketch, "E519", {"center": v(-113.42, 271.53) * mm, "radius": 2.5 * mm});
            skCircle(sketch, "E520", {"center": v(-221.98, 271.14) * mm, "radius": 2.5 * mm});
            skLineSegment(sketch, "E521", {"start": v(-167.5, 217.13) * mm, "end": v(82.5, 217.13) * mm, "construction": true});
            skLineSegment(sketch, "E522.bottom", {"start": v(138.5, 157.13) * mm, "end": v(26.5, 157.13) * mm});
            skLineSegment(sketch, "E522.top", {"start": v(138.5, 277.13) * mm, "end": v(26.5, 277.13) * mm});
            skLineSegment(sketch, "E522.left", {"start": v(142.5, 161.13) * mm, "end": v(142.5, 273.13) * mm});
            skLineSegment(sketch, "E522.right", {"start": v(22.5, 161.13) * mm, "end": v(22.5, 273.13) * mm});
            skPoint(sketch, "E522.middle", {"position": v(82.5, 217.13) * mm});
            skCircle(sketch, "E523", {"center": v(82.5, 217.13) * mm, "radius": 57.5 * mm});
            skPoint(sketch, "E524.visualSharp", {"position": v(22.5, 277.13) * mm});
            skArc(sketch, "E524.filletArc", {"start": v(26.5, 277.13) * mm, "mid": v(23.67, 275.96) * mm, "end": v(22.5, 273.13) * mm});
            skPoint(sketch, "E525.visualSharp", {"position": v(142.5, 277.13) * mm});
            skArc(sketch, "E525.filletArc", {"start": v(142.5, 273.13) * mm, "mid": v(141.33, 275.96) * mm, "end": v(138.5, 277.13) * mm});
            skPoint(sketch, "E526.visualSharp", {"position": v(142.5, 157.13) * mm});
            skArc(sketch, "E526.filletArc", {"start": v(138.5, 157.13) * mm, "mid": v(141.33, 158.3) * mm, "end": v(142.5, 161.13) * mm});
            skPoint(sketch, "E527.visualSharp", {"position": v(22.5, 157.13) * mm});
            skArc(sketch, "E527.filletArc", {"start": v(22.5, 161.13) * mm, "mid": v(23.67, 158.3) * mm, "end": v(26.5, 157.13) * mm});
            skCircle(sketch, "E528", {"center": v(28.13, 163.03) * mm, "radius": 2.5 * mm});
            skCircle(sketch, "E529", {"center": v(137.55, 163.44) * mm, "radius": 2.5 * mm});
            skCircle(sketch, "E530", {"center": v(136.58, 271.53) * mm, "radius": 2.5 * mm});
            skCircle(sketch, "E531", {"center": v(28.02, 271.14) * mm, "radius": 2.5 * mm});
            skLineSegment(sketch, "E532.bottom", {"start": v(-361.5, -58.27) * mm, "end": v(-473.5, -58.27) * mm});
            skLineSegment(sketch, "E532.top", {"start": v(-361.5, 61.73) * mm, "end": v(-473.5, 61.73) * mm});
            skLineSegment(sketch, "E532.left", {"start": v(-357.5, -54.27) * mm, "end": v(-357.5, 57.73) * mm});
            skLineSegment(sketch, "E532.right", {"start": v(-477.5, -54.27) * mm, "end": v(-477.5, 57.73) * mm});
            skPoint(sketch, "E532.middle", {"position": v(-417.5, 1.73) * mm});
            skCircle(sketch, "E533", {"center": v(-417.5, 1.73) * mm, "radius": 57.5 * mm});
            skPoint(sketch, "E534.visualSharp", {"position": v(-477.5, 61.73) * mm});
            skArc(sketch, "E534.filletArc", {"start": v(-473.5, 61.73) * mm, "mid": v(-476.33, 60.56) * mm, "end": v(-477.5, 57.73) * mm});
            skPoint(sketch, "E535.visualSharp", {"position": v(-357.5, 61.73) * mm});
            skArc(sketch, "E535.filletArc", {"start": v(-357.5, 57.73) * mm, "mid": v(-358.67, 60.56) * mm, "end": v(-361.5, 61.73) * mm});
            skPoint(sketch, "E536.visualSharp", {"position": v(-357.5, -58.27) * mm});
            skArc(sketch, "E536.filletArc", {"start": v(-361.5, -58.27) * mm, "mid": v(-358.67, -57.1) * mm, "end": v(-357.5, -54.27) * mm});
            skPoint(sketch, "E537.visualSharp", {"position": v(-477.5, -58.27) * mm});
            skArc(sketch, "E537.filletArc", {"start": v(-477.5, -54.27) * mm, "mid": v(-476.33, -57.1) * mm, "end": v(-473.5, -58.27) * mm});
            skCircle(sketch, "E538", {"center": v(-471.87, -52.37) * mm, "radius": 2.5 * mm});
            skCircle(sketch, "E539", {"center": v(-362.45, -51.96) * mm, "radius": 2.5 * mm});
            skCircle(sketch, "E540", {"center": v(-363.42, 56.13) * mm, "radius": 2.5 * mm});
            skCircle(sketch, "E541", {"center": v(-471.98, 55.74) * mm, "radius": 2.5 * mm});
            skLineSegment(sketch, "E542", {"start": v(-417.5, 1.73) * mm, "end": v(-167.5, 1.73) * mm, "construction": true});
            skLineSegment(sketch, "E543.bottom", {"start": v(-111.5, -58.27) * mm, "end": v(-223.5, -58.27) * mm});
            skLineSegment(sketch, "E543.top", {"start": v(-111.5, 61.73) * mm, "end": v(-223.5, 61.73) * mm});
            skLineSegment(sketch, "E543.left", {"start": v(-107.5, -54.27) * mm, "end": v(-107.5, 57.73) * mm});
            skLineSegment(sketch, "E543.right", {"start": v(-227.5, -54.27) * mm, "end": v(-227.5, 57.73) * mm});
            skPoint(sketch, "E543.middle", {"position": v(-167.5, 1.73) * mm});
            skCircle(sketch, "E544", {"center": v(-167.5, 1.73) * mm, "radius": 57.5 * mm});
            skPoint(sketch, "E545.visualSharp", {"position": v(-227.5, 61.73) * mm});
            skArc(sketch, "E545.filletArc", {"start": v(-223.5, 61.73) * mm, "mid": v(-226.33, 60.56) * mm, "end": v(-227.5, 57.73) * mm});
            skPoint(sketch, "E546.visualSharp", {"position": v(-107.5, 61.73) * mm});
            skArc(sketch, "E546.filletArc", {"start": v(-107.5, 57.73) * mm, "mid": v(-108.67, 60.56) * mm, "end": v(-111.5, 61.73) * mm});
            skPoint(sketch, "E547.visualSharp", {"position": v(-107.5, -58.27) * mm});
            skArc(sketch, "E547.filletArc", {"start": v(-111.5, -58.27) * mm, "mid": v(-108.67, -57.1) * mm, "end": v(-107.5, -54.27) * mm});
            skPoint(sketch, "E548.visualSharp", {"position": v(-227.5, -58.27) * mm});
            skArc(sketch, "E548.filletArc", {"start": v(-227.5, -54.27) * mm, "mid": v(-226.33, -57.1) * mm, "end": v(-223.5, -58.27) * mm});
            skCircle(sketch, "E549", {"center": v(-221.87, -52.37) * mm, "radius": 2.5 * mm});
            skCircle(sketch, "E550", {"center": v(-112.45, -51.96) * mm, "radius": 2.5 * mm});
            skCircle(sketch, "E551", {"center": v(-113.42, 56.13) * mm, "radius": 2.5 * mm});
            skCircle(sketch, "E552", {"center": v(-221.98, 55.74) * mm, "radius": 2.5 * mm});
            skLineSegment(sketch, "E553", {"start": v(-167.5, 1.73) * mm, "end": v(82.5, 1.73) * mm, "construction": true});
            skLineSegment(sketch, "E554.bottom", {"start": v(138.5, -58.27) * mm, "end": v(26.5, -58.27) * mm});
            skLineSegment(sketch, "E554.top", {"start": v(138.5, 61.73) * mm, "end": v(26.5, 61.73) * mm});
            skLineSegment(sketch, "E554.left", {"start": v(142.5, -54.27) * mm, "end": v(142.5, 57.73) * mm});
            skLineSegment(sketch, "E554.right", {"start": v(22.5, -54.27) * mm, "end": v(22.5, 57.73) * mm});
            skPoint(sketch, "E554.middle", {"position": v(82.5, 1.73) * mm});
            skCircle(sketch, "E555", {"center": v(82.5, 1.73) * mm, "radius": 57.5 * mm});
            skPoint(sketch, "E556.visualSharp", {"position": v(22.5, 61.73) * mm});
            skArc(sketch, "E556.filletArc", {"start": v(26.5, 61.73) * mm, "mid": v(23.67, 60.56) * mm, "end": v(22.5, 57.73) * mm});
            skPoint(sketch, "E557.visualSharp", {"position": v(142.5, 61.73) * mm});
            skArc(sketch, "E557.filletArc", {"start": v(142.5, 57.73) * mm, "mid": v(141.33, 60.56) * mm, "end": v(138.5, 61.73) * mm});
            skPoint(sketch, "E558.visualSharp", {"position": v(142.5, -58.27) * mm});
            skArc(sketch, "E558.filletArc", {"start": v(138.5, -58.27) * mm, "mid": v(141.33, -57.1) * mm, "end": v(142.5, -54.27) * mm});
            skPoint(sketch, "E559.visualSharp", {"position": v(22.5, -58.27) * mm});
            skArc(sketch, "E559.filletArc", {"start": v(22.5, -54.27) * mm, "mid": v(23.67, -57.1) * mm, "end": v(26.5, -58.27) * mm});
            skCircle(sketch, "E560", {"center": v(28.13, -52.37) * mm, "radius": 2.5 * mm});
            skCircle(sketch, "E561", {"center": v(137.55, -51.96) * mm, "radius": 2.5 * mm});
            skCircle(sketch, "E562", {"center": v(136.58, 56.13) * mm, "radius": 2.5 * mm});
            skCircle(sketch, "E563", {"center": v(28.02, 55.74) * mm, "radius": 2.5 * mm});
            skLineSegment(sketch, "E564", {"start": v(82.5, 217.13) * mm, "end": v(82.5, 65.23) * mm, "construction": true});
            skLineSegment(sketch, "E565", {"start": v(82.5, 65.23) * mm, "end": v(82.5, 1.73) * mm, "construction": true});
            skLineSegment(sketch, "E566.bottom", {"start": v(-361.5, -273.67) * mm, "end": v(-473.5, -273.67) * mm});
            skLineSegment(sketch, "E566.top", {"start": v(-361.5, -153.67) * mm, "end": v(-473.5, -153.67) * mm});
            skLineSegment(sketch, "E566.left", {"start": v(-357.5, -269.67) * mm, "end": v(-357.5, -157.67) * mm});
            skLineSegment(sketch, "E566.right", {"start": v(-477.5, -269.67) * mm, "end": v(-477.5, -157.67) * mm});
            skPoint(sketch, "E566.middle", {"position": v(-417.5, -213.67) * mm});
            skCircle(sketch, "E567", {"center": v(-417.5, -213.67) * mm, "radius": 57.5 * mm});
            skPoint(sketch, "E568.visualSharp", {"position": v(-477.5, -153.67) * mm});
            skArc(sketch, "E568.filletArc", {"start": v(-473.5, -153.67) * mm, "mid": v(-476.33, -154.84) * mm, "end": v(-477.5, -157.67) * mm});
            skPoint(sketch, "E569.visualSharp", {"position": v(-357.5, -153.67) * mm});
            skArc(sketch, "E569.filletArc", {"start": v(-357.5, -157.67) * mm, "mid": v(-358.67, -154.84) * mm, "end": v(-361.5, -153.67) * mm});
            skPoint(sketch, "E570.visualSharp", {"position": v(-357.5, -273.67) * mm});
            skArc(sketch, "E570.filletArc", {"start": v(-361.5, -273.67) * mm, "mid": v(-358.67, -272.5) * mm, "end": v(-357.5, -269.67) * mm});
            skPoint(sketch, "E571.visualSharp", {"position": v(-477.5, -273.67) * mm});
            skArc(sketch, "E571.filletArc", {"start": v(-477.5, -269.67) * mm, "mid": v(-476.33, -272.5) * mm, "end": v(-473.5, -273.67) * mm});
            skCircle(sketch, "E572", {"center": v(-471.87, -267.77) * mm, "radius": 2.5 * mm});
            skCircle(sketch, "E573", {"center": v(-362.45, -267.36) * mm, "radius": 2.5 * mm});
            skCircle(sketch, "E574", {"center": v(-363.42, -159.27) * mm, "radius": 2.5 * mm});
            skCircle(sketch, "E575", {"center": v(-471.98, -159.66) * mm, "radius": 2.5 * mm});
            skLineSegment(sketch, "E576", {"start": v(-417.5, -213.67) * mm, "end": v(-167.5, -213.67) * mm, "construction": true});
            skLineSegment(sketch, "E577.bottom", {"start": v(-111.5, -273.67) * mm, "end": v(-223.5, -273.67) * mm});
            skLineSegment(sketch, "E577.top", {"start": v(-111.5, -153.67) * mm, "end": v(-223.5, -153.67) * mm});
            skLineSegment(sketch, "E577.left", {"start": v(-107.5, -269.67) * mm, "end": v(-107.5, -157.67) * mm});
            skLineSegment(sketch, "E577.right", {"start": v(-227.5, -269.67) * mm, "end": v(-227.5, -157.67) * mm});
            skPoint(sketch, "E577.middle", {"position": v(-167.5, -213.67) * mm});
            skCircle(sketch, "E578", {"center": v(-167.5, -213.67) * mm, "radius": 57.5 * mm});
            skPoint(sketch, "E579.visualSharp", {"position": v(-227.5, -153.67) * mm});
            skArc(sketch, "E579.filletArc", {"start": v(-223.5, -153.67) * mm, "mid": v(-226.33, -154.84) * mm, "end": v(-227.5, -157.67) * mm});
            skPoint(sketch, "E580.visualSharp", {"position": v(-107.5, -153.67) * mm});
            skArc(sketch, "E580.filletArc", {"start": v(-107.5, -157.67) * mm, "mid": v(-108.67, -154.84) * mm, "end": v(-111.5, -153.67) * mm});
            skPoint(sketch, "E581.visualSharp", {"position": v(-107.5, -273.67) * mm});
            skArc(sketch, "E581.filletArc", {"start": v(-111.5, -273.67) * mm, "mid": v(-108.67, -272.5) * mm, "end": v(-107.5, -269.67) * mm});
            skPoint(sketch, "E582.visualSharp", {"position": v(-227.5, -273.67) * mm});
            skArc(sketch, "E582.filletArc", {"start": v(-227.5, -269.67) * mm, "mid": v(-226.33, -272.5) * mm, "end": v(-223.5, -273.67) * mm});
            skCircle(sketch, "E583", {"center": v(-221.87, -267.77) * mm, "radius": 2.5 * mm});
            skCircle(sketch, "E584", {"center": v(-112.45, -267.36) * mm, "radius": 2.5 * mm});
            skCircle(sketch, "E585", {"center": v(-113.42, -159.27) * mm, "radius": 2.5 * mm});
            skCircle(sketch, "E586", {"center": v(-221.98, -159.66) * mm, "radius": 2.5 * mm});
            skLineSegment(sketch, "E587", {"start": v(-167.5, -213.67) * mm, "end": v(82.5, -213.67) * mm, "construction": true});
            skLineSegment(sketch, "E588.bottom", {"start": v(138.5, -273.67) * mm, "end": v(26.5, -273.67) * mm});
            skLineSegment(sketch, "E588.top", {"start": v(138.5, -153.67) * mm, "end": v(26.5, -153.67) * mm});
            skLineSegment(sketch, "E588.left", {"start": v(142.5, -269.67) * mm, "end": v(142.5, -157.67) * mm});
            skLineSegment(sketch, "E588.right", {"start": v(22.5, -269.67) * mm, "end": v(22.5, -157.67) * mm});
            skPoint(sketch, "E588.middle", {"position": v(82.5, -213.67) * mm});
            skCircle(sketch, "E589", {"center": v(82.5, -213.67) * mm, "radius": 57.5 * mm});
            skPoint(sketch, "E590.visualSharp", {"position": v(22.5, -153.67) * mm});
            skArc(sketch, "E590.filletArc", {"start": v(26.5, -153.67) * mm, "mid": v(23.67, -154.84) * mm, "end": v(22.5, -157.67) * mm});
            skPoint(sketch, "E591.visualSharp", {"position": v(142.5, -153.67) * mm});
            skArc(sketch, "E591.filletArc", {"start": v(142.5, -157.67) * mm, "mid": v(141.33, -154.84) * mm, "end": v(138.5, -153.67) * mm});
            skPoint(sketch, "E592.visualSharp", {"position": v(142.5, -273.67) * mm});
            skArc(sketch, "E592.filletArc", {"start": v(138.5, -273.67) * mm, "mid": v(141.33, -272.5) * mm, "end": v(142.5, -269.67) * mm});
            skPoint(sketch, "E593.visualSharp", {"position": v(22.5, -273.67) * mm});
            skArc(sketch, "E593.filletArc", {"start": v(22.5, -269.67) * mm, "mid": v(23.67, -272.5) * mm, "end": v(26.5, -273.67) * mm});
            skCircle(sketch, "E594", {"center": v(28.13, -267.77) * mm, "radius": 2.5 * mm});
            skCircle(sketch, "E595", {"center": v(137.55, -267.36) * mm, "radius": 2.5 * mm});
            skCircle(sketch, "E596", {"center": v(136.58, -159.27) * mm, "radius": 2.5 * mm});
            skCircle(sketch, "E597", {"center": v(28.02, -159.66) * mm, "radius": 2.5 * mm});
            skLineSegment(sketch, "E598", {"start": v(82.5, 1.73) * mm, "end": v(82.5, -213.67) * mm, "construction": true});
            skSolve(sketch);
        }
        {
            var Q0;
            Q0=makeQuery(id+"F63.imprint","IMPRINT",FACE,{"disambiguationData":[TD([[makeQuery(id+"F63.imprint","IMPRINT",EDGE,{"derivedFrom":sQuery(id+"F63.wireOp",EDGE,"E554.bottom")}),-1.0]])]});
            var Q1;
            Q1=makeQuery(id+"F63.imprint","IMPRINT",FACE,{"disambiguationData":[TD([[makeQuery(id+"F63.imprint","IMPRINT",EDGE,{"derivedFrom":sQuery(id+"F63.wireOp",EDGE,"E522.bottom")}),-1.0]])]});
            var Q2;
            Q2=makeQuery(id+"F63.imprint","IMPRINT",FACE,{"disambiguationData":[TD([[makeQuery(id+"F63.imprint","IMPRINT",EDGE,{"derivedFrom":sQuery(id+"F63.wireOp",EDGE,"E511.bottom")}),-1.0]])]});
            var Q3;
            Q3=makeQuery(id+"F63.imprint","IMPRINT",FACE,{"disambiguationData":[TD([[makeQuery(id+"F63.imprint","IMPRINT",EDGE,{"derivedFrom":sQuery(id+"F63.wireOp",EDGE,"E543.bottom")}),-1.0]])]});
            var Q4;
            Q4=makeQuery(id+"F63.imprint","IMPRINT",FACE,{"disambiguationData":[TD([[makeQuery(id+"F63.imprint","IMPRINT",EDGE,{"derivedFrom":sQuery(id+"F63.wireOp",EDGE,"E500.bottom")}),-1.0]])]});
            var Q5;
            Q5=makeQuery(id+"F63.imprint","IMPRINT",FACE,{"disambiguationData":[TD([[makeQuery(id+"F63.imprint","IMPRINT",EDGE,{"derivedFrom":sQuery(id+"F63.wireOp",EDGE,"E532.bottom")}),-1.0]])]});
            var Q6;
            Q6=makeQuery(id+"F63.imprint","IMPRINT",FACE,{"disambiguationData":[TD([[makeQuery(id+"F63.imprint","IMPRINT",EDGE,{"derivedFrom":sQuery(id+"F63.wireOp",EDGE,"E588.bottom")}),-1.0]])]});
            var Q7;
            Q7=makeQuery(id+"F63.imprint","IMPRINT",FACE,{"disambiguationData":[TD([[makeQuery(id+"F63.imprint","IMPRINT",EDGE,{"derivedFrom":sQuery(id+"F63.wireOp",EDGE,"E577.bottom")}),-1.0]])]});
            var Q8;
            Q8=makeQuery(id+"F63.imprint","IMPRINT",FACE,{"disambiguationData":[TD([[makeQuery(id+"F63.imprint","IMPRINT",EDGE,{"derivedFrom":sQuery(id+"F63.wireOp",EDGE,"E566.bottom")}),-1.0]])]});
            extrude(context, id + "F64", {"entities" : qUnion([Q0, Q1, Q2, Q3, Q4, Q5, Q6, Q7, Q8]), "oppositeDirection" : true, "depth" : 5 * mm});
        }
        {
            var Q0;
            Q0=makeQuery(id+"F58.opExtrude","CAP_EDGE",EDGE,{"disambiguationData":[OSD([sQuery(id+"F57.wireOp",EDGE,"E385")])],"isStart":false});
            var Q1;
            Q1=makeQuery(id+"F58.opExtrude","CAP_FACE",FACE,{"disambiguationData":[OSD([sQuery(id+"F57.wireOp",EDGE,"E397")])],"isStart":false});
            var Q2;
            Q2=makeQuery(id+"F58.opExtrude","CAP_FACE",FACE,{"disambiguationData":[OSD([sQuery(id+"F57.wireOp",EDGE,"E409")])],"isStart":false});
            var Q3;
            Q3=makeQuery(id+"F58.opExtrude","CAP_FACE",FACE,{"disambiguationData":[OSD([sQuery(id+"F57.wireOp",EDGE,"E448")])],"isStart":false});
            var Q4;
            Q4=makeQuery(id+"F58.opExtrude","CAP_FACE",FACE,{"disambiguationData":[OSD([sQuery(id+"F57.wireOp",EDGE,"E436")])],"isStart":false});
            var Q5;
            Q5=makeQuery(id+"F58.opExtrude","CAP_FACE",FACE,{"disambiguationData":[OSD([sQuery(id+"F57.wireOp",EDGE,"E424")])],"isStart":false});
            var Q6;
            Q6=makeQuery(id+"F58.opExtrude","CAP_EDGE",EDGE,{"disambiguationData":[OSD([sQuery(id+"F57.wireOp",EDGE,"E463")])],"isStart":false});
            var Q7;
            Q7=makeQuery(id+"F58.opExtrude","CAP_EDGE",EDGE,{"disambiguationData":[OSD([sQuery(id+"F57.wireOp",EDGE,"E475")])],"isStart":false});
            var Q8;
            Q8=makeQuery(id+"F58.opExtrude","CAP_EDGE",EDGE,{"disambiguationData":[OSD([sQuery(id+"F57.wireOp",EDGE,"E487")])],"isStart":false});
            fillet(context, id + "F65", {"entities" : qUnion([Q0, Q1, Q2, Q3, Q4, Q5, Q6, Q7, Q8]), "radius" : 3 * mm, "tangentPropagation" : true, "allowEdgeOverflow" : false});
        }
        {
            var Q0;
            Q0=makeQuery(id+"F64.opExtrude","CAP_EDGE",EDGE,{"disambiguationData":[OSD([sQuery(id+"F63.wireOp",EDGE,"E501")])],"isStart":false});
            var Q1;
            Q1=makeQuery(id+"F64.opExtrude","CAP_EDGE",EDGE,{"disambiguationData":[OSD([sQuery(id+"F63.wireOp",EDGE,"E512")])],"isStart":false});
            var Q2;
            Q2=makeQuery(id+"F64.opExtrude","CAP_EDGE",EDGE,{"disambiguationData":[OSD([sQuery(id+"F63.wireOp",EDGE,"E523")])],"isStart":false});
            var Q3;
            Q3=makeQuery(id+"F64.opExtrude","CAP_EDGE",EDGE,{"disambiguationData":[OSD([sQuery(id+"F63.wireOp",EDGE,"E555")])],"isStart":false});
            var Q4;
            Q4=makeQuery(id+"F64.opExtrude","CAP_EDGE",EDGE,{"disambiguationData":[OSD([sQuery(id+"F63.wireOp",EDGE,"E544")])],"isStart":false});
            var Q5;
            Q5=makeQuery(id+"F64.opExtrude","CAP_EDGE",EDGE,{"disambiguationData":[OSD([sQuery(id+"F63.wireOp",EDGE,"E533")])],"isStart":false});
            var Q6;
            Q6=makeQuery(id+"F64.opExtrude","CAP_EDGE",EDGE,{"disambiguationData":[OSD([sQuery(id+"F63.wireOp",EDGE,"E567")])],"isStart":false});
            var Q7;
            Q7=makeQuery(id+"F64.opExtrude","CAP_EDGE",EDGE,{"disambiguationData":[OSD([sQuery(id+"F63.wireOp",EDGE,"E578")])],"isStart":false});
            var Q8;
            Q8=makeQuery(id+"F64.opExtrude","CAP_EDGE",EDGE,{"disambiguationData":[OSD([sQuery(id+"F63.wireOp",EDGE,"E589")])],"isStart":false});
            fillet(context, id + "F66", {"entities" : qUnion([Q0, Q1, Q2, Q3, Q4, Q5, Q6, Q7, Q8]), "radius" : 1 * mm, "tangentPropagation" : true, "allowEdgeOverflow" : false});
        }
        {
            var Q0;
            Q0=makeQuery(id+"F11.opExtrude","SWEPT_FACE",FACE,{"disambiguationData":[OSD([sQuery(id+"F10.wireOp",EDGE,"E102.bottom")])]});
            var sketch = newSketch(context, id + "F67", { "sketchPlane" : qUnion([Q0])});
            skLineSegment(sketch, "E599", {"start": v(-587.5, -280.63) * mm, "end": v(-417.5, -280.63) * mm});
            skLineSegment(sketch, "E600", {"start": v(-417.5, -280.63) * mm, "end": v(-417.5, -217.13) * mm});
            skCircle(sketch, "E601", {"center": v(-417.5, -217.13) * mm, "radius": 20 * mm});
            skCircle(sketch, "E602", {"center": v(-417.5, -217.13) * mm, "radius": 57.5 * mm});
            skLineSegment(sketch, "E603.bottom", {"start": v(-361.5, -277.13) * mm, "end": v(-473.5, -277.13) * mm});
            skLineSegment(sketch, "E603.top", {"start": v(-361.5, -157.13) * mm, "end": v(-473.5, -157.13) * mm});
            skLineSegment(sketch, "E603.left", {"start": v(-357.5, -273.13) * mm, "end": v(-357.5, -161.13) * mm});
            skLineSegment(sketch, "E603.right", {"start": v(-477.5, -273.13) * mm, "end": v(-477.5, -161.13) * mm});
            skPoint(sketch, "E604.visualSharp", {"position": v(-477.5, -157.13) * mm});
            skArc(sketch, "E604.filletArc", {"start": v(-473.5, -157.13) * mm, "mid": v(-476.33, -158.3) * mm, "end": v(-477.5, -161.13) * mm});
            skPoint(sketch, "E605.visualSharp", {"position": v(-357.5, -157.13) * mm});
            skArc(sketch, "E605.filletArc", {"start": v(-357.5, -161.13) * mm, "mid": v(-358.67, -158.3) * mm, "end": v(-361.5, -157.13) * mm});
            skPoint(sketch, "E606.visualSharp", {"position": v(-477.5, -277.13) * mm});
            skArc(sketch, "E606.filletArc", {"start": v(-477.5, -273.13) * mm, "mid": v(-476.33, -275.96) * mm, "end": v(-473.5, -277.13) * mm});
            skPoint(sketch, "E607.visualSharp", {"position": v(-357.5, -277.13) * mm});
            skArc(sketch, "E607.filletArc", {"start": v(-361.5, -277.13) * mm, "mid": v(-358.67, -275.96) * mm, "end": v(-357.5, -273.13) * mm});
            skCircle(sketch, "E608", {"center": v(-363, -271.13) * mm, "radius": 2.5 * mm});
            skCircle(sketch, "E609", {"center": v(-471.85, -271.25) * mm, "radius": 2.5 * mm});
            skCircle(sketch, "E610", {"center": v(-471.61, -162.77) * mm, "radius": 2.5 * mm});
            skCircle(sketch, "E611", {"center": v(-362.7, -163.32) * mm, "radius": 2.5 * mm});
            skLineSegment(sketch, "E612", {"start": v(-417.5, -217.13) * mm, "end": v(-167.5, -217.13) * mm, "construction": true});
            skCircle(sketch, "E613", {"center": v(-167.5, -217.13) * mm, "radius": 20 * mm});
            skCircle(sketch, "E614", {"center": v(-167.5, -217.13) * mm, "radius": 57.5 * mm});
            skLineSegment(sketch, "E615.bottom", {"start": v(-111.5, -277.13) * mm, "end": v(-223.5, -277.13) * mm});
            skLineSegment(sketch, "E615.left", {"start": v(-107.5, -273.13) * mm, "end": v(-107.5, -161.13) * mm});
            skLineSegment(sketch, "E615.right", {"start": v(-227.5, -273.13) * mm, "end": v(-227.5, -161.13) * mm});
            skPoint(sketch, "E616.visualSharp", {"position": v(-227.5, -157.13) * mm});
            skArc(sketch, "E616.filletArc", {"start": v(-223.5, -157.13) * mm, "mid": v(-226.33, -158.3) * mm, "end": v(-227.5, -161.13) * mm});
            skPoint(sketch, "E617.visualSharp", {"position": v(-107.5, -157.13) * mm});
            skArc(sketch, "E617.filletArc", {"start": v(-107.5, -161.13) * mm, "mid": v(-108.67, -158.3) * mm, "end": v(-111.5, -157.13) * mm});
            skPoint(sketch, "E618.visualSharp", {"position": v(-227.5, -277.13) * mm});
            skArc(sketch, "E618.filletArc", {"start": v(-227.5, -273.13) * mm, "mid": v(-226.33, -275.96) * mm, "end": v(-223.5, -277.13) * mm});
            skPoint(sketch, "E619.visualSharp", {"position": v(-107.5, -277.13) * mm});
            skArc(sketch, "E619.filletArc", {"start": v(-111.5, -277.13) * mm, "mid": v(-108.67, -275.96) * mm, "end": v(-107.5, -273.13) * mm});
            skCircle(sketch, "E620", {"center": v(-113, -271.13) * mm, "radius": 2.5 * mm});
            skCircle(sketch, "E621", {"center": v(-221.85, -271.25) * mm, "radius": 2.5 * mm});
            skCircle(sketch, "E622", {"center": v(-221.61, -162.77) * mm, "radius": 2.5 * mm});
            skCircle(sketch, "E623", {"center": v(-112.7, -163.32) * mm, "radius": 2.5 * mm});
            skLineSegment(sketch, "E624", {"start": v(-167.5, -217.13) * mm, "end": v(82.5, -217.13) * mm, "construction": true});
            skCircle(sketch, "E625", {"center": v(82.5, -217.13) * mm, "radius": 20 * mm});
            skCircle(sketch, "E626", {"center": v(82.5, -217.13) * mm, "radius": 57.5 * mm});
            skLineSegment(sketch, "E627.bottom", {"start": v(138.5, -277.13) * mm, "end": v(26.5, -277.13) * mm});
            skLineSegment(sketch, "E627.left", {"start": v(142.5, -273.13) * mm, "end": v(142.5, -161.13) * mm});
            skLineSegment(sketch, "E627.right", {"start": v(22.5, -273.13) * mm, "end": v(22.5, -161.13) * mm});
            skPoint(sketch, "E628.visualSharp", {"position": v(22.5, -157.13) * mm});
            skArc(sketch, "E628.filletArc", {"start": v(26.5, -157.13) * mm, "mid": v(23.67, -158.3) * mm, "end": v(22.5, -161.13) * mm});
            skPoint(sketch, "E629.visualSharp", {"position": v(142.5, -157.13) * mm});
            skArc(sketch, "E629.filletArc", {"start": v(142.5, -161.13) * mm, "mid": v(141.33, -158.3) * mm, "end": v(138.5, -157.13) * mm});
            skPoint(sketch, "E630.visualSharp", {"position": v(22.5, -277.13) * mm});
            skArc(sketch, "E630.filletArc", {"start": v(22.5, -273.13) * mm, "mid": v(23.67, -275.96) * mm, "end": v(26.5, -277.13) * mm});
            skPoint(sketch, "E631.visualSharp", {"position": v(142.5, -277.13) * mm});
            skArc(sketch, "E631.filletArc", {"start": v(138.5, -277.13) * mm, "mid": v(141.33, -275.96) * mm, "end": v(142.5, -273.13) * mm});
            skCircle(sketch, "E632", {"center": v(137, -271.13) * mm, "radius": 2.5 * mm});
            skCircle(sketch, "E633", {"center": v(28.15, -271.25) * mm, "radius": 2.5 * mm});
            skCircle(sketch, "E634", {"center": v(28.39, -162.77) * mm, "radius": 2.5 * mm});
            skCircle(sketch, "E635", {"center": v(137.3, -163.32) * mm, "radius": 2.5 * mm});
            skLineSegment(sketch, "E636", {"start": v(-223.5, -157.13) * mm, "end": v(-111.5, -157.13) * mm});
            skLineSegment(sketch, "E637", {"start": v(26.5, -157.13) * mm, "end": v(138.5, -157.13) * mm});
            skLineSegment(sketch, "E638", {"start": v(-587.5, -65.23) * mm, "end": v(-417.5, -65.23) * mm});
            skLineSegment(sketch, "E639", {"start": v(-417.5, -65.23) * mm, "end": v(-417.5, -1.73) * mm});
            skCircle(sketch, "E640", {"center": v(-417.5, -1.73) * mm, "radius": 20 * mm});
            skCircle(sketch, "E641", {"center": v(-417.5, -1.73) * mm, "radius": 57.5 * mm});
            skLineSegment(sketch, "E642.bottom", {"start": v(-361.5, -61.73) * mm, "end": v(-473.5, -61.73) * mm});
            skLineSegment(sketch, "E642.top", {"start": v(-361.5, 58.27) * mm, "end": v(-473.5, 58.27) * mm});
            skLineSegment(sketch, "E642.left", {"start": v(-357.5, -57.73) * mm, "end": v(-357.5, 54.27) * mm});
            skLineSegment(sketch, "E642.right", {"start": v(-477.5, -57.73) * mm, "end": v(-477.5, 54.27) * mm});
            skPoint(sketch, "E643.visualSharp", {"position": v(-477.5, 58.27) * mm});
            skArc(sketch, "E643.filletArc", {"start": v(-473.5, 58.27) * mm, "mid": v(-476.33, 57.1) * mm, "end": v(-477.5, 54.27) * mm});
            skPoint(sketch, "E644.visualSharp", {"position": v(-357.5, 58.27) * mm});
            skArc(sketch, "E644.filletArc", {"start": v(-357.5, 54.27) * mm, "mid": v(-358.67, 57.1) * mm, "end": v(-361.5, 58.27) * mm});
            skPoint(sketch, "E645.visualSharp", {"position": v(-477.5, -61.73) * mm});
            skArc(sketch, "E645.filletArc", {"start": v(-477.5, -57.73) * mm, "mid": v(-476.33, -60.56) * mm, "end": v(-473.5, -61.73) * mm});
            skPoint(sketch, "E646.visualSharp", {"position": v(-357.5, -61.73) * mm});
            skArc(sketch, "E646.filletArc", {"start": v(-361.5, -61.73) * mm, "mid": v(-358.67, -60.56) * mm, "end": v(-357.5, -57.73) * mm});
            skCircle(sketch, "E647", {"center": v(-363, -55.73) * mm, "radius": 2.5 * mm});
            skCircle(sketch, "E648", {"center": v(-471.85, -55.85) * mm, "radius": 2.5 * mm});
            skCircle(sketch, "E649", {"center": v(-471.61, 52.63) * mm, "radius": 2.5 * mm});
            skCircle(sketch, "E650", {"center": v(-362.7, 52.08) * mm, "radius": 2.5 * mm});
            skLineSegment(sketch, "E651", {"start": v(-417.5, -1.73) * mm, "end": v(-167.5, -1.73) * mm, "construction": true});
            skCircle(sketch, "E652", {"center": v(-167.5, -1.73) * mm, "radius": 20 * mm});
            skCircle(sketch, "E653", {"center": v(-167.5, -1.73) * mm, "radius": 57.5 * mm});
            skLineSegment(sketch, "E654.bottom", {"start": v(-111.5, -61.73) * mm, "end": v(-223.5, -61.73) * mm});
            skLineSegment(sketch, "E654.left", {"start": v(-107.5, -57.73) * mm, "end": v(-107.5, 54.27) * mm});
            skLineSegment(sketch, "E654.right", {"start": v(-227.5, -57.73) * mm, "end": v(-227.5, 54.27) * mm});
            skPoint(sketch, "E655.visualSharp", {"position": v(-227.5, 58.27) * mm});
            skArc(sketch, "E655.filletArc", {"start": v(-223.5, 58.27) * mm, "mid": v(-226.33, 57.1) * mm, "end": v(-227.5, 54.27) * mm});
            skPoint(sketch, "E656.visualSharp", {"position": v(-107.5, 58.27) * mm});
            skArc(sketch, "E656.filletArc", {"start": v(-107.5, 54.27) * mm, "mid": v(-108.67, 57.1) * mm, "end": v(-111.5, 58.27) * mm});
            skPoint(sketch, "E657.visualSharp", {"position": v(-227.5, -61.73) * mm});
            skArc(sketch, "E657.filletArc", {"start": v(-227.5, -57.73) * mm, "mid": v(-226.33, -60.56) * mm, "end": v(-223.5, -61.73) * mm});
            skPoint(sketch, "E658.visualSharp", {"position": v(-107.5, -61.73) * mm});
            skArc(sketch, "E658.filletArc", {"start": v(-111.5, -61.73) * mm, "mid": v(-108.67, -60.56) * mm, "end": v(-107.5, -57.73) * mm});
            skCircle(sketch, "E659", {"center": v(-113, -55.73) * mm, "radius": 2.5 * mm});
            skCircle(sketch, "E660", {"center": v(-221.85, -55.85) * mm, "radius": 2.5 * mm});
            skCircle(sketch, "E661", {"center": v(-221.61, 52.63) * mm, "radius": 2.5 * mm});
            skCircle(sketch, "E662", {"center": v(-112.7, 52.08) * mm, "radius": 2.5 * mm});
            skLineSegment(sketch, "E663", {"start": v(-167.5, -1.73) * mm, "end": v(82.5, -1.73) * mm, "construction": true});
            skCircle(sketch, "E664", {"center": v(82.5, -1.73) * mm, "radius": 20 * mm});
            skCircle(sketch, "E665", {"center": v(82.5, -1.73) * mm, "radius": 57.5 * mm});
            skLineSegment(sketch, "E666.bottom", {"start": v(138.5, -61.73) * mm, "end": v(26.5, -61.73) * mm});
            skLineSegment(sketch, "E666.left", {"start": v(142.5, -57.73) * mm, "end": v(142.5, 54.27) * mm});
            skLineSegment(sketch, "E666.right", {"start": v(22.5, -57.73) * mm, "end": v(22.5, 54.27) * mm});
            skPoint(sketch, "E667.visualSharp", {"position": v(22.5, 58.27) * mm});
            skArc(sketch, "E667.filletArc", {"start": v(26.5, 58.27) * mm, "mid": v(23.67, 57.1) * mm, "end": v(22.5, 54.27) * mm});
            skPoint(sketch, "E668.visualSharp", {"position": v(142.5, 58.27) * mm});
            skArc(sketch, "E668.filletArc", {"start": v(142.5, 54.27) * mm, "mid": v(141.33, 57.1) * mm, "end": v(138.5, 58.27) * mm});
            skPoint(sketch, "E669.visualSharp", {"position": v(22.5, -61.73) * mm});
            skArc(sketch, "E669.filletArc", {"start": v(22.5, -57.73) * mm, "mid": v(23.67, -60.56) * mm, "end": v(26.5, -61.73) * mm});
            skPoint(sketch, "E670.visualSharp", {"position": v(142.5, -61.73) * mm});
            skArc(sketch, "E670.filletArc", {"start": v(138.5, -61.73) * mm, "mid": v(141.33, -60.56) * mm, "end": v(142.5, -57.73) * mm});
            skCircle(sketch, "E671", {"center": v(137, -55.73) * mm, "radius": 2.5 * mm});
            skCircle(sketch, "E672", {"center": v(28.15, -55.85) * mm, "radius": 2.5 * mm});
            skCircle(sketch, "E673", {"center": v(28.39, 52.63) * mm, "radius": 2.5 * mm});
            skCircle(sketch, "E674", {"center": v(137.3, 52.08) * mm, "radius": 2.5 * mm});
            skLineSegment(sketch, "E675", {"start": v(-223.5, 58.27) * mm, "end": v(-111.5, 58.27) * mm});
            skLineSegment(sketch, "E676", {"start": v(26.5, 58.27) * mm, "end": v(138.5, 58.27) * mm});
            skLineSegment(sketch, "E677", {"start": v(-587.5, 150.17) * mm, "end": v(-417.5, 150.17) * mm});
            skLineSegment(sketch, "E678", {"start": v(-417.5, 150.17) * mm, "end": v(-417.5, 213.67) * mm});
            skCircle(sketch, "E679", {"center": v(-417.5, 213.67) * mm, "radius": 20 * mm});
            skCircle(sketch, "E680", {"center": v(-417.5, 213.67) * mm, "radius": 57.5 * mm});
            skLineSegment(sketch, "E681.bottom", {"start": v(-361.5, 153.67) * mm, "end": v(-473.5, 153.67) * mm});
            skLineSegment(sketch, "E681.top", {"start": v(-361.5, 273.67) * mm, "end": v(-473.5, 273.67) * mm});
            skLineSegment(sketch, "E681.left", {"start": v(-357.5, 157.67) * mm, "end": v(-357.5, 269.67) * mm});
            skLineSegment(sketch, "E681.right", {"start": v(-477.5, 157.67) * mm, "end": v(-477.5, 269.67) * mm});
            skPoint(sketch, "E682.visualSharp", {"position": v(-477.5, 273.67) * mm});
            skArc(sketch, "E682.filletArc", {"start": v(-473.5, 273.67) * mm, "mid": v(-476.33, 272.5) * mm, "end": v(-477.5, 269.67) * mm});
            skPoint(sketch, "E683.visualSharp", {"position": v(-357.5, 273.67) * mm});
            skArc(sketch, "E683.filletArc", {"start": v(-357.5, 269.67) * mm, "mid": v(-358.67, 272.5) * mm, "end": v(-361.5, 273.67) * mm});
            skPoint(sketch, "E684.visualSharp", {"position": v(-477.5, 153.67) * mm});
            skArc(sketch, "E684.filletArc", {"start": v(-477.5, 157.67) * mm, "mid": v(-476.33, 154.84) * mm, "end": v(-473.5, 153.67) * mm});
            skPoint(sketch, "E685.visualSharp", {"position": v(-357.5, 153.67) * mm});
            skArc(sketch, "E685.filletArc", {"start": v(-361.5, 153.67) * mm, "mid": v(-358.67, 154.84) * mm, "end": v(-357.5, 157.67) * mm});
            skCircle(sketch, "E686", {"center": v(-363, 159.67) * mm, "radius": 2.5 * mm});
            skCircle(sketch, "E687", {"center": v(-471.85, 159.55) * mm, "radius": 2.5 * mm});
            skCircle(sketch, "E688", {"center": v(-471.61, 268.03) * mm, "radius": 2.5 * mm});
            skCircle(sketch, "E689", {"center": v(-362.7, 267.48) * mm, "radius": 2.5 * mm});
            skLineSegment(sketch, "E690", {"start": v(-417.5, 213.67) * mm, "end": v(-167.5, 213.67) * mm, "construction": true});
            skCircle(sketch, "E691", {"center": v(-167.5, 213.67) * mm, "radius": 20 * mm});
            skCircle(sketch, "E692", {"center": v(-167.5, 213.67) * mm, "radius": 57.5 * mm});
            skLineSegment(sketch, "E693.bottom", {"start": v(-111.5, 153.67) * mm, "end": v(-223.5, 153.67) * mm});
            skLineSegment(sketch, "E693.left", {"start": v(-107.5, 157.67) * mm, "end": v(-107.5, 269.67) * mm});
            skLineSegment(sketch, "E693.right", {"start": v(-227.5, 157.67) * mm, "end": v(-227.5, 269.67) * mm});
            skPoint(sketch, "E694.visualSharp", {"position": v(-227.5, 273.67) * mm});
            skArc(sketch, "E694.filletArc", {"start": v(-223.5, 273.67) * mm, "mid": v(-226.33, 272.5) * mm, "end": v(-227.5, 269.67) * mm});
            skPoint(sketch, "E695.visualSharp", {"position": v(-107.5, 273.67) * mm});
            skArc(sketch, "E695.filletArc", {"start": v(-107.5, 269.67) * mm, "mid": v(-108.67, 272.5) * mm, "end": v(-111.5, 273.67) * mm});
            skPoint(sketch, "E696.visualSharp", {"position": v(-227.5, 153.67) * mm});
            skArc(sketch, "E696.filletArc", {"start": v(-227.5, 157.67) * mm, "mid": v(-226.33, 154.84) * mm, "end": v(-223.5, 153.67) * mm});
            skPoint(sketch, "E697.visualSharp", {"position": v(-107.5, 153.67) * mm});
            skArc(sketch, "E697.filletArc", {"start": v(-111.5, 153.67) * mm, "mid": v(-108.67, 154.84) * mm, "end": v(-107.5, 157.67) * mm});
            skCircle(sketch, "E698", {"center": v(-113, 159.67) * mm, "radius": 2.5 * mm});
            skCircle(sketch, "E699", {"center": v(-221.85, 159.55) * mm, "radius": 2.5 * mm});
            skCircle(sketch, "E700", {"center": v(-221.61, 268.03) * mm, "radius": 2.5 * mm});
            skCircle(sketch, "E701", {"center": v(-112.7, 267.48) * mm, "radius": 2.5 * mm});
            skLineSegment(sketch, "E702", {"start": v(-167.5, 213.67) * mm, "end": v(82.5, 213.67) * mm, "construction": true});
            skCircle(sketch, "E703", {"center": v(82.5, 213.67) * mm, "radius": 20 * mm});
            skCircle(sketch, "E704", {"center": v(82.5, 213.67) * mm, "radius": 57.5 * mm});
            skLineSegment(sketch, "E705.bottom", {"start": v(138.5, 153.67) * mm, "end": v(26.5, 153.67) * mm});
            skLineSegment(sketch, "E705.left", {"start": v(142.5, 157.67) * mm, "end": v(142.5, 269.67) * mm});
            skLineSegment(sketch, "E705.right", {"start": v(22.5, 157.67) * mm, "end": v(22.5, 269.67) * mm});
            skPoint(sketch, "E706.visualSharp", {"position": v(22.5, 273.67) * mm});
            skArc(sketch, "E706.filletArc", {"start": v(26.5, 273.67) * mm, "mid": v(23.67, 272.5) * mm, "end": v(22.5, 269.67) * mm});
            skPoint(sketch, "E707.visualSharp", {"position": v(142.5, 273.67) * mm});
            skArc(sketch, "E707.filletArc", {"start": v(142.5, 269.67) * mm, "mid": v(141.33, 272.5) * mm, "end": v(138.5, 273.67) * mm});
            skPoint(sketch, "E708.visualSharp", {"position": v(22.5, 153.67) * mm});
            skArc(sketch, "E708.filletArc", {"start": v(22.5, 157.67) * mm, "mid": v(23.67, 154.84) * mm, "end": v(26.5, 153.67) * mm});
            skPoint(sketch, "E709.visualSharp", {"position": v(142.5, 153.67) * mm});
            skArc(sketch, "E709.filletArc", {"start": v(138.5, 153.67) * mm, "mid": v(141.33, 154.84) * mm, "end": v(142.5, 157.67) * mm});
            skCircle(sketch, "E710", {"center": v(137, 159.67) * mm, "radius": 2.5 * mm});
            skCircle(sketch, "E711", {"center": v(28.15, 159.55) * mm, "radius": 2.5 * mm});
            skCircle(sketch, "E712", {"center": v(28.39, 268.03) * mm, "radius": 2.5 * mm});
            skCircle(sketch, "E713", {"center": v(137.3, 267.48) * mm, "radius": 2.5 * mm});
            skLineSegment(sketch, "E714", {"start": v(-223.5, 273.67) * mm, "end": v(-111.5, 273.67) * mm});
            skLineSegment(sketch, "E715", {"start": v(26.5, 273.67) * mm, "end": v(138.5, 273.67) * mm});
            skSolve(sketch);
        }
        {
            var Q0;
            Q0=makeQuery(id+"F67.imprint","IMPRINT",FACE,{"disambiguationData":[TD([[makeQuery(id+"F67.imprint","IMPRINT",EDGE,{"derivedFrom":sQuery(id+"F67.wireOp",EDGE,"E602")}),-1.0]])]});
            var Q1;
            Q1=makeQuery(id+"F67.imprint","IMPRINT",FACE,{"disambiguationData":[TD([[makeQuery(id+"F67.imprint","IMPRINT",EDGE,{"derivedFrom":sQuery(id+"F67.wireOp",EDGE,"E614")}),-1.0]])]});
            var Q2;
            Q2=makeQuery(id+"F67.imprint","IMPRINT",FACE,{"disambiguationData":[TD([[makeQuery(id+"F67.imprint","IMPRINT",EDGE,{"derivedFrom":sQuery(id+"F67.wireOp",EDGE,"E653")}),-1.0]])]});
            var Q3;
            Q3=makeQuery(id+"F67.imprint","IMPRINT",FACE,{"disambiguationData":[TD([[makeQuery(id+"F67.imprint","IMPRINT",EDGE,{"derivedFrom":sQuery(id+"F67.wireOp",EDGE,"E641")}),-1.0]])]});
            var Q4;
            Q4=makeQuery(id+"F67.imprint","IMPRINT",FACE,{"disambiguationData":[TD([[makeQuery(id+"F67.imprint","IMPRINT",EDGE,{"derivedFrom":sQuery(id+"F67.wireOp",EDGE,"E665")}),-1.0]])]});
            var Q5;
            Q5=makeQuery(id+"F67.imprint","IMPRINT",FACE,{"disambiguationData":[TD([[makeQuery(id+"F67.imprint","IMPRINT",EDGE,{"derivedFrom":sQuery(id+"F67.wireOp",EDGE,"E626")}),-1.0]])]});
            var Q6;
            Q6=makeQuery(id+"F67.imprint","IMPRINT",FACE,{"disambiguationData":[TD([[makeQuery(id+"F67.imprint","IMPRINT",EDGE,{"derivedFrom":sQuery(id+"F67.wireOp",EDGE,"E704")}),-1.0]])]});
            var Q7;
            Q7=makeQuery(id+"F67.imprint","IMPRINT",FACE,{"disambiguationData":[TD([[makeQuery(id+"F67.imprint","IMPRINT",EDGE,{"derivedFrom":sQuery(id+"F67.wireOp",EDGE,"E692")}),-1.0]])]});
            var Q8;
            Q8=makeQuery(id+"F67.imprint","IMPRINT",FACE,{"disambiguationData":[TD([[makeQuery(id+"F67.imprint","IMPRINT",EDGE,{"derivedFrom":sQuery(id+"F67.wireOp",EDGE,"E680")}),-1.0]])]});
            extrude(context, id + "F68", {"entities" : qUnion([Q0, Q1, Q2, Q3, Q4, Q5, Q6, Q7, Q8]), "oppositeDirection" : true, "depth" : 5 * mm});
        }
        {
            var Q0;
            Q0=sQuery(id+"F67.wireOp",EDGE,"E602");
            var Q1;
            Q1=sQuery(id+"F67.wireOp",EDGE,"E614");
            var Q2;
            Q2=sQuery(id+"F67.wireOp",EDGE,"E626");
            var Q3;
            Q3=sQuery(id+"F67.wireOp",EDGE,"E665");
            var Q4;
            Q4=sQuery(id+"F67.wireOp",EDGE,"E653");
            var Q5;
            Q5=sQuery(id+"F67.wireOp",EDGE,"E641");
            var Q6;
            Q6=sQuery(id+"F67.wireOp",EDGE,"E680");
            var Q7;
            Q7=sQuery(id+"F67.wireOp",EDGE,"E692");
            var Q8;
            Q8=sQuery(id+"F67.wireOp",EDGE,"E704");
            extrude(context, id + "F69", {"bodyType" : ToolBodyType.SURFACE, "surfaceEntities" : qUnion([Q0, Q1, Q2, Q3, Q4, Q5, Q6, Q7, Q8]), "oppositeDirection" : true, "depth" : 38 * mm});
        }
        {
            var Q0;
            Q0=makeQuery(id+"F67.imprint","IMPRINT",FACE,{"disambiguationData":[TD([[makeQuery(id+"F67.imprint","IMPRINT",EDGE,{"derivedFrom":sQuery(id+"F67.wireOp",EDGE,"E601")}),1.0]])]});
            var Q1;
            Q1=makeQuery(id+"F67.imprint","IMPRINT",FACE,{"disambiguationData":[TD([[makeQuery(id+"F67.imprint","IMPRINT",EDGE,{"derivedFrom":sQuery(id+"F67.wireOp",EDGE,"E613")}),1.0]])]});
            var Q2;
            Q2=makeQuery(id+"F67.imprint","IMPRINT",FACE,{"disambiguationData":[TD([[makeQuery(id+"F67.imprint","IMPRINT",EDGE,{"derivedFrom":sQuery(id+"F67.wireOp",EDGE,"E625")}),1.0]])]});
            var Q3;
            Q3=makeQuery(id+"F67.imprint","IMPRINT",FACE,{"disambiguationData":[TD([[makeQuery(id+"F67.imprint","IMPRINT",EDGE,{"derivedFrom":sQuery(id+"F67.wireOp",EDGE,"E664")}),1.0]])]});
            var Q4;
            Q4=makeQuery(id+"F67.imprint","IMPRINT",FACE,{"disambiguationData":[TD([[makeQuery(id+"F67.imprint","IMPRINT",EDGE,{"derivedFrom":sQuery(id+"F67.wireOp",EDGE,"E652")}),1.0]])]});
            var Q5;
            Q5=makeQuery(id+"F67.imprint","IMPRINT",FACE,{"disambiguationData":[TD([[makeQuery(id+"F67.imprint","IMPRINT",EDGE,{"derivedFrom":sQuery(id+"F67.wireOp",EDGE,"E640")}),1.0]])]});
            var Q6;
            Q6=makeQuery(id+"F67.imprint","IMPRINT",FACE,{"disambiguationData":[TD([[makeQuery(id+"F67.imprint","IMPRINT",EDGE,{"derivedFrom":sQuery(id+"F67.wireOp",EDGE,"E703")}),1.0]])]});
            var Q7;
            Q7=makeQuery(id+"F67.imprint","IMPRINT",FACE,{"disambiguationData":[TD([[makeQuery(id+"F67.imprint","IMPRINT",EDGE,{"derivedFrom":sQuery(id+"F67.wireOp",EDGE,"E691")}),1.0]])]});
            var Q8;
            Q8=makeQuery(id+"F67.imprint","IMPRINT",FACE,{"disambiguationData":[TD([[makeQuery(id+"F67.imprint","IMPRINT",EDGE,{"derivedFrom":sQuery(id+"F67.wireOp",EDGE,"E679")}),1.0]])]});
            var Q9;
            Q9=sQuery(id+"F67.wireOp",EDGE,"E601");
            var Q10;
            Q10=sQuery(id+"F67.wireOp",EDGE,"E613");
            var Q11;
            Q11=sQuery(id+"F67.wireOp",EDGE,"E625");
            var Q12;
            Q12=sQuery(id+"F67.wireOp",EDGE,"E664");
            var Q13;
            Q13=sQuery(id+"F67.wireOp",EDGE,"E652");
            var Q14;
            Q14=sQuery(id+"F67.wireOp",EDGE,"E640");
            var Q15;
            Q15=sQuery(id+"F67.wireOp",EDGE,"E679");
            var Q16;
            Q16=sQuery(id+"F67.wireOp",EDGE,"E691");
            var Q17;
            Q17=sQuery(id+"F67.wireOp",EDGE,"E703");
            extrude(context, id + "F70", {"entities" : qUnion([Q0, Q1, Q2, Q3, Q4, Q5, Q6, Q7, Q8]), "surfaceEntities" : qUnion([Q9, Q10, Q11, Q12, Q13, Q14, Q15, Q16, Q17]), "oppositeDirection" : true, "depth" : 38 * mm});
        }
        {
            var Q0;
            Q0=makeQuery(id+"F70.opExtrude","CAP_FACE",FACE,{"disambiguationData":[OSD([sQuery(id+"F67.wireOp",EDGE,"E679")])],"isStart":true});
            var Q1;
            Q1=makeQuery(id+"F70.opExtrude","CAP_FACE",FACE,{"disambiguationData":[OSD([sQuery(id+"F67.wireOp",EDGE,"E691")])],"isStart":true});
            var Q2;
            Q2=makeQuery(id+"F70.opExtrude","CAP_FACE",FACE,{"disambiguationData":[OSD([sQuery(id+"F67.wireOp",EDGE,"E664")])],"isStart":true});
            var Q3;
            Q3=makeQuery(id+"F70.opExtrude","CAP_FACE",FACE,{"disambiguationData":[OSD([sQuery(id+"F67.wireOp",EDGE,"E652")])],"isStart":true});
            var Q4;
            Q4=makeQuery(id+"F70.opExtrude","CAP_FACE",FACE,{"disambiguationData":[OSD([sQuery(id+"F67.wireOp",EDGE,"E703")])],"isStart":true});
            var Q5;
            Q5=makeQuery(id+"F70.opExtrude","CAP_FACE",FACE,{"disambiguationData":[OSD([sQuery(id+"F67.wireOp",EDGE,"E640")])],"isStart":true});
            var Q6;
            Q6=makeQuery(id+"F70.opExtrude","CAP_FACE",FACE,{"disambiguationData":[OSD([sQuery(id+"F67.wireOp",EDGE,"E601")])],"isStart":true});
            var Q7;
            Q7=makeQuery(id+"F70.opExtrude","CAP_FACE",FACE,{"disambiguationData":[OSD([sQuery(id+"F67.wireOp",EDGE,"E613")])],"isStart":true});
            var Q8;
            Q8=makeQuery(id+"F70.opExtrude","CAP_FACE",FACE,{"disambiguationData":[OSD([sQuery(id+"F67.wireOp",EDGE,"E625")])],"isStart":true});
            fillet(context, id + "F71", {"entities" : qUnion([Q0, Q1, Q2, Q3, Q4, Q5, Q6, Q7, Q8]), "radius" : 3 * mm, "tangentPropagation" : true, "allowEdgeOverflow" : false});
        }
        {
            var Q0;
            Q0=makeQuery(id+"F68.opExtrude","CAP_EDGE",EDGE,{"disambiguationData":[OSD([sQuery(id+"F67.wireOp",EDGE,"E680")])],"isStart":true});
            var Q1;
            Q1=makeQuery(id+"F68.opExtrude","CAP_EDGE",EDGE,{"disambiguationData":[OSD([sQuery(id+"F67.wireOp",EDGE,"E692")])],"isStart":true});
            var Q2;
            Q2=makeQuery(id+"F68.opExtrude","CAP_EDGE",EDGE,{"disambiguationData":[OSD([sQuery(id+"F67.wireOp",EDGE,"E704")])],"isStart":true});
            var Q3;
            Q3=makeQuery(id+"F68.opExtrude","CAP_EDGE",EDGE,{"disambiguationData":[OSD([sQuery(id+"F67.wireOp",EDGE,"E665")])],"isStart":true});
            var Q4;
            Q4=makeQuery(id+"F68.opExtrude","CAP_EDGE",EDGE,{"disambiguationData":[OSD([sQuery(id+"F67.wireOp",EDGE,"E653")])],"isStart":true});
            var Q5;
            Q5=makeQuery(id+"F68.opExtrude","CAP_EDGE",EDGE,{"disambiguationData":[OSD([sQuery(id+"F67.wireOp",EDGE,"E641")])],"isStart":true});
            var Q6;
            Q6=makeQuery(id+"F68.opExtrude","CAP_EDGE",EDGE,{"disambiguationData":[OSD([sQuery(id+"F67.wireOp",EDGE,"E602")])],"isStart":true});
            var Q7;
            Q7=makeQuery(id+"F68.opExtrude","CAP_EDGE",EDGE,{"disambiguationData":[OSD([sQuery(id+"F67.wireOp",EDGE,"E614")])],"isStart":true});
            var Q8;
            Q8=makeQuery(id+"F68.opExtrude","CAP_EDGE",EDGE,{"disambiguationData":[OSD([sQuery(id+"F67.wireOp",EDGE,"E626")])],"isStart":true});
            fillet(context, id + "F72", {"entities" : qUnion([Q0, Q1, Q2, Q3, Q4, Q5, Q6, Q7, Q8]), "radius" : 1 * mm, "tangentPropagation" : true, "allowEdgeOverflow" : false});
        }
        {
            var Q0;
            Q0=makeQuery(id+"F70.opExtrude","CAP_FACE",FACE,{"disambiguationData":[OSD([sQuery(id+"F67.wireOp",EDGE,"E625")])],"isStart":false});
            var sketch = newSketch(context, id + "F73", { "sketchPlane" : qUnion([Q0])});
            skLineSegment(sketch, "E716.bottom", {"start": v(-361.5, 157.13) * mm, "end": v(-473.5, 157.13) * mm});
            skLineSegment(sketch, "E716.top", {"start": v(-361.5, 277.13) * mm, "end": v(-473.5, 277.13) * mm});
            skLineSegment(sketch, "E716.left", {"start": v(-357.5, 161.13) * mm, "end": v(-357.5, 273.13) * mm});
            skLineSegment(sketch, "E716.right", {"start": v(-477.5, 161.13) * mm, "end": v(-477.5, 273.13) * mm});
            skPoint(sketch, "E716.middle", {"position": v(-417.5, 217.13) * mm});
            skCircle(sketch, "E717", {"center": v(-417.5, 217.13) * mm, "radius": 57.5 * mm});
            skPoint(sketch, "E718.visualSharp", {"position": v(-477.5, 277.13) * mm});
            skArc(sketch, "E718.filletArc", {"start": v(-473.5, 277.13) * mm, "mid": v(-476.33, 275.96) * mm, "end": v(-477.5, 273.13) * mm});
            skPoint(sketch, "E719.visualSharp", {"position": v(-357.5, 277.13) * mm});
            skArc(sketch, "E719.filletArc", {"start": v(-357.5, 273.13) * mm, "mid": v(-358.67, 275.96) * mm, "end": v(-361.5, 277.13) * mm});
            skPoint(sketch, "E720.visualSharp", {"position": v(-357.5, 157.13) * mm});
            skArc(sketch, "E720.filletArc", {"start": v(-361.5, 157.13) * mm, "mid": v(-358.67, 158.3) * mm, "end": v(-357.5, 161.13) * mm});
            skPoint(sketch, "E721.visualSharp", {"position": v(-477.5, 157.13) * mm});
            skArc(sketch, "E721.filletArc", {"start": v(-477.5, 161.13) * mm, "mid": v(-476.33, 158.3) * mm, "end": v(-473.5, 157.13) * mm});
            skCircle(sketch, "E722", {"center": v(-471.87, 163.03) * mm, "radius": 2.5 * mm});
            skCircle(sketch, "E723", {"center": v(-362.45, 163.44) * mm, "radius": 2.5 * mm});
            skCircle(sketch, "E724", {"center": v(-363.42, 271.53) * mm, "radius": 2.5 * mm});
            skCircle(sketch, "E725", {"center": v(-471.98, 271.14) * mm, "radius": 2.5 * mm});
            skLineSegment(sketch, "E726", {"start": v(-417.5, 217.13) * mm, "end": v(-167.5, 217.13) * mm, "construction": true});
            skLineSegment(sketch, "E727.bottom", {"start": v(-111.5, 157.13) * mm, "end": v(-223.5, 157.13) * mm});
            skLineSegment(sketch, "E727.top", {"start": v(-111.5, 277.13) * mm, "end": v(-223.5, 277.13) * mm});
            skLineSegment(sketch, "E727.left", {"start": v(-107.5, 161.13) * mm, "end": v(-107.5, 273.13) * mm});
            skLineSegment(sketch, "E727.right", {"start": v(-227.5, 161.13) * mm, "end": v(-227.5, 273.13) * mm});
            skPoint(sketch, "E727.middle", {"position": v(-167.5, 217.13) * mm});
            skCircle(sketch, "E728", {"center": v(-167.5, 217.13) * mm, "radius": 57.5 * mm});
            skPoint(sketch, "E729.visualSharp", {"position": v(-227.5, 277.13) * mm});
            skArc(sketch, "E729.filletArc", {"start": v(-223.5, 277.13) * mm, "mid": v(-226.33, 275.96) * mm, "end": v(-227.5, 273.13) * mm});
            skPoint(sketch, "E730.visualSharp", {"position": v(-107.5, 277.13) * mm});
            skArc(sketch, "E730.filletArc", {"start": v(-107.5, 273.13) * mm, "mid": v(-108.67, 275.96) * mm, "end": v(-111.5, 277.13) * mm});
            skPoint(sketch, "E731.visualSharp", {"position": v(-107.5, 157.13) * mm});
            skArc(sketch, "E731.filletArc", {"start": v(-111.5, 157.13) * mm, "mid": v(-108.67, 158.3) * mm, "end": v(-107.5, 161.13) * mm});
            skPoint(sketch, "E732.visualSharp", {"position": v(-227.5, 157.13) * mm});
            skArc(sketch, "E732.filletArc", {"start": v(-227.5, 161.13) * mm, "mid": v(-226.33, 158.3) * mm, "end": v(-223.5, 157.13) * mm});
            skCircle(sketch, "E733", {"center": v(-221.87, 163.03) * mm, "radius": 2.5 * mm});
            skCircle(sketch, "E734", {"center": v(-112.45, 163.44) * mm, "radius": 2.5 * mm});
            skCircle(sketch, "E735", {"center": v(-113.42, 271.53) * mm, "radius": 2.5 * mm});
            skCircle(sketch, "E736", {"center": v(-221.98, 271.14) * mm, "radius": 2.5 * mm});
            skLineSegment(sketch, "E737", {"start": v(-167.5, 217.13) * mm, "end": v(82.5, 217.13) * mm, "construction": true});
            skLineSegment(sketch, "E738.bottom", {"start": v(138.5, 157.13) * mm, "end": v(26.5, 157.13) * mm});
            skLineSegment(sketch, "E738.top", {"start": v(138.5, 277.13) * mm, "end": v(26.5, 277.13) * mm});
            skLineSegment(sketch, "E738.left", {"start": v(142.5, 161.13) * mm, "end": v(142.5, 273.13) * mm});
            skLineSegment(sketch, "E738.right", {"start": v(22.5, 161.13) * mm, "end": v(22.5, 273.13) * mm});
            skPoint(sketch, "E738.middle", {"position": v(82.5, 217.13) * mm});
            skCircle(sketch, "E739", {"center": v(82.5, 217.13) * mm, "radius": 57.5 * mm});
            skPoint(sketch, "E740.visualSharp", {"position": v(22.5, 277.13) * mm});
            skArc(sketch, "E740.filletArc", {"start": v(26.5, 277.13) * mm, "mid": v(23.67, 275.96) * mm, "end": v(22.5, 273.13) * mm});
            skPoint(sketch, "E741.visualSharp", {"position": v(142.5, 277.13) * mm});
            skArc(sketch, "E741.filletArc", {"start": v(142.5, 273.13) * mm, "mid": v(141.33, 275.96) * mm, "end": v(138.5, 277.13) * mm});
            skPoint(sketch, "E742.visualSharp", {"position": v(142.5, 157.13) * mm});
            skArc(sketch, "E742.filletArc", {"start": v(138.5, 157.13) * mm, "mid": v(141.33, 158.3) * mm, "end": v(142.5, 161.13) * mm});
            skPoint(sketch, "E743.visualSharp", {"position": v(22.5, 157.13) * mm});
            skArc(sketch, "E743.filletArc", {"start": v(22.5, 161.13) * mm, "mid": v(23.67, 158.3) * mm, "end": v(26.5, 157.13) * mm});
            skCircle(sketch, "E744", {"center": v(28.13, 163.03) * mm, "radius": 2.5 * mm});
            skCircle(sketch, "E745", {"center": v(137.55, 163.44) * mm, "radius": 2.5 * mm});
            skCircle(sketch, "E746", {"center": v(136.58, 271.53) * mm, "radius": 2.5 * mm});
            skCircle(sketch, "E747", {"center": v(28.02, 271.14) * mm, "radius": 2.5 * mm});
            skLineSegment(sketch, "E748.bottom", {"start": v(-361.5, -58.27) * mm, "end": v(-473.5, -58.27) * mm});
            skLineSegment(sketch, "E748.top", {"start": v(-361.5, 61.73) * mm, "end": v(-473.5, 61.73) * mm});
            skLineSegment(sketch, "E748.left", {"start": v(-357.5, -54.27) * mm, "end": v(-357.5, 57.73) * mm});
            skLineSegment(sketch, "E748.right", {"start": v(-477.5, -54.27) * mm, "end": v(-477.5, 57.73) * mm});
            skPoint(sketch, "E748.middle", {"position": v(-417.5, 1.73) * mm});
            skCircle(sketch, "E749", {"center": v(-417.5, 1.73) * mm, "radius": 57.5 * mm});
            skPoint(sketch, "E750.visualSharp", {"position": v(-477.5, 61.73) * mm});
            skArc(sketch, "E750.filletArc", {"start": v(-473.5, 61.73) * mm, "mid": v(-476.33, 60.56) * mm, "end": v(-477.5, 57.73) * mm});
            skPoint(sketch, "E751.visualSharp", {"position": v(-357.5, 61.73) * mm});
            skArc(sketch, "E751.filletArc", {"start": v(-357.5, 57.73) * mm, "mid": v(-358.67, 60.56) * mm, "end": v(-361.5, 61.73) * mm});
            skPoint(sketch, "E752.visualSharp", {"position": v(-357.5, -58.27) * mm});
            skArc(sketch, "E752.filletArc", {"start": v(-361.5, -58.27) * mm, "mid": v(-358.67, -57.1) * mm, "end": v(-357.5, -54.27) * mm});
            skPoint(sketch, "E753.visualSharp", {"position": v(-477.5, -58.27) * mm});
            skArc(sketch, "E753.filletArc", {"start": v(-477.5, -54.27) * mm, "mid": v(-476.33, -57.1) * mm, "end": v(-473.5, -58.27) * mm});
            skCircle(sketch, "E754", {"center": v(-471.87, -52.37) * mm, "radius": 2.5 * mm});
            skCircle(sketch, "E755", {"center": v(-362.45, -51.96) * mm, "radius": 2.5 * mm});
            skCircle(sketch, "E756", {"center": v(-363.42, 56.13) * mm, "radius": 2.5 * mm});
            skCircle(sketch, "E757", {"center": v(-471.98, 55.74) * mm, "radius": 2.5 * mm});
            skLineSegment(sketch, "E758", {"start": v(-417.5, 1.73) * mm, "end": v(-167.5, 1.73) * mm, "construction": true});
            skLineSegment(sketch, "E759.bottom", {"start": v(-111.5, -58.27) * mm, "end": v(-223.5, -58.27) * mm});
            skLineSegment(sketch, "E759.top", {"start": v(-111.5, 61.73) * mm, "end": v(-223.5, 61.73) * mm});
            skLineSegment(sketch, "E759.left", {"start": v(-107.5, -54.27) * mm, "end": v(-107.5, 57.73) * mm});
            skLineSegment(sketch, "E759.right", {"start": v(-227.5, -54.27) * mm, "end": v(-227.5, 57.73) * mm});
            skPoint(sketch, "E759.middle", {"position": v(-167.5, 1.73) * mm});
            skCircle(sketch, "E760", {"center": v(-167.5, 1.73) * mm, "radius": 57.5 * mm});
            skPoint(sketch, "E761.visualSharp", {"position": v(-227.5, 61.73) * mm});
            skArc(sketch, "E761.filletArc", {"start": v(-223.5, 61.73) * mm, "mid": v(-226.33, 60.56) * mm, "end": v(-227.5, 57.73) * mm});
            skPoint(sketch, "E762.visualSharp", {"position": v(-107.5, 61.73) * mm});
            skArc(sketch, "E762.filletArc", {"start": v(-107.5, 57.73) * mm, "mid": v(-108.67, 60.56) * mm, "end": v(-111.5, 61.73) * mm});
            skPoint(sketch, "E763.visualSharp", {"position": v(-107.5, -58.27) * mm});
            skArc(sketch, "E763.filletArc", {"start": v(-111.5, -58.27) * mm, "mid": v(-108.67, -57.1) * mm, "end": v(-107.5, -54.27) * mm});
            skPoint(sketch, "E764.visualSharp", {"position": v(-227.5, -58.27) * mm});
            skArc(sketch, "E764.filletArc", {"start": v(-227.5, -54.27) * mm, "mid": v(-226.33, -57.1) * mm, "end": v(-223.5, -58.27) * mm});
            skCircle(sketch, "E765", {"center": v(-221.87, -52.37) * mm, "radius": 2.5 * mm});
            skCircle(sketch, "E766", {"center": v(-112.45, -51.96) * mm, "radius": 2.5 * mm});
            skCircle(sketch, "E767", {"center": v(-113.42, 56.13) * mm, "radius": 2.5 * mm});
            skCircle(sketch, "E768", {"center": v(-221.98, 55.74) * mm, "radius": 2.5 * mm});
            skLineSegment(sketch, "E769", {"start": v(-167.5, 1.73) * mm, "end": v(82.5, 1.73) * mm, "construction": true});
            skLineSegment(sketch, "E770.bottom", {"start": v(138.5, -58.27) * mm, "end": v(26.5, -58.27) * mm});
            skLineSegment(sketch, "E770.top", {"start": v(138.5, 61.73) * mm, "end": v(26.5, 61.73) * mm});
            skLineSegment(sketch, "E770.left", {"start": v(142.5, -54.27) * mm, "end": v(142.5, 57.73) * mm});
            skLineSegment(sketch, "E770.right", {"start": v(22.5, -54.27) * mm, "end": v(22.5, 57.73) * mm});
            skPoint(sketch, "E770.middle", {"position": v(82.5, 1.73) * mm});
            skCircle(sketch, "E771", {"center": v(82.5, 1.73) * mm, "radius": 57.5 * mm});
            skPoint(sketch, "E772.visualSharp", {"position": v(22.5, 61.73) * mm});
            skArc(sketch, "E772.filletArc", {"start": v(26.5, 61.73) * mm, "mid": v(23.67, 60.56) * mm, "end": v(22.5, 57.73) * mm});
            skPoint(sketch, "E773.visualSharp", {"position": v(142.5, 61.73) * mm});
            skArc(sketch, "E773.filletArc", {"start": v(142.5, 57.73) * mm, "mid": v(141.33, 60.56) * mm, "end": v(138.5, 61.73) * mm});
            skPoint(sketch, "E774.visualSharp", {"position": v(142.5, -58.27) * mm});
            skArc(sketch, "E774.filletArc", {"start": v(138.5, -58.27) * mm, "mid": v(141.33, -57.1) * mm, "end": v(142.5, -54.27) * mm});
            skPoint(sketch, "E775.visualSharp", {"position": v(22.5, -58.27) * mm});
            skArc(sketch, "E775.filletArc", {"start": v(22.5, -54.27) * mm, "mid": v(23.67, -57.1) * mm, "end": v(26.5, -58.27) * mm});
            skCircle(sketch, "E776", {"center": v(28.13, -52.37) * mm, "radius": 2.5 * mm});
            skCircle(sketch, "E777", {"center": v(137.55, -51.96) * mm, "radius": 2.5 * mm});
            skCircle(sketch, "E778", {"center": v(136.58, 56.13) * mm, "radius": 2.5 * mm});
            skCircle(sketch, "E779", {"center": v(28.02, 55.74) * mm, "radius": 2.5 * mm});
            skLineSegment(sketch, "E780", {"start": v(82.5, 217.13) * mm, "end": v(82.5, 65.23) * mm, "construction": true});
            skLineSegment(sketch, "E781", {"start": v(82.5, 65.23) * mm, "end": v(82.5, 1.73) * mm, "construction": true});
            skLineSegment(sketch, "E782.bottom", {"start": v(-361.5, -273.67) * mm, "end": v(-473.5, -273.67) * mm});
            skLineSegment(sketch, "E782.top", {"start": v(-361.5, -153.67) * mm, "end": v(-473.5, -153.67) * mm});
            skLineSegment(sketch, "E782.left", {"start": v(-357.5, -269.67) * mm, "end": v(-357.5, -157.67) * mm});
            skLineSegment(sketch, "E782.right", {"start": v(-477.5, -269.67) * mm, "end": v(-477.5, -157.67) * mm});
            skPoint(sketch, "E782.middle", {"position": v(-417.5, -213.67) * mm});
            skCircle(sketch, "E783", {"center": v(-417.5, -213.67) * mm, "radius": 57.5 * mm});
            skPoint(sketch, "E784.visualSharp", {"position": v(-477.5, -153.67) * mm});
            skArc(sketch, "E784.filletArc", {"start": v(-473.5, -153.67) * mm, "mid": v(-476.33, -154.84) * mm, "end": v(-477.5, -157.67) * mm});
            skPoint(sketch, "E785.visualSharp", {"position": v(-357.5, -153.67) * mm});
            skArc(sketch, "E785.filletArc", {"start": v(-357.5, -157.67) * mm, "mid": v(-358.67, -154.84) * mm, "end": v(-361.5, -153.67) * mm});
            skPoint(sketch, "E786.visualSharp", {"position": v(-357.5, -273.67) * mm});
            skArc(sketch, "E786.filletArc", {"start": v(-361.5, -273.67) * mm, "mid": v(-358.67, -272.5) * mm, "end": v(-357.5, -269.67) * mm});
            skPoint(sketch, "E787.visualSharp", {"position": v(-477.5, -273.67) * mm});
            skArc(sketch, "E787.filletArc", {"start": v(-477.5, -269.67) * mm, "mid": v(-476.33, -272.5) * mm, "end": v(-473.5, -273.67) * mm});
            skCircle(sketch, "E788", {"center": v(-471.87, -267.77) * mm, "radius": 2.5 * mm});
            skCircle(sketch, "E789", {"center": v(-362.45, -267.36) * mm, "radius": 2.5 * mm});
            skCircle(sketch, "E790", {"center": v(-363.42, -159.27) * mm, "radius": 2.5 * mm});
            skCircle(sketch, "E791", {"center": v(-471.98, -159.66) * mm, "radius": 2.5 * mm});
            skLineSegment(sketch, "E792", {"start": v(-417.5, -213.67) * mm, "end": v(-167.5, -213.67) * mm, "construction": true});
            skLineSegment(sketch, "E793.bottom", {"start": v(-111.5, -273.67) * mm, "end": v(-223.5, -273.67) * mm});
            skLineSegment(sketch, "E793.top", {"start": v(-111.5, -153.67) * mm, "end": v(-223.5, -153.67) * mm});
            skLineSegment(sketch, "E793.left", {"start": v(-107.5, -269.67) * mm, "end": v(-107.5, -157.67) * mm});
            skLineSegment(sketch, "E793.right", {"start": v(-227.5, -269.67) * mm, "end": v(-227.5, -157.67) * mm});
            skPoint(sketch, "E793.middle", {"position": v(-167.5, -213.67) * mm});
            skCircle(sketch, "E794", {"center": v(-167.5, -213.67) * mm, "radius": 57.5 * mm});
            skPoint(sketch, "E795.visualSharp", {"position": v(-227.5, -153.67) * mm});
            skArc(sketch, "E795.filletArc", {"start": v(-223.5, -153.67) * mm, "mid": v(-226.33, -154.84) * mm, "end": v(-227.5, -157.67) * mm});
            skPoint(sketch, "E796.visualSharp", {"position": v(-107.5, -153.67) * mm});
            skArc(sketch, "E796.filletArc", {"start": v(-107.5, -157.67) * mm, "mid": v(-108.67, -154.84) * mm, "end": v(-111.5, -153.67) * mm});
            skPoint(sketch, "E797.visualSharp", {"position": v(-107.5, -273.67) * mm});
            skArc(sketch, "E797.filletArc", {"start": v(-111.5, -273.67) * mm, "mid": v(-108.67, -272.5) * mm, "end": v(-107.5, -269.67) * mm});
            skPoint(sketch, "E798.visualSharp", {"position": v(-227.5, -273.67) * mm});
            skArc(sketch, "E798.filletArc", {"start": v(-227.5, -269.67) * mm, "mid": v(-226.33, -272.5) * mm, "end": v(-223.5, -273.67) * mm});
            skCircle(sketch, "E799", {"center": v(-221.87, -267.77) * mm, "radius": 2.5 * mm});
            skCircle(sketch, "E800", {"center": v(-112.45, -267.36) * mm, "radius": 2.5 * mm});
            skCircle(sketch, "E801", {"center": v(-113.42, -159.27) * mm, "radius": 2.5 * mm});
            skCircle(sketch, "E802", {"center": v(-221.98, -159.66) * mm, "radius": 2.5 * mm});
            skLineSegment(sketch, "E803", {"start": v(-167.5, -213.67) * mm, "end": v(82.5, -213.67) * mm, "construction": true});
            skLineSegment(sketch, "E804.bottom", {"start": v(138.5, -273.67) * mm, "end": v(26.5, -273.67) * mm});
            skLineSegment(sketch, "E804.top", {"start": v(138.5, -153.67) * mm, "end": v(26.5, -153.67) * mm});
            skLineSegment(sketch, "E804.left", {"start": v(142.5, -269.67) * mm, "end": v(142.5, -157.67) * mm});
            skLineSegment(sketch, "E804.right", {"start": v(22.5, -269.67) * mm, "end": v(22.5, -157.67) * mm});
            skPoint(sketch, "E804.middle", {"position": v(82.5, -213.67) * mm});
            skCircle(sketch, "E805", {"center": v(82.5, -213.67) * mm, "radius": 57.5 * mm});
            skPoint(sketch, "E806.visualSharp", {"position": v(22.5, -153.67) * mm});
            skArc(sketch, "E806.filletArc", {"start": v(26.5, -153.67) * mm, "mid": v(23.67, -154.84) * mm, "end": v(22.5, -157.67) * mm});
            skPoint(sketch, "E807.visualSharp", {"position": v(142.5, -153.67) * mm});
            skArc(sketch, "E807.filletArc", {"start": v(142.5, -157.67) * mm, "mid": v(141.33, -154.84) * mm, "end": v(138.5, -153.67) * mm});
            skPoint(sketch, "E808.visualSharp", {"position": v(142.5, -273.67) * mm});
            skArc(sketch, "E808.filletArc", {"start": v(138.5, -273.67) * mm, "mid": v(141.33, -272.5) * mm, "end": v(142.5, -269.67) * mm});
            skPoint(sketch, "E809.visualSharp", {"position": v(22.5, -273.67) * mm});
            skArc(sketch, "E809.filletArc", {"start": v(22.5, -269.67) * mm, "mid": v(23.67, -272.5) * mm, "end": v(26.5, -273.67) * mm});
            skCircle(sketch, "E810", {"center": v(28.13, -267.77) * mm, "radius": 2.5 * mm});
            skCircle(sketch, "E811", {"center": v(137.55, -267.36) * mm, "radius": 2.5 * mm});
            skCircle(sketch, "E812", {"center": v(136.58, -159.27) * mm, "radius": 2.5 * mm});
            skCircle(sketch, "E813", {"center": v(28.02, -159.66) * mm, "radius": 2.5 * mm});
            skLineSegment(sketch, "E814", {"start": v(82.5, 1.73) * mm, "end": v(82.5, -213.67) * mm, "construction": true});
            skLineSegment(sketch, "E815", {"start": v(-587.5, 280.63) * mm, "end": v(-417.5, 280.63) * mm, "construction": true});
            skLineSegment(sketch, "E816", {"start": v(-417.5, 280.63) * mm, "end": v(-417.5, 217.13) * mm, "construction": true});
            skSolve(sketch);
        }
        {
            var Q0;
            Q0=makeQuery(id+"F73.imprint","IMPRINT",FACE,{"disambiguationData":[TD([[makeQuery(id+"F73.imprint","IMPRINT",EDGE,{"derivedFrom":sQuery(id+"F73.wireOp",EDGE,"E748.bottom")}),-1.0]])]});
            var Q1;
            Q1=makeQuery(id+"F73.imprint","IMPRINT",FACE,{"disambiguationData":[TD([[makeQuery(id+"F73.imprint","IMPRINT",EDGE,{"derivedFrom":sQuery(id+"F73.wireOp",EDGE,"E759.bottom")}),-1.0]])]});
            var Q2;
            Q2=makeQuery(id+"F73.imprint","IMPRINT",FACE,{"disambiguationData":[TD([[makeQuery(id+"F73.imprint","IMPRINT",EDGE,{"derivedFrom":sQuery(id+"F73.wireOp",EDGE,"E793.bottom")}),-1.0]])]});
            var Q3;
            Q3=makeQuery(id+"F73.imprint","IMPRINT",FACE,{"disambiguationData":[TD([[makeQuery(id+"F73.imprint","IMPRINT",EDGE,{"derivedFrom":sQuery(id+"F73.wireOp",EDGE,"E782.bottom")}),-1.0]])]});
            var Q4;
            Q4=makeQuery(id+"F73.imprint","IMPRINT",FACE,{"disambiguationData":[TD([[makeQuery(id+"F73.imprint","IMPRINT",EDGE,{"derivedFrom":sQuery(id+"F73.wireOp",EDGE,"E804.bottom")}),-1.0]])]});
            var Q5;
            Q5=makeQuery(id+"F73.imprint","IMPRINT",FACE,{"disambiguationData":[TD([[makeQuery(id+"F73.imprint","IMPRINT",EDGE,{"derivedFrom":sQuery(id+"F73.wireOp",EDGE,"E770.bottom")}),-1.0]])]});
            var Q6;
            Q6=makeQuery(id+"F73.imprint","IMPRINT",FACE,{"disambiguationData":[TD([[makeQuery(id+"F73.imprint","IMPRINT",EDGE,{"derivedFrom":sQuery(id+"F73.wireOp",EDGE,"E727.bottom")}),-1.0]])]});
            var Q7;
            Q7=makeQuery(id+"F73.imprint","IMPRINT",FACE,{"disambiguationData":[TD([[makeQuery(id+"F73.imprint","IMPRINT",EDGE,{"derivedFrom":sQuery(id+"F73.wireOp",EDGE,"E738.bottom")}),-1.0]])]});
            var Q8;
            Q8=makeQuery(id+"F73.imprint","IMPRINT",FACE,{"disambiguationData":[TD([[makeQuery(id+"F73.imprint","IMPRINT",EDGE,{"derivedFrom":sQuery(id+"F73.wireOp",EDGE,"E716.bottom")}),-1.0]])]});
            extrude(context, id + "F74", {"entities" : qUnion([Q0, Q1, Q2, Q3, Q4, Q5, Q6, Q7, Q8]), "oppositeDirection" : true, "depth" : 5 * mm});
        }
        {
            var Q0;
            Q0=makeQuery(id+"F70.opExtrude","CAP_FACE",FACE,{"disambiguationData":[OSD([sQuery(id+"F67.wireOp",EDGE,"E601")])],"isStart":false});
            var Q1;
            Q1=makeQuery(id+"F70.opExtrude","CAP_FACE",FACE,{"disambiguationData":[OSD([sQuery(id+"F67.wireOp",EDGE,"E613")])],"isStart":false});
            var Q2;
            Q2=makeQuery(id+"F70.opExtrude","CAP_FACE",FACE,{"disambiguationData":[OSD([sQuery(id+"F67.wireOp",EDGE,"E664")])],"isStart":false});
            var Q3;
            Q3=makeQuery(id+"F70.opExtrude","CAP_FACE",FACE,{"disambiguationData":[OSD([sQuery(id+"F67.wireOp",EDGE,"E625")])],"isStart":false});
            var Q4;
            Q4=makeQuery(id+"F70.opExtrude","CAP_FACE",FACE,{"disambiguationData":[OSD([sQuery(id+"F67.wireOp",EDGE,"E652")])],"isStart":false});
            var Q5;
            Q5=makeQuery(id+"F70.opExtrude","CAP_FACE",FACE,{"disambiguationData":[OSD([sQuery(id+"F67.wireOp",EDGE,"E640")])],"isStart":false});
            var Q6;
            Q6=makeQuery(id+"F70.opExtrude","CAP_FACE",FACE,{"disambiguationData":[OSD([sQuery(id+"F67.wireOp",EDGE,"E679")])],"isStart":false});
            var Q7;
            Q7=makeQuery(id+"F70.opExtrude","CAP_FACE",FACE,{"disambiguationData":[OSD([sQuery(id+"F67.wireOp",EDGE,"E691")])],"isStart":false});
            var Q8;
            Q8=makeQuery(id+"F70.opExtrude","CAP_FACE",FACE,{"disambiguationData":[OSD([sQuery(id+"F67.wireOp",EDGE,"E703")])],"isStart":false});
            fillet(context, id + "F75", {"entities" : qUnion([Q0, Q1, Q2, Q3, Q4, Q5, Q6, Q7, Q8]), "radius" : 3 * mm, "tangentPropagation" : true, "allowEdgeOverflow" : false});
        }
        {
            var Q0;
            Q0=makeQuery(id+"F74.opExtrude","CAP_EDGE",EDGE,{"disambiguationData":[OSD([sQuery(id+"F73.wireOp",EDGE,"E783")])],"isStart":false});
            var Q1;
            Q1=makeQuery(id+"F74.opExtrude","CAP_EDGE",EDGE,{"disambiguationData":[OSD([sQuery(id+"F73.wireOp",EDGE,"E794")])],"isStart":false});
            var Q2;
            Q2=makeQuery(id+"F74.opExtrude","CAP_EDGE",EDGE,{"disambiguationData":[OSD([sQuery(id+"F73.wireOp",EDGE,"E805")])],"isStart":false});
            var Q3;
            Q3=makeQuery(id+"F74.opExtrude","CAP_EDGE",EDGE,{"disambiguationData":[OSD([sQuery(id+"F73.wireOp",EDGE,"E749")])],"isStart":false});
            var Q4;
            Q4=makeQuery(id+"F74.opExtrude","CAP_EDGE",EDGE,{"disambiguationData":[OSD([sQuery(id+"F73.wireOp",EDGE,"E760")])],"isStart":false});
            var Q5;
            Q5=makeQuery(id+"F74.opExtrude","CAP_EDGE",EDGE,{"disambiguationData":[OSD([sQuery(id+"F73.wireOp",EDGE,"E771")])],"isStart":false});
            var Q6;
            Q6=makeQuery(id+"F74.opExtrude","CAP_EDGE",EDGE,{"disambiguationData":[OSD([sQuery(id+"F73.wireOp",EDGE,"E739")])],"isStart":false});
            var Q7;
            Q7=makeQuery(id+"F74.opExtrude","CAP_EDGE",EDGE,{"disambiguationData":[OSD([sQuery(id+"F73.wireOp",EDGE,"E728")])],"isStart":false});
            var Q8;
            Q8=makeQuery(id+"F74.opExtrude","CAP_EDGE",EDGE,{"disambiguationData":[OSD([sQuery(id+"F73.wireOp",EDGE,"E717")])],"isStart":false});
            fillet(context, id + "F76", {"entities" : qUnion([Q0, Q1, Q2, Q3, Q4, Q5, Q6, Q7, Q8]), "radius" : 1 * mm, "tangentPropagation" : true, "allowEdgeOverflow" : false});
        }
    });
